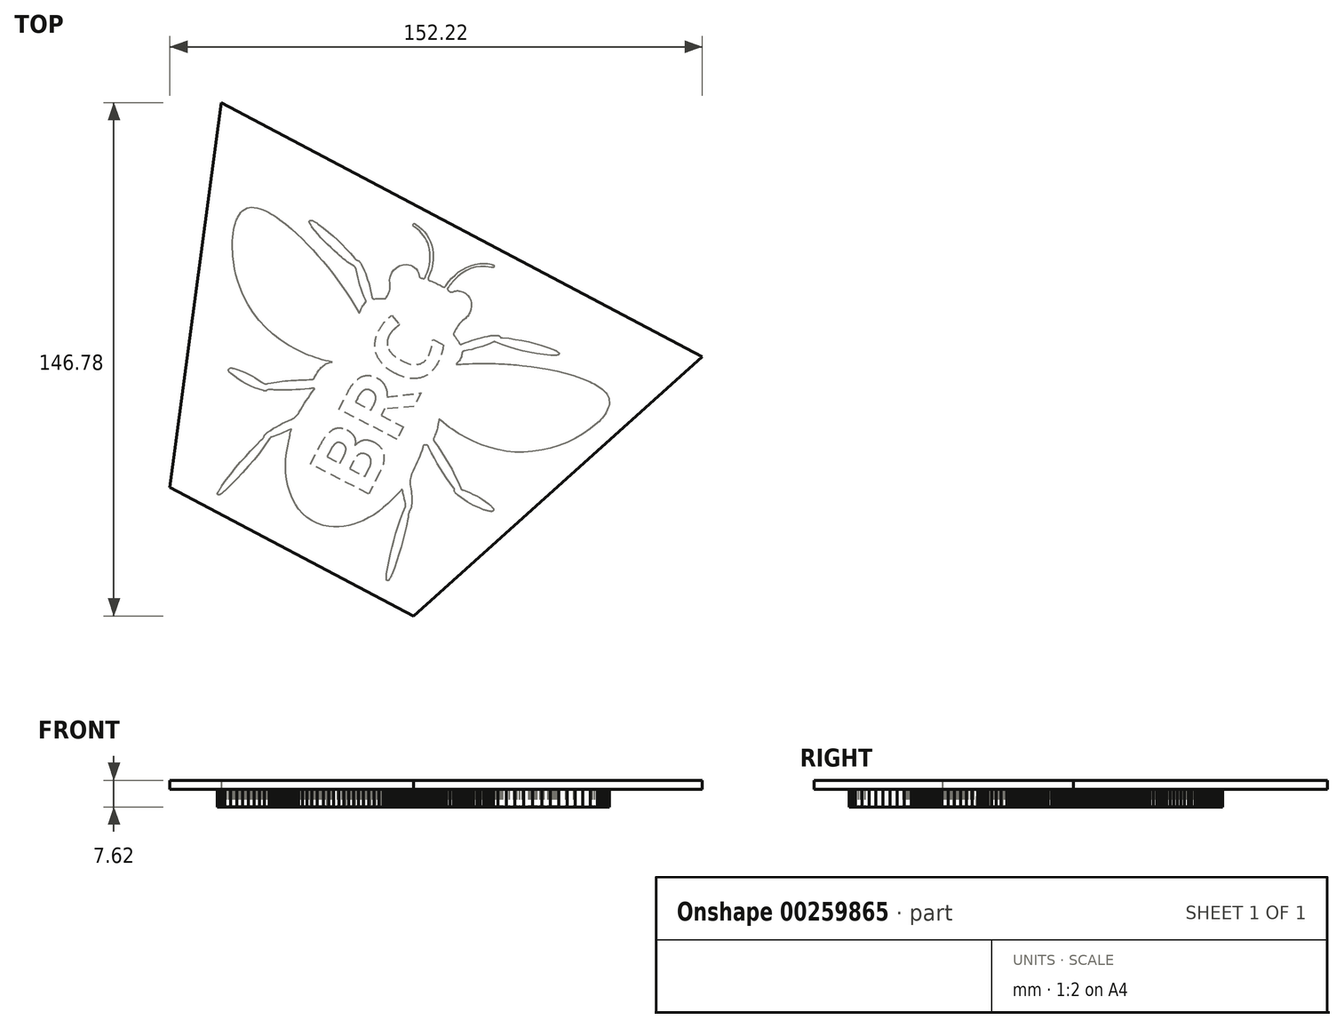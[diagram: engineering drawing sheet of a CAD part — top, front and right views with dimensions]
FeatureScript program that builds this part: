
annotation { "Feature Type Name" : "Feature", "Feature Type Description" : "" }
export const myFeature = defineFeature(function(context is Context, id is Id, definition is map)
    precondition{}
    {
        {
            var Q0;
            Q0=qCreatedBy(makeId("Top.planeOp"),FACE);
            var sketch = newSketch(context, id + "F0", { "sketchPlane" : qUnion([Q0])});
            skLineSegment(sketch, "E0", {"start": v(-34.93, -10.04) * mm, "end": v(-35.64, -10.36) * mm});
            skLineSegment(sketch, "E1", {"start": v(-35.64, -10.36) * mm, "end": v(-36.34, -10.67) * mm});
            skLineSegment(sketch, "E2", {"start": v(-36.34, -10.67) * mm, "end": v(-37.05, -10.97) * mm});
            skLineSegment(sketch, "E3", {"start": v(-37.05, -10.97) * mm, "end": v(-37.75, -11.26) * mm});
            skLineSegment(sketch, "E4", {"start": v(-37.75, -11.26) * mm, "end": v(-38.46, -11.54) * mm});
            skLineSegment(sketch, "E5", {"start": v(-38.46, -11.54) * mm, "end": v(-39.17, -11.8) * mm});
            skLineSegment(sketch, "E6", {"start": v(-39.17, -11.8) * mm, "end": v(-39.88, -12.06) * mm});
            skLineSegment(sketch, "E7", {"start": v(-39.88, -12.06) * mm, "end": v(-40.6, -12.29) * mm});
            skLineSegment(sketch, "E8", {"start": v(-40.6, -12.29) * mm, "end": v(-40.7, -12.33) * mm});
            skLineSegment(sketch, "E9", {"start": v(-40.7, -12.33) * mm, "end": v(-40.8, -12.39) * mm});
            skLineSegment(sketch, "E10", {"start": v(-40.8, -12.39) * mm, "end": v(-40.88, -12.45) * mm});
            skLineSegment(sketch, "E11", {"start": v(-40.88, -12.45) * mm, "end": v(-40.95, -12.53) * mm});
            skLineSegment(sketch, "E12", {"start": v(-40.95, -12.53) * mm, "end": v(-41.02, -12.6) * mm});
            skLineSegment(sketch, "E13", {"start": v(-41.02, -12.6) * mm, "end": v(-41.07, -12.7) * mm});
            skLineSegment(sketch, "E14", {"start": v(-41.07, -12.7) * mm, "end": v(-41.13, -12.78) * mm});
            skLineSegment(sketch, "E15", {"start": v(-41.13, -12.78) * mm, "end": v(-41.2, -12.87) * mm});
            skLineSegment(sketch, "E16", {"start": v(-41.2, -12.87) * mm, "end": v(-42.6, -14.89) * mm});
            skLineSegment(sketch, "E17", {"start": v(-42.6, -14.89) * mm, "end": v(-44.07, -16.86) * mm});
            skLineSegment(sketch, "E18", {"start": v(-44.07, -16.86) * mm, "end": v(-45.6, -18.78) * mm});
            skLineSegment(sketch, "E19", {"start": v(-45.6, -18.78) * mm, "end": v(-47.18, -20.65) * mm});
            skLineSegment(sketch, "E20", {"start": v(-47.18, -20.65) * mm, "end": v(-48.81, -22.48) * mm});
            skLineSegment(sketch, "E21", {"start": v(-48.81, -22.48) * mm, "end": v(-50.5, -24.26) * mm});
            skLineSegment(sketch, "E22", {"start": v(-50.5, -24.26) * mm, "end": v(-52.21, -26.02) * mm});
            skLineSegment(sketch, "E23", {"start": v(-52.21, -26.02) * mm, "end": v(-53.98, -27.73) * mm});
            skLineSegment(sketch, "E24", {"start": v(-53.98, -27.73) * mm, "end": v(-54.12, -27.86) * mm});
            skLineSegment(sketch, "E25", {"start": v(-54.12, -27.86) * mm, "end": v(-54.26, -27.99) * mm});
            skLineSegment(sketch, "E26", {"start": v(-54.26, -27.99) * mm, "end": v(-54.41, -28.1) * mm});
            skLineSegment(sketch, "E27", {"start": v(-54.41, -28.1) * mm, "end": v(-54.56, -28.22) * mm});
            skLineSegment(sketch, "E28", {"start": v(-54.56, -28.22) * mm, "end": v(-54.72, -28.34) * mm});
            skLineSegment(sketch, "E29", {"start": v(-54.72, -28.34) * mm, "end": v(-54.87, -28.45) * mm});
            skLineSegment(sketch, "E30", {"start": v(-54.87, -28.45) * mm, "end": v(-55.03, -28.56) * mm});
            skLineSegment(sketch, "E31", {"start": v(-55.03, -28.56) * mm, "end": v(-55.19, -28.67) * mm});
            skLineSegment(sketch, "E32", {"start": v(-55.19, -28.67) * mm, "end": v(-55.26, -28.73) * mm});
            skLineSegment(sketch, "E33", {"start": v(-55.26, -28.73) * mm, "end": v(-55.35, -28.79) * mm});
            skLineSegment(sketch, "E34", {"start": v(-55.35, -28.79) * mm, "end": v(-55.43, -28.84) * mm});
            skLineSegment(sketch, "E35", {"start": v(-55.43, -28.84) * mm, "end": v(-55.52, -28.87) * mm});
            skLineSegment(sketch, "E36", {"start": v(-55.52, -28.87) * mm, "end": v(-55.61, -28.9) * mm});
            skLineSegment(sketch, "E37", {"start": v(-55.61, -28.9) * mm, "end": v(-55.7, -28.9) * mm});
            skLineSegment(sketch, "E38", {"start": v(-55.7, -28.9) * mm, "end": v(-55.8, -28.87) * mm});
            skLineSegment(sketch, "E39", {"start": v(-55.8, -28.87) * mm, "end": v(-55.88, -28.81) * mm});
            skLineSegment(sketch, "E40", {"start": v(-55.88, -28.81) * mm, "end": v(-55.97, -28.72) * mm});
            skLineSegment(sketch, "E41", {"start": v(-55.97, -28.72) * mm, "end": v(-56.01, -28.63) * mm});
            skLineSegment(sketch, "E42", {"start": v(-56.01, -28.63) * mm, "end": v(-56.03, -28.53) * mm});
            skLineSegment(sketch, "E43", {"start": v(-56.03, -28.53) * mm, "end": v(-56.02, -28.43) * mm});
            skLineSegment(sketch, "E44", {"start": v(-56.02, -28.43) * mm, "end": v(-56, -28.33) * mm});
            skLineSegment(sketch, "E45", {"start": v(-56, -28.33) * mm, "end": v(-55.95, -28.23) * mm});
            skLineSegment(sketch, "E46", {"start": v(-55.95, -28.23) * mm, "end": v(-55.9, -28.14) * mm});
            skLineSegment(sketch, "E47", {"start": v(-55.9, -28.14) * mm, "end": v(-55.85, -28.05) * mm});
            skLineSegment(sketch, "E48", {"start": v(-55.85, -28.05) * mm, "end": v(-55.73, -27.83) * mm});
            skLineSegment(sketch, "E49", {"start": v(-55.73, -27.83) * mm, "end": v(-55.6, -27.61) * mm});
            skLineSegment(sketch, "E50", {"start": v(-55.6, -27.61) * mm, "end": v(-55.48, -27.4) * mm});
            skLineSegment(sketch, "E51", {"start": v(-55.48, -27.4) * mm, "end": v(-55.36, -27.18) * mm});
            skLineSegment(sketch, "E52", {"start": v(-55.36, -27.18) * mm, "end": v(-55.23, -26.96) * mm});
            skLineSegment(sketch, "E53", {"start": v(-55.23, -26.96) * mm, "end": v(-55.1, -26.75) * mm});
            skLineSegment(sketch, "E54", {"start": v(-55.1, -26.75) * mm, "end": v(-54.96, -26.54) * mm});
            skLineSegment(sketch, "E55", {"start": v(-54.96, -26.54) * mm, "end": v(-54.82, -26.34) * mm});
            skLineSegment(sketch, "E56", {"start": v(-54.82, -26.34) * mm, "end": v(-53.53, -24.58) * mm});
            skLineSegment(sketch, "E57", {"start": v(-53.53, -24.58) * mm, "end": v(-52.2, -22.85) * mm});
            skLineSegment(sketch, "E58", {"start": v(-52.2, -22.85) * mm, "end": v(-50.84, -21.15) * mm});
            skLineSegment(sketch, "E59", {"start": v(-50.84, -21.15) * mm, "end": v(-49.44, -19.5) * mm});
            skLineSegment(sketch, "E60", {"start": v(-49.44, -19.5) * mm, "end": v(-48, -17.86) * mm});
            skLineSegment(sketch, "E61", {"start": v(-48, -17.86) * mm, "end": v(-46.52, -16.26) * mm});
            skLineSegment(sketch, "E62", {"start": v(-46.52, -16.26) * mm, "end": v(-45.01, -14.7) * mm});
            skLineSegment(sketch, "E63", {"start": v(-45.01, -14.7) * mm, "end": v(-43.47, -13.15) * mm});
            skLineSegment(sketch, "E64", {"start": v(-43.47, -13.15) * mm, "end": v(-43.34, -13.03) * mm});
            skLineSegment(sketch, "E65", {"start": v(-43.34, -13.03) * mm, "end": v(-43.21, -12.9) * mm});
            skLineSegment(sketch, "E66", {"start": v(-43.21, -12.9) * mm, "end": v(-43.1, -12.78) * mm});
            skLineSegment(sketch, "E67", {"start": v(-43.1, -12.78) * mm, "end": v(-42.98, -12.65) * mm});
            skLineSegment(sketch, "E68", {"start": v(-42.98, -12.65) * mm, "end": v(-42.87, -12.5) * mm});
            skLineSegment(sketch, "E69", {"start": v(-42.87, -12.5) * mm, "end": v(-42.78, -12.36) * mm});
            skLineSegment(sketch, "E70", {"start": v(-42.78, -12.36) * mm, "end": v(-42.7, -12.19) * mm});
            skLineSegment(sketch, "E71", {"start": v(-42.7, -12.19) * mm, "end": v(-42.65, -12) * mm});
            skLineSegment(sketch, "E72", {"start": v(-42.65, -12) * mm, "end": v(-42.6, -11.83) * mm});
            skLineSegment(sketch, "E73", {"start": v(-42.6, -11.83) * mm, "end": v(-42.5, -11.67) * mm});
            skLineSegment(sketch, "E74", {"start": v(-42.5, -11.67) * mm, "end": v(-42.4, -11.53) * mm});
            skLineSegment(sketch, "E75", {"start": v(-42.4, -11.53) * mm, "end": v(-42.27, -11.4) * mm});
            skLineSegment(sketch, "E76", {"start": v(-42.27, -11.4) * mm, "end": v(-42.12, -11.28) * mm});
            skLineSegment(sketch, "E77", {"start": v(-42.12, -11.28) * mm, "end": v(-41.97, -11.17) * mm});
            skLineSegment(sketch, "E78", {"start": v(-41.97, -11.17) * mm, "end": v(-41.82, -11.06) * mm});
            skLineSegment(sketch, "E79", {"start": v(-41.82, -11.06) * mm, "end": v(-41.67, -10.95) * mm});
            skLineSegment(sketch, "E80", {"start": v(-41.67, -10.95) * mm, "end": v(-40.87, -10.38) * mm});
            skLineSegment(sketch, "E81", {"start": v(-40.87, -10.38) * mm, "end": v(-40.05, -9.85) * mm});
            skLineSegment(sketch, "E82", {"start": v(-40.05, -9.85) * mm, "end": v(-39.2, -9.35) * mm});
            skLineSegment(sketch, "E83", {"start": v(-39.2, -9.35) * mm, "end": v(-38.35, -8.88) * mm});
            skLineSegment(sketch, "E84", {"start": v(-38.35, -8.88) * mm, "end": v(-37.48, -8.43) * mm});
            skLineSegment(sketch, "E85", {"start": v(-37.48, -8.43) * mm, "end": v(-36.6, -8) * mm});
            skLineSegment(sketch, "E86", {"start": v(-36.6, -8) * mm, "end": v(-35.71, -7.6) * mm});
            skLineSegment(sketch, "E87", {"start": v(-35.71, -7.6) * mm, "end": v(-34.81, -7.22) * mm});
            skLineSegment(sketch, "E88", {"start": v(-34.81, -7.22) * mm, "end": v(-34.46, -7.05) * mm});
            skLineSegment(sketch, "E89", {"start": v(-34.46, -7.05) * mm, "end": v(-34.13, -6.85) * mm});
            skLineSegment(sketch, "E90", {"start": v(-34.13, -6.85) * mm, "end": v(-33.83, -6.63) * mm});
            skLineSegment(sketch, "E91", {"start": v(-33.83, -6.63) * mm, "end": v(-33.55, -6.39) * mm});
            skLineSegment(sketch, "E92", {"start": v(-33.55, -6.39) * mm, "end": v(-33.3, -6.12) * mm});
            skLineSegment(sketch, "E93", {"start": v(-33.3, -6.12) * mm, "end": v(-33.06, -5.85) * mm});
            skLineSegment(sketch, "E94", {"start": v(-33.06, -5.85) * mm, "end": v(-32.85, -5.56) * mm});
            skLineSegment(sketch, "E95", {"start": v(-32.85, -5.56) * mm, "end": v(-32.66, -5.26) * mm});
            skLineSegment(sketch, "E96", {"start": v(-32.66, -5.26) * mm, "end": v(-32.16, -4.42) * mm});
            skLineSegment(sketch, "E97", {"start": v(-32.16, -4.42) * mm, "end": v(-31.66, -3.58) * mm});
            skLineSegment(sketch, "E98", {"start": v(-31.66, -3.58) * mm, "end": v(-31.15, -2.74) * mm});
            skLineSegment(sketch, "E99", {"start": v(-31.15, -2.74) * mm, "end": v(-30.63, -1.91) * mm});
            skLineSegment(sketch, "E100", {"start": v(-30.63, -1.91) * mm, "end": v(-30.1, -1.1) * mm});
            skLineSegment(sketch, "E101", {"start": v(-30.1, -1.1) * mm, "end": v(-29.54, -0.3) * mm});
            skLineSegment(sketch, "E102", {"start": v(-29.54, -0.3) * mm, "end": v(-28.96, 0.5) * mm});
            skLineSegment(sketch, "E103", {"start": v(-28.96, 0.5) * mm, "end": v(-28.36, 1.27) * mm});
            skLineSegment(sketch, "E104", {"start": v(-28.36, 1.27) * mm, "end": v(-28.34, 1.3) * mm});
            skLineSegment(sketch, "E105", {"start": v(-28.34, 1.3) * mm, "end": v(-28.32, 1.33) * mm});
            skLineSegment(sketch, "E106", {"start": v(-28.32, 1.33) * mm, "end": v(-28.3, 1.36) * mm});
            skLineSegment(sketch, "E107", {"start": v(-28.3, 1.36) * mm, "end": v(-28.29, 1.4) * mm});
            skLineSegment(sketch, "E108", {"start": v(-28.29, 1.4) * mm, "end": v(-28.27, 1.44) * mm});
            skLineSegment(sketch, "E109", {"start": v(-28.27, 1.44) * mm, "end": v(-28.26, 1.47) * mm});
            skLineSegment(sketch, "E110", {"start": v(-28.26, 1.47) * mm, "end": v(-28.24, 1.51) * mm});
            skLineSegment(sketch, "E111", {"start": v(-28.24, 1.51) * mm, "end": v(-28.22, 1.56) * mm});
            skLineSegment(sketch, "E112", {"start": v(-28.22, 1.56) * mm, "end": v(-28.43, 1.62) * mm});
            skLineSegment(sketch, "E113", {"start": v(-28.43, 1.62) * mm, "end": v(-28.63, 1.64) * mm});
            skLineSegment(sketch, "E114", {"start": v(-28.63, 1.64) * mm, "end": v(-28.82, 1.64) * mm});
            skLineSegment(sketch, "E115", {"start": v(-28.82, 1.64) * mm, "end": v(-29.01, 1.62) * mm});
            skLineSegment(sketch, "E116", {"start": v(-29.01, 1.62) * mm, "end": v(-29.2, 1.6) * mm});
            skLineSegment(sketch, "E117", {"start": v(-29.2, 1.6) * mm, "end": v(-29.39, 1.56) * mm});
            skLineSegment(sketch, "E118", {"start": v(-29.39, 1.56) * mm, "end": v(-29.57, 1.52) * mm});
            skLineSegment(sketch, "E119", {"start": v(-29.57, 1.52) * mm, "end": v(-29.76, 1.5) * mm});
            skLineSegment(sketch, "E120", {"start": v(-29.76, 1.5) * mm, "end": v(-31.02, 1.39) * mm});
            skLineSegment(sketch, "E121", {"start": v(-31.02, 1.39) * mm, "end": v(-32.28, 1.3) * mm});
            skLineSegment(sketch, "E122", {"start": v(-32.28, 1.3) * mm, "end": v(-33.54, 1.24) * mm});
            skLineSegment(sketch, "E123", {"start": v(-33.54, 1.24) * mm, "end": v(-34.8, 1.2) * mm});
            skLineSegment(sketch, "E124", {"start": v(-34.8, 1.2) * mm, "end": v(-36.07, 1.17) * mm});
            skLineSegment(sketch, "E125", {"start": v(-36.07, 1.17) * mm, "end": v(-37.34, 1.16) * mm});
            skLineSegment(sketch, "E126", {"start": v(-37.34, 1.16) * mm, "end": v(-38.6, 1.17) * mm});
            skLineSegment(sketch, "E127", {"start": v(-38.6, 1.17) * mm, "end": v(-39.87, 1.18) * mm});
            skLineSegment(sketch, "E128", {"start": v(-39.87, 1.18) * mm, "end": v(-40.15, 1.2) * mm});
            skLineSegment(sketch, "E129", {"start": v(-40.15, 1.2) * mm, "end": v(-40.43, 1.22) * mm});
            skLineSegment(sketch, "E130", {"start": v(-40.43, 1.22) * mm, "end": v(-40.7, 1.25) * mm});
            skLineSegment(sketch, "E131", {"start": v(-40.7, 1.25) * mm, "end": v(-40.98, 1.27) * mm});
            skLineSegment(sketch, "E132", {"start": v(-40.98, 1.27) * mm, "end": v(-41.26, 1.26) * mm});
            skLineSegment(sketch, "E133", {"start": v(-41.26, 1.26) * mm, "end": v(-41.53, 1.2) * mm});
            skLineSegment(sketch, "E134", {"start": v(-41.53, 1.2) * mm, "end": v(-41.8, 1.1) * mm});
            skLineSegment(sketch, "E135", {"start": v(-41.8, 1.1) * mm, "end": v(-42.07, 0.93) * mm});
            skLineSegment(sketch, "E136", {"start": v(-42.07, 0.93) * mm, "end": v(-42.13, 0.9) * mm});
            skLineSegment(sketch, "E137", {"start": v(-42.13, 0.9) * mm, "end": v(-42.21, 0.87) * mm});
            skLineSegment(sketch, "E138", {"start": v(-42.21, 0.87) * mm, "end": v(-42.3, 0.86) * mm});
            skLineSegment(sketch, "E139", {"start": v(-42.3, 0.86) * mm, "end": v(-42.4, 0.87) * mm});
            skLineSegment(sketch, "E140", {"start": v(-42.4, 0.87) * mm, "end": v(-42.51, 0.88) * mm});
            skLineSegment(sketch, "E141", {"start": v(-42.51, 0.88) * mm, "end": v(-42.62, 0.9) * mm});
            skLineSegment(sketch, "E142", {"start": v(-42.62, 0.9) * mm, "end": v(-42.72, 0.92) * mm});
            skLineSegment(sketch, "E143", {"start": v(-42.72, 0.92) * mm, "end": v(-42.81, 0.94) * mm});
            skLineSegment(sketch, "E144", {"start": v(-42.81, 0.94) * mm, "end": v(-44.1, 1.32) * mm});
            skLineSegment(sketch, "E145", {"start": v(-44.1, 1.32) * mm, "end": v(-45.36, 1.77) * mm});
            skLineSegment(sketch, "E146", {"start": v(-45.36, 1.77) * mm, "end": v(-46.59, 2.28) * mm});
            skLineSegment(sketch, "E147", {"start": v(-46.59, 2.28) * mm, "end": v(-47.77, 2.86) * mm});
            skLineSegment(sketch, "E148", {"start": v(-47.77, 2.86) * mm, "end": v(-48.92, 3.51) * mm});
            skLineSegment(sketch, "E149", {"start": v(-48.92, 3.51) * mm, "end": v(-50.04, 4.23) * mm});
            skLineSegment(sketch, "E150", {"start": v(-50.04, 4.23) * mm, "end": v(-51.12, 5.01) * mm});
            skLineSegment(sketch, "E151", {"start": v(-51.12, 5.01) * mm, "end": v(-52.16, 5.87) * mm});
            skLineSegment(sketch, "E152", {"start": v(-52.16, 5.87) * mm, "end": v(-52.3, 5.99) * mm});
            skLineSegment(sketch, "E153", {"start": v(-52.3, 5.99) * mm, "end": v(-52.46, 6.12) * mm});
            skLineSegment(sketch, "E154", {"start": v(-52.46, 6.12) * mm, "end": v(-52.6, 6.26) * mm});
            skLineSegment(sketch, "E155", {"start": v(-52.6, 6.26) * mm, "end": v(-52.72, 6.4) * mm});
            skLineSegment(sketch, "E156", {"start": v(-52.72, 6.4) * mm, "end": v(-52.82, 6.57) * mm});
            skLineSegment(sketch, "E157", {"start": v(-52.82, 6.57) * mm, "end": v(-52.86, 6.74) * mm});
            skLineSegment(sketch, "E158", {"start": v(-52.86, 6.74) * mm, "end": v(-52.85, 6.93) * mm});
            skLineSegment(sketch, "E159", {"start": v(-52.85, 6.93) * mm, "end": v(-52.77, 7.13) * mm});
            skLineSegment(sketch, "E160", {"start": v(-52.77, 7.13) * mm, "end": v(-52.64, 7.3) * mm});
            skLineSegment(sketch, "E161", {"start": v(-52.64, 7.3) * mm, "end": v(-52.49, 7.4) * mm});
            skLineSegment(sketch, "E162", {"start": v(-52.49, 7.4) * mm, "end": v(-52.32, 7.45) * mm});
            skLineSegment(sketch, "E163", {"start": v(-52.32, 7.45) * mm, "end": v(-52.13, 7.46) * mm});
            skLineSegment(sketch, "E164", {"start": v(-52.13, 7.46) * mm, "end": v(-51.94, 7.44) * mm});
            skLineSegment(sketch, "E165", {"start": v(-51.94, 7.44) * mm, "end": v(-51.74, 7.4) * mm});
            skLineSegment(sketch, "E166", {"start": v(-51.74, 7.4) * mm, "end": v(-51.55, 7.35) * mm});
            skLineSegment(sketch, "E167", {"start": v(-51.55, 7.35) * mm, "end": v(-51.36, 7.3) * mm});
            skLineSegment(sketch, "E168", {"start": v(-51.36, 7.3) * mm, "end": v(-50.29, 7) * mm});
            skLineSegment(sketch, "E169", {"start": v(-50.29, 7) * mm, "end": v(-49.24, 6.62) * mm});
            skLineSegment(sketch, "E170", {"start": v(-49.24, 6.62) * mm, "end": v(-48.21, 6.2) * mm});
            skLineSegment(sketch, "E171", {"start": v(-48.21, 6.2) * mm, "end": v(-47.21, 5.72) * mm});
            skLineSegment(sketch, "E172", {"start": v(-47.21, 5.72) * mm, "end": v(-46.24, 5.2) * mm});
            skLineSegment(sketch, "E173", {"start": v(-46.24, 5.2) * mm, "end": v(-45.28, 4.64) * mm});
            skLineSegment(sketch, "E174", {"start": v(-45.28, 4.64) * mm, "end": v(-44.35, 4.03) * mm});
            skLineSegment(sketch, "E175", {"start": v(-44.35, 4.03) * mm, "end": v(-43.44, 3.38) * mm});
            skLineSegment(sketch, "E176", {"start": v(-43.44, 3.38) * mm, "end": v(-43.2, 3.23) * mm});
            skLineSegment(sketch, "E177", {"start": v(-43.2, 3.23) * mm, "end": v(-42.99, 3.1) * mm});
            skLineSegment(sketch, "E178", {"start": v(-42.99, 3.1) * mm, "end": v(-42.77, 3.02) * mm});
            skLineSegment(sketch, "E179", {"start": v(-42.77, 3.02) * mm, "end": v(-42.54, 2.95) * mm});
            skLineSegment(sketch, "E180", {"start": v(-42.54, 2.95) * mm, "end": v(-42.31, 2.92) * mm});
            skLineSegment(sketch, "E181", {"start": v(-42.31, 2.92) * mm, "end": v(-42.07, 2.92) * mm});
            skLineSegment(sketch, "E182", {"start": v(-42.07, 2.92) * mm, "end": v(-41.82, 2.94) * mm});
            skLineSegment(sketch, "E183", {"start": v(-41.82, 2.94) * mm, "end": v(-41.55, 3) * mm});
            skLineSegment(sketch, "E184", {"start": v(-41.55, 3) * mm, "end": v(-40.75, 3.19) * mm});
            skLineSegment(sketch, "E185", {"start": v(-40.75, 3.19) * mm, "end": v(-39.94, 3.34) * mm});
            skLineSegment(sketch, "E186", {"start": v(-39.94, 3.34) * mm, "end": v(-39.13, 3.48) * mm});
            skLineSegment(sketch, "E187", {"start": v(-39.13, 3.48) * mm, "end": v(-38.31, 3.6) * mm});
            skLineSegment(sketch, "E188", {"start": v(-38.31, 3.6) * mm, "end": v(-37.5, 3.69) * mm});
            skLineSegment(sketch, "E189", {"start": v(-37.5, 3.69) * mm, "end": v(-36.68, 3.77) * mm});
            skLineSegment(sketch, "E190", {"start": v(-36.68, 3.77) * mm, "end": v(-35.85, 3.83) * mm});
            skLineSegment(sketch, "E191", {"start": v(-35.85, 3.83) * mm, "end": v(-35.03, 3.88) * mm});
            skLineSegment(sketch, "E192", {"start": v(-35.03, 3.88) * mm, "end": v(-34.28, 3.92) * mm});
            skLineSegment(sketch, "E193", {"start": v(-34.28, 3.92) * mm, "end": v(-33.54, 3.96) * mm});
            skLineSegment(sketch, "E194", {"start": v(-33.54, 3.96) * mm, "end": v(-32.8, 4) * mm});
            skLineSegment(sketch, "E195", {"start": v(-32.8, 4) * mm, "end": v(-32.05, 4.03) * mm});
            skLineSegment(sketch, "E196", {"start": v(-32.05, 4.03) * mm, "end": v(-31.3, 4.06) * mm});
            skLineSegment(sketch, "E197", {"start": v(-31.3, 4.06) * mm, "end": v(-30.55, 4.1) * mm});
            skLineSegment(sketch, "E198", {"start": v(-30.55, 4.1) * mm, "end": v(-29.8, 4.12) * mm});
            skLineSegment(sketch, "E199", {"start": v(-29.8, 4.12) * mm, "end": v(-29.06, 4.15) * mm});
            skLineSegment(sketch, "E200", {"start": v(-29.06, 4.15) * mm, "end": v(-28.9, 4.17) * mm});
            skLineSegment(sketch, "E201", {"start": v(-28.9, 4.17) * mm, "end": v(-28.75, 4.2) * mm});
            skLineSegment(sketch, "E202", {"start": v(-28.75, 4.2) * mm, "end": v(-28.63, 4.26) * mm});
            skLineSegment(sketch, "E203", {"start": v(-28.63, 4.26) * mm, "end": v(-28.52, 4.34) * mm});
            skLineSegment(sketch, "E204", {"start": v(-28.52, 4.34) * mm, "end": v(-28.43, 4.43) * mm});
            skLineSegment(sketch, "E205", {"start": v(-28.43, 4.43) * mm, "end": v(-28.35, 4.54) * mm});
            skLineSegment(sketch, "E206", {"start": v(-28.35, 4.54) * mm, "end": v(-28.27, 4.65) * mm});
            skLineSegment(sketch, "E207", {"start": v(-28.27, 4.65) * mm, "end": v(-28.2, 4.79) * mm});
            skLineSegment(sketch, "E208", {"start": v(-28.2, 4.79) * mm, "end": v(-27.99, 5.22) * mm});
            skLineSegment(sketch, "E209", {"start": v(-27.99, 5.22) * mm, "end": v(-27.76, 5.64) * mm});
            skLineSegment(sketch, "E210", {"start": v(-27.76, 5.64) * mm, "end": v(-27.51, 6.05) * mm});
            skLineSegment(sketch, "E211", {"start": v(-27.51, 6.05) * mm, "end": v(-27.26, 6.45) * mm});
            skLineSegment(sketch, "E212", {"start": v(-27.26, 6.45) * mm, "end": v(-26.98, 6.84) * mm});
            skLineSegment(sketch, "E213", {"start": v(-26.98, 6.84) * mm, "end": v(-26.68, 7.22) * mm});
            skLineSegment(sketch, "E214", {"start": v(-26.68, 7.22) * mm, "end": v(-26.36, 7.58) * mm});
            skLineSegment(sketch, "E215", {"start": v(-26.36, 7.58) * mm, "end": v(-26.02, 7.92) * mm});
            skLineSegment(sketch, "E216", {"start": v(-26.02, 7.92) * mm, "end": v(-25.72, 8.18) * mm});
            skLineSegment(sketch, "E217", {"start": v(-25.72, 8.18) * mm, "end": v(-25.4, 8.42) * mm});
            skLineSegment(sketch, "E218", {"start": v(-25.4, 8.42) * mm, "end": v(-25.07, 8.62) * mm});
            skLineSegment(sketch, "E219", {"start": v(-25.07, 8.62) * mm, "end": v(-24.73, 8.8) * mm});
            skLineSegment(sketch, "E220", {"start": v(-24.73, 8.8) * mm, "end": v(-24.37, 8.94) * mm});
            skLineSegment(sketch, "E221", {"start": v(-24.37, 8.94) * mm, "end": v(-24, 9.04) * mm});
            skLineSegment(sketch, "E222", {"start": v(-24, 9.04) * mm, "end": v(-23.6, 9.1) * mm});
            skLineSegment(sketch, "E223", {"start": v(-23.6, 9.1) * mm, "end": v(-23.18, 9.12) * mm});
            skLineSegment(sketch, "E224", {"start": v(-23.18, 9.12) * mm, "end": v(-24.16, 9.33) * mm});
            skLineSegment(sketch, "E225", {"start": v(-24.16, 9.33) * mm, "end": v(-25.14, 9.56) * mm});
            skLineSegment(sketch, "E226", {"start": v(-25.14, 9.56) * mm, "end": v(-26.1, 9.81) * mm});
            skLineSegment(sketch, "E227", {"start": v(-26.1, 9.81) * mm, "end": v(-27.06, 10.1) * mm});
            skLineSegment(sketch, "E228", {"start": v(-27.06, 10.1) * mm, "end": v(-28, 10.4) * mm});
            skLineSegment(sketch, "E229", {"start": v(-28, 10.4) * mm, "end": v(-28.95, 10.73) * mm});
            skLineSegment(sketch, "E230", {"start": v(-28.95, 10.73) * mm, "end": v(-29.88, 11.08) * mm});
            skLineSegment(sketch, "E231", {"start": v(-29.88, 11.08) * mm, "end": v(-30.8, 11.47) * mm});
            skLineSegment(sketch, "E232", {"start": v(-30.8, 11.47) * mm, "end": v(-33.36, 12.67) * mm});
            skLineSegment(sketch, "E233", {"start": v(-33.36, 12.67) * mm, "end": v(-35.8, 14.02) * mm});
            skLineSegment(sketch, "E234", {"start": v(-35.8, 14.02) * mm, "end": v(-38.1, 15.52) * mm});
            skLineSegment(sketch, "E235", {"start": v(-38.1, 15.52) * mm, "end": v(-40.26, 17.19) * mm});
            skLineSegment(sketch, "E236", {"start": v(-40.26, 17.19) * mm, "end": v(-42.27, 19.02) * mm});
            skLineSegment(sketch, "E237", {"start": v(-42.27, 19.02) * mm, "end": v(-44.13, 21.04) * mm});
            skLineSegment(sketch, "E238", {"start": v(-44.13, 21.04) * mm, "end": v(-45.83, 23.24) * mm});
            skLineSegment(sketch, "E239", {"start": v(-45.83, 23.24) * mm, "end": v(-47.35, 25.64) * mm});
            skLineSegment(sketch, "E240", {"start": v(-47.35, 25.64) * mm, "end": v(-48.22, 27.27) * mm});
            skLineSegment(sketch, "E241", {"start": v(-48.22, 27.27) * mm, "end": v(-48.99, 28.92) * mm});
            skLineSegment(sketch, "E242", {"start": v(-48.99, 28.92) * mm, "end": v(-49.65, 30.6) * mm});
            skLineSegment(sketch, "E243", {"start": v(-49.65, 30.6) * mm, "end": v(-50.22, 32.33) * mm});
            skLineSegment(sketch, "E244", {"start": v(-50.22, 32.33) * mm, "end": v(-50.69, 34.08) * mm});
            skLineSegment(sketch, "E245", {"start": v(-50.69, 34.08) * mm, "end": v(-51.07, 35.85) * mm});
            skLineSegment(sketch, "E246", {"start": v(-51.07, 35.85) * mm, "end": v(-51.37, 37.65) * mm});
            skLineSegment(sketch, "E247", {"start": v(-51.37, 37.65) * mm, "end": v(-51.58, 39.48) * mm});
            skLineSegment(sketch, "E248", {"start": v(-51.58, 39.48) * mm, "end": v(-51.67, 40.56) * mm});
            skLineSegment(sketch, "E249", {"start": v(-51.67, 40.56) * mm, "end": v(-51.73, 41.65) * mm});
            skLineSegment(sketch, "E250", {"start": v(-51.73, 41.65) * mm, "end": v(-51.74, 42.73) * mm});
            skLineSegment(sketch, "E251", {"start": v(-51.74, 42.73) * mm, "end": v(-51.72, 43.8) * mm});
            skLineSegment(sketch, "E252", {"start": v(-51.72, 43.8) * mm, "end": v(-51.65, 44.88) * mm});
            skLineSegment(sketch, "E253", {"start": v(-51.65, 44.88) * mm, "end": v(-51.53, 45.96) * mm});
            skLineSegment(sketch, "E254", {"start": v(-51.53, 45.96) * mm, "end": v(-51.35, 47.03) * mm});
            skLineSegment(sketch, "E255", {"start": v(-51.35, 47.03) * mm, "end": v(-51.12, 48.1) * mm});
            skLineSegment(sketch, "E256", {"start": v(-51.12, 48.1) * mm, "end": v(-51, 48.51) * mm});
            skLineSegment(sketch, "E257", {"start": v(-51, 48.51) * mm, "end": v(-50.89, 48.92) * mm});
            skLineSegment(sketch, "E258", {"start": v(-50.89, 48.92) * mm, "end": v(-50.75, 49.33) * mm});
            skLineSegment(sketch, "E259", {"start": v(-50.75, 49.33) * mm, "end": v(-50.6, 49.73) * mm});
            skLineSegment(sketch, "E260", {"start": v(-50.6, 49.73) * mm, "end": v(-50.43, 50.13) * mm});
            skLineSegment(sketch, "E261", {"start": v(-50.43, 50.13) * mm, "end": v(-50.24, 50.51) * mm});
            skLineSegment(sketch, "E262", {"start": v(-50.24, 50.51) * mm, "end": v(-50.03, 50.9) * mm});
            skLineSegment(sketch, "E263", {"start": v(-50.03, 50.9) * mm, "end": v(-49.8, 51.26) * mm});
            skLineSegment(sketch, "E264", {"start": v(-49.8, 51.26) * mm, "end": v(-49.3, 51.9) * mm});
            skLineSegment(sketch, "E265", {"start": v(-49.3, 51.9) * mm, "end": v(-48.79, 52.43) * mm});
            skLineSegment(sketch, "E266", {"start": v(-48.79, 52.43) * mm, "end": v(-48.23, 52.84) * mm});
            skLineSegment(sketch, "E267", {"start": v(-48.23, 52.84) * mm, "end": v(-47.62, 53.14) * mm});
            skLineSegment(sketch, "E268", {"start": v(-47.62, 53.14) * mm, "end": v(-46.97, 53.33) * mm});
            skLineSegment(sketch, "E269", {"start": v(-46.97, 53.33) * mm, "end": v(-46.27, 53.4) * mm});
            skLineSegment(sketch, "E270", {"start": v(-46.27, 53.4) * mm, "end": v(-45.5, 53.36) * mm});
            skLineSegment(sketch, "E271", {"start": v(-45.5, 53.36) * mm, "end": v(-44.68, 53.22) * mm});
            skLineSegment(sketch, "E272", {"start": v(-44.68, 53.22) * mm, "end": v(-43.8, 52.98) * mm});
            skLineSegment(sketch, "E273", {"start": v(-43.8, 52.98) * mm, "end": v(-42.95, 52.67) * mm});
            skLineSegment(sketch, "E274", {"start": v(-42.95, 52.67) * mm, "end": v(-42.12, 52.32) * mm});
            skLineSegment(sketch, "E275", {"start": v(-42.12, 52.32) * mm, "end": v(-41.32, 51.91) * mm});
            skLineSegment(sketch, "E276", {"start": v(-41.32, 51.91) * mm, "end": v(-40.54, 51.47) * mm});
            skLineSegment(sketch, "E277", {"start": v(-40.54, 51.47) * mm, "end": v(-39.78, 51) * mm});
            skLineSegment(sketch, "E278", {"start": v(-39.78, 51) * mm, "end": v(-39.03, 50.49) * mm});
            skLineSegment(sketch, "E279", {"start": v(-39.03, 50.49) * mm, "end": v(-38.3, 49.96) * mm});
            skLineSegment(sketch, "E280", {"start": v(-38.3, 49.96) * mm, "end": v(-36.57, 48.64) * mm});
            skLineSegment(sketch, "E281", {"start": v(-36.57, 48.64) * mm, "end": v(-34.9, 47.27) * mm});
            skLineSegment(sketch, "E282", {"start": v(-34.9, 47.27) * mm, "end": v(-33.3, 45.83) * mm});
            skLineSegment(sketch, "E283", {"start": v(-33.3, 45.83) * mm, "end": v(-31.74, 44.34) * mm});
            skLineSegment(sketch, "E284", {"start": v(-31.74, 44.34) * mm, "end": v(-30.23, 42.8) * mm});
            skLineSegment(sketch, "E285", {"start": v(-30.23, 42.8) * mm, "end": v(-28.76, 41.23) * mm});
            skLineSegment(sketch, "E286", {"start": v(-28.76, 41.23) * mm, "end": v(-27.32, 39.62) * mm});
            skLineSegment(sketch, "E287", {"start": v(-27.32, 39.62) * mm, "end": v(-25.91, 37.98) * mm});
            skLineSegment(sketch, "E288", {"start": v(-25.91, 37.98) * mm, "end": v(-24.5, 36.27) * mm});
            skLineSegment(sketch, "E289", {"start": v(-24.5, 36.27) * mm, "end": v(-23.12, 34.53) * mm});
            skLineSegment(sketch, "E290", {"start": v(-23.12, 34.53) * mm, "end": v(-21.78, 32.77) * mm});
            skLineSegment(sketch, "E291", {"start": v(-21.78, 32.77) * mm, "end": v(-20.48, 30.98) * mm});
            skLineSegment(sketch, "E292", {"start": v(-20.48, 30.98) * mm, "end": v(-19.22, 29.15) * mm});
            skLineSegment(sketch, "E293", {"start": v(-19.22, 29.15) * mm, "end": v(-18.02, 27.3) * mm});
            skLineSegment(sketch, "E294", {"start": v(-18.02, 27.3) * mm, "end": v(-16.85, 25.41) * mm});
            skLineSegment(sketch, "E295", {"start": v(-16.85, 25.41) * mm, "end": v(-15.74, 23.49) * mm});
            skLineSegment(sketch, "E296", {"start": v(-15.74, 23.49) * mm, "end": v(-15.72, 23.45) * mm});
            skLineSegment(sketch, "E297", {"start": v(-15.72, 23.45) * mm, "end": v(-15.7, 23.4) * mm});
            skLineSegment(sketch, "E298", {"start": v(-15.7, 23.4) * mm, "end": v(-15.67, 23.36) * mm});
            skLineSegment(sketch, "E299", {"start": v(-15.67, 23.36) * mm, "end": v(-15.64, 23.33) * mm});
            skLineSegment(sketch, "E300", {"start": v(-15.64, 23.33) * mm, "end": v(-15.6, 23.3) * mm});
            skLineSegment(sketch, "E301", {"start": v(-15.6, 23.3) * mm, "end": v(-15.54, 23.26) * mm});
            skLineSegment(sketch, "E302", {"start": v(-15.54, 23.26) * mm, "end": v(-15.48, 23.24) * mm});
            skLineSegment(sketch, "E303", {"start": v(-15.48, 23.24) * mm, "end": v(-15.4, 23.22) * mm});
            skLineSegment(sketch, "E304", {"start": v(-15.4, 23.22) * mm, "end": v(-15.23, 23.62) * mm});
            skLineSegment(sketch, "E305", {"start": v(-15.23, 23.62) * mm, "end": v(-15.06, 24.03) * mm});
            skLineSegment(sketch, "E306", {"start": v(-15.06, 24.03) * mm, "end": v(-14.87, 24.43) * mm});
            skLineSegment(sketch, "E307", {"start": v(-14.87, 24.43) * mm, "end": v(-14.67, 24.83) * mm});
            skLineSegment(sketch, "E308", {"start": v(-14.67, 24.83) * mm, "end": v(-14.45, 25.2) * mm});
            skLineSegment(sketch, "E309", {"start": v(-14.45, 25.2) * mm, "end": v(-14.2, 25.58) * mm});
            skLineSegment(sketch, "E310", {"start": v(-14.2, 25.58) * mm, "end": v(-13.93, 25.93) * mm});
            skLineSegment(sketch, "E311", {"start": v(-13.93, 25.93) * mm, "end": v(-13.61, 26.26) * mm});
            skLineSegment(sketch, "E312", {"start": v(-13.61, 26.26) * mm, "end": v(-13.55, 26.34) * mm});
            skLineSegment(sketch, "E313", {"start": v(-13.55, 26.34) * mm, "end": v(-13.52, 26.41) * mm});
            skLineSegment(sketch, "E314", {"start": v(-13.52, 26.41) * mm, "end": v(-13.51, 26.5) * mm});
            skLineSegment(sketch, "E315", {"start": v(-13.51, 26.5) * mm, "end": v(-13.53, 26.58) * mm});
            skLineSegment(sketch, "E316", {"start": v(-13.53, 26.58) * mm, "end": v(-13.55, 26.66) * mm});
            skLineSegment(sketch, "E317", {"start": v(-13.55, 26.66) * mm, "end": v(-13.59, 26.74) * mm});
            skLineSegment(sketch, "E318", {"start": v(-13.59, 26.74) * mm, "end": v(-13.63, 26.82) * mm});
            skLineSegment(sketch, "E319", {"start": v(-13.63, 26.82) * mm, "end": v(-13.67, 26.9) * mm});
            skLineSegment(sketch, "E320", {"start": v(-13.67, 26.9) * mm, "end": v(-14.12, 27.94) * mm});
            skLineSegment(sketch, "E321", {"start": v(-14.12, 27.94) * mm, "end": v(-14.54, 29) * mm});
            skLineSegment(sketch, "E322", {"start": v(-14.54, 29) * mm, "end": v(-14.92, 30.05) * mm});
            skLineSegment(sketch, "E323", {"start": v(-14.92, 30.05) * mm, "end": v(-15.27, 31.12) * mm});
            skLineSegment(sketch, "E324", {"start": v(-15.27, 31.12) * mm, "end": v(-15.59, 32.2) * mm});
            skLineSegment(sketch, "E325", {"start": v(-15.59, 32.2) * mm, "end": v(-15.87, 33.3) * mm});
            skLineSegment(sketch, "E326", {"start": v(-15.87, 33.3) * mm, "end": v(-16.1, 34.4) * mm});
            skLineSegment(sketch, "E327", {"start": v(-16.1, 34.4) * mm, "end": v(-16.3, 35.53) * mm});
            skLineSegment(sketch, "E328", {"start": v(-16.3, 35.53) * mm, "end": v(-16.34, 35.7) * mm});
            skLineSegment(sketch, "E329", {"start": v(-16.34, 35.7) * mm, "end": v(-16.4, 35.84) * mm});
            skLineSegment(sketch, "E330", {"start": v(-16.4, 35.84) * mm, "end": v(-16.46, 35.98) * mm});
            skLineSegment(sketch, "E331", {"start": v(-16.46, 35.98) * mm, "end": v(-16.53, 36.1) * mm});
            skLineSegment(sketch, "E332", {"start": v(-16.53, 36.1) * mm, "end": v(-16.63, 36.22) * mm});
            skLineSegment(sketch, "E333", {"start": v(-16.63, 36.22) * mm, "end": v(-16.74, 36.33) * mm});
            skLineSegment(sketch, "E334", {"start": v(-16.74, 36.33) * mm, "end": v(-16.87, 36.43) * mm});
            skLineSegment(sketch, "E335", {"start": v(-16.87, 36.43) * mm, "end": v(-17.02, 36.53) * mm});
            skLineSegment(sketch, "E336", {"start": v(-17.02, 36.53) * mm, "end": v(-17.64, 36.91) * mm});
            skLineSegment(sketch, "E337", {"start": v(-17.64, 36.91) * mm, "end": v(-18.25, 37.32) * mm});
            skLineSegment(sketch, "E338", {"start": v(-18.25, 37.32) * mm, "end": v(-18.84, 37.74) * mm});
            skLineSegment(sketch, "E339", {"start": v(-18.84, 37.74) * mm, "end": v(-19.42, 38.19) * mm});
            skLineSegment(sketch, "E340", {"start": v(-19.42, 38.19) * mm, "end": v(-19.98, 38.64) * mm});
            skLineSegment(sketch, "E341", {"start": v(-19.98, 38.64) * mm, "end": v(-20.54, 39.11) * mm});
            skLineSegment(sketch, "E342", {"start": v(-20.54, 39.11) * mm, "end": v(-21.1, 39.6) * mm});
            skLineSegment(sketch, "E343", {"start": v(-21.1, 39.6) * mm, "end": v(-21.64, 40.07) * mm});
            skLineSegment(sketch, "E344", {"start": v(-21.64, 40.07) * mm, "end": v(-22.63, 40.97) * mm});
            skLineSegment(sketch, "E345", {"start": v(-22.63, 40.97) * mm, "end": v(-23.61, 41.87) * mm});
            skLineSegment(sketch, "E346", {"start": v(-23.61, 41.87) * mm, "end": v(-24.58, 42.8) * mm});
            skLineSegment(sketch, "E347", {"start": v(-24.58, 42.8) * mm, "end": v(-25.52, 43.74) * mm});
            skLineSegment(sketch, "E348", {"start": v(-25.52, 43.74) * mm, "end": v(-26.43, 44.7) * mm});
            skLineSegment(sketch, "E349", {"start": v(-26.43, 44.7) * mm, "end": v(-27.32, 45.7) * mm});
            skLineSegment(sketch, "E350", {"start": v(-27.32, 45.7) * mm, "end": v(-28.17, 46.72) * mm});
            skLineSegment(sketch, "E351", {"start": v(-28.17, 46.72) * mm, "end": v(-28.99, 47.78) * mm});
            skLineSegment(sketch, "E352", {"start": v(-28.99, 47.78) * mm, "end": v(-29.08, 47.91) * mm});
            skLineSegment(sketch, "E353", {"start": v(-29.08, 47.91) * mm, "end": v(-29.17, 48.05) * mm});
            skLineSegment(sketch, "E354", {"start": v(-29.17, 48.05) * mm, "end": v(-29.25, 48.19) * mm});
            skLineSegment(sketch, "E355", {"start": v(-29.25, 48.19) * mm, "end": v(-29.34, 48.33) * mm});
            skLineSegment(sketch, "E356", {"start": v(-29.34, 48.33) * mm, "end": v(-29.42, 48.47) * mm});
            skLineSegment(sketch, "E357", {"start": v(-29.42, 48.47) * mm, "end": v(-29.5, 48.61) * mm});
            skLineSegment(sketch, "E358", {"start": v(-29.5, 48.61) * mm, "end": v(-29.57, 48.76) * mm});
            skLineSegment(sketch, "E359", {"start": v(-29.57, 48.76) * mm, "end": v(-29.65, 48.9) * mm});
            skLineSegment(sketch, "E360", {"start": v(-29.65, 48.9) * mm, "end": v(-29.7, 48.98) * mm});
            skLineSegment(sketch, "E361", {"start": v(-29.7, 48.98) * mm, "end": v(-29.72, 49.06) * mm});
            skLineSegment(sketch, "E362", {"start": v(-29.72, 49.06) * mm, "end": v(-29.75, 49.14) * mm});
            skLineSegment(sketch, "E363", {"start": v(-29.75, 49.14) * mm, "end": v(-29.77, 49.23) * mm});
            skLineSegment(sketch, "E364", {"start": v(-29.77, 49.23) * mm, "end": v(-29.77, 49.31) * mm});
            skLineSegment(sketch, "E365", {"start": v(-29.77, 49.31) * mm, "end": v(-29.75, 49.4) * mm});
            skLineSegment(sketch, "E366", {"start": v(-29.75, 49.4) * mm, "end": v(-29.72, 49.47) * mm});
            skLineSegment(sketch, "E367", {"start": v(-29.72, 49.47) * mm, "end": v(-29.67, 49.55) * mm});
            skLineSegment(sketch, "E368", {"start": v(-29.67, 49.55) * mm, "end": v(-29.6, 49.63) * mm});
            skLineSegment(sketch, "E369", {"start": v(-29.6, 49.63) * mm, "end": v(-29.5, 49.67) * mm});
            skLineSegment(sketch, "E370", {"start": v(-29.5, 49.67) * mm, "end": v(-29.42, 49.7) * mm});
            skLineSegment(sketch, "E371", {"start": v(-29.42, 49.7) * mm, "end": v(-29.33, 49.7) * mm});
            skLineSegment(sketch, "E372", {"start": v(-29.33, 49.7) * mm, "end": v(-29.23, 49.7) * mm});
            skLineSegment(sketch, "E373", {"start": v(-29.23, 49.7) * mm, "end": v(-29.14, 49.67) * mm});
            skLineSegment(sketch, "E374", {"start": v(-29.14, 49.67) * mm, "end": v(-29.05, 49.64) * mm});
            skLineSegment(sketch, "E375", {"start": v(-29.05, 49.64) * mm, "end": v(-28.96, 49.6) * mm});
            skLineSegment(sketch, "E376", {"start": v(-28.96, 49.6) * mm, "end": v(-28.7, 49.5) * mm});
            skLineSegment(sketch, "E377", {"start": v(-28.7, 49.5) * mm, "end": v(-28.46, 49.39) * mm});
            skLineSegment(sketch, "E378", {"start": v(-28.46, 49.39) * mm, "end": v(-28.23, 49.26) * mm});
            skLineSegment(sketch, "E379", {"start": v(-28.23, 49.26) * mm, "end": v(-28, 49.13) * mm});
            skLineSegment(sketch, "E380", {"start": v(-28, 49.13) * mm, "end": v(-27.77, 48.99) * mm});
            skLineSegment(sketch, "E381", {"start": v(-27.77, 48.99) * mm, "end": v(-27.54, 48.84) * mm});
            skLineSegment(sketch, "E382", {"start": v(-27.54, 48.84) * mm, "end": v(-27.32, 48.69) * mm});
            skLineSegment(sketch, "E383", {"start": v(-27.32, 48.69) * mm, "end": v(-27.1, 48.53) * mm});
            skLineSegment(sketch, "E384", {"start": v(-27.1, 48.53) * mm, "end": v(-25.7, 47.46) * mm});
            skLineSegment(sketch, "E385", {"start": v(-25.7, 47.46) * mm, "end": v(-24.32, 46.35) * mm});
            skLineSegment(sketch, "E386", {"start": v(-24.32, 46.35) * mm, "end": v(-22.99, 45.2) * mm});
            skLineSegment(sketch, "E387", {"start": v(-22.99, 45.2) * mm, "end": v(-21.7, 44) * mm});
            skLineSegment(sketch, "E388", {"start": v(-21.7, 44) * mm, "end": v(-20.43, 42.77) * mm});
            skLineSegment(sketch, "E389", {"start": v(-20.43, 42.77) * mm, "end": v(-19.2, 41.5) * mm});
            skLineSegment(sketch, "E390", {"start": v(-19.2, 41.5) * mm, "end": v(-18.01, 40.2) * mm});
            skLineSegment(sketch, "E391", {"start": v(-18.01, 40.2) * mm, "end": v(-16.85, 38.87) * mm});
            skLineSegment(sketch, "E392", {"start": v(-16.85, 38.87) * mm, "end": v(-16.76, 38.75) * mm});
            skLineSegment(sketch, "E393", {"start": v(-16.76, 38.75) * mm, "end": v(-16.66, 38.65) * mm});
            skLineSegment(sketch, "E394", {"start": v(-16.66, 38.65) * mm, "end": v(-16.57, 38.54) * mm});
            skLineSegment(sketch, "E395", {"start": v(-16.57, 38.54) * mm, "end": v(-16.47, 38.45) * mm});
            skLineSegment(sketch, "E396", {"start": v(-16.47, 38.45) * mm, "end": v(-16.36, 38.36) * mm});
            skLineSegment(sketch, "E397", {"start": v(-16.36, 38.36) * mm, "end": v(-16.23, 38.3) * mm});
            skLineSegment(sketch, "E398", {"start": v(-16.23, 38.3) * mm, "end": v(-16.08, 38.24) * mm});
            skLineSegment(sketch, "E399", {"start": v(-16.08, 38.24) * mm, "end": v(-15.91, 38.2) * mm});
            skLineSegment(sketch, "E400", {"start": v(-15.91, 38.2) * mm, "end": v(-15.72, 38.14) * mm});
            skLineSegment(sketch, "E401", {"start": v(-15.72, 38.14) * mm, "end": v(-15.55, 38.04) * mm});
            skLineSegment(sketch, "E402", {"start": v(-15.55, 38.04) * mm, "end": v(-15.4, 37.91) * mm});
            skLineSegment(sketch, "E403", {"start": v(-15.4, 37.91) * mm, "end": v(-15.28, 37.76) * mm});
            skLineSegment(sketch, "E404", {"start": v(-15.28, 37.76) * mm, "end": v(-15.17, 37.58) * mm});
            skLineSegment(sketch, "E405", {"start": v(-15.17, 37.58) * mm, "end": v(-15.07, 37.4) * mm});
            skLineSegment(sketch, "E406", {"start": v(-15.07, 37.4) * mm, "end": v(-14.97, 37.21) * mm});
            skLineSegment(sketch, "E407", {"start": v(-14.97, 37.21) * mm, "end": v(-14.88, 37.03) * mm});
            skLineSegment(sketch, "E408", {"start": v(-14.88, 37.03) * mm, "end": v(-14.46, 36.2) * mm});
            skLineSegment(sketch, "E409", {"start": v(-14.46, 36.2) * mm, "end": v(-14.08, 35.35) * mm});
            skLineSegment(sketch, "E410", {"start": v(-14.08, 35.35) * mm, "end": v(-13.72, 34.5) * mm});
            skLineSegment(sketch, "E411", {"start": v(-13.72, 34.5) * mm, "end": v(-13.4, 33.62) * mm});
            skLineSegment(sketch, "E412", {"start": v(-13.4, 33.62) * mm, "end": v(-13.1, 32.74) * mm});
            skLineSegment(sketch, "E413", {"start": v(-13.1, 32.74) * mm, "end": v(-12.83, 31.85) * mm});
            skLineSegment(sketch, "E414", {"start": v(-12.83, 31.85) * mm, "end": v(-12.58, 30.96) * mm});
            skLineSegment(sketch, "E415", {"start": v(-12.58, 30.96) * mm, "end": v(-12.34, 30.06) * mm});
            skLineSegment(sketch, "E416", {"start": v(-12.34, 30.06) * mm, "end": v(-12.27, 29.78) * mm});
            skLineSegment(sketch, "E417", {"start": v(-12.27, 29.78) * mm, "end": v(-12.2, 29.5) * mm});
            skLineSegment(sketch, "E418", {"start": v(-12.2, 29.5) * mm, "end": v(-12.15, 29.22) * mm});
            skLineSegment(sketch, "E419", {"start": v(-12.15, 29.22) * mm, "end": v(-12.09, 28.94) * mm});
            skLineSegment(sketch, "E420", {"start": v(-12.09, 28.94) * mm, "end": v(-12.03, 28.65) * mm});
            skLineSegment(sketch, "E421", {"start": v(-12.03, 28.65) * mm, "end": v(-11.98, 28.37) * mm});
            skLineSegment(sketch, "E422", {"start": v(-11.98, 28.37) * mm, "end": v(-11.93, 28.09) * mm});
            skLineSegment(sketch, "E423", {"start": v(-11.93, 28.09) * mm, "end": v(-11.88, 27.8) * mm});
            skLineSegment(sketch, "E424", {"start": v(-11.88, 27.8) * mm, "end": v(-11.84, 27.64) * mm});
            skLineSegment(sketch, "E425", {"start": v(-11.84, 27.64) * mm, "end": v(-11.79, 27.5) * mm});
            skLineSegment(sketch, "E426", {"start": v(-11.79, 27.5) * mm, "end": v(-11.72, 27.38) * mm});
            skLineSegment(sketch, "E427", {"start": v(-11.72, 27.38) * mm, "end": v(-11.63, 27.3) * mm});
            skLineSegment(sketch, "E428", {"start": v(-11.63, 27.3) * mm, "end": v(-11.52, 27.24) * mm});
            skLineSegment(sketch, "E429", {"start": v(-11.52, 27.24) * mm, "end": v(-11.4, 27.2) * mm});
            skLineSegment(sketch, "E430", {"start": v(-11.4, 27.2) * mm, "end": v(-11.25, 27.2) * mm});
            skLineSegment(sketch, "E431", {"start": v(-11.25, 27.2) * mm, "end": v(-11.09, 27.22) * mm});
            skLineSegment(sketch, "E432", {"start": v(-11.09, 27.22) * mm, "end": v(-10.76, 27.27) * mm});
            skLineSegment(sketch, "E433", {"start": v(-10.76, 27.27) * mm, "end": v(-10.42, 27.3) * mm});
            skLineSegment(sketch, "E434", {"start": v(-10.42, 27.3) * mm, "end": v(-10.09, 27.33) * mm});
            skLineSegment(sketch, "E435", {"start": v(-10.09, 27.33) * mm, "end": v(-9.75, 27.34) * mm});
            skLineSegment(sketch, "E436", {"start": v(-9.75, 27.34) * mm, "end": v(-9.42, 27.34) * mm});
            skLineSegment(sketch, "E437", {"start": v(-9.42, 27.34) * mm, "end": v(-9.08, 27.33) * mm});
            skLineSegment(sketch, "E438", {"start": v(-9.08, 27.33) * mm, "end": v(-8.75, 27.3) * mm});
            skLineSegment(sketch, "E439", {"start": v(-8.75, 27.3) * mm, "end": v(-8.41, 27.28) * mm});
            skLineSegment(sketch, "E440", {"start": v(-8.41, 27.28) * mm, "end": v(-8.3, 27.27) * mm});
            skLineSegment(sketch, "E441", {"start": v(-8.3, 27.27) * mm, "end": v(-8.19, 27.28) * mm});
            skLineSegment(sketch, "E442", {"start": v(-8.19, 27.28) * mm, "end": v(-8.09, 27.3) * mm});
            skLineSegment(sketch, "E443", {"start": v(-8.09, 27.3) * mm, "end": v(-8, 27.33) * mm});
            skLineSegment(sketch, "E444", {"start": v(-8, 27.33) * mm, "end": v(-7.92, 27.38) * mm});
            skLineSegment(sketch, "E445", {"start": v(-7.92, 27.38) * mm, "end": v(-7.84, 27.44) * mm});
            skLineSegment(sketch, "E446", {"start": v(-7.84, 27.44) * mm, "end": v(-7.77, 27.52) * mm});
            skLineSegment(sketch, "E447", {"start": v(-7.77, 27.52) * mm, "end": v(-7.71, 27.62) * mm});
            skLineSegment(sketch, "E448", {"start": v(-7.71, 27.62) * mm, "end": v(-7.45, 28.07) * mm});
            skLineSegment(sketch, "E449", {"start": v(-7.45, 28.07) * mm, "end": v(-7.2, 28.53) * mm});
            skLineSegment(sketch, "E450", {"start": v(-7.2, 28.53) * mm, "end": v(-7, 29) * mm});
            skLineSegment(sketch, "E451", {"start": v(-7, 29) * mm, "end": v(-6.82, 29.47) * mm});
            skLineSegment(sketch, "E452", {"start": v(-6.82, 29.47) * mm, "end": v(-6.7, 29.96) * mm});
            skLineSegment(sketch, "E453", {"start": v(-6.7, 29.96) * mm, "end": v(-6.62, 30.48) * mm});
            skLineSegment(sketch, "E454", {"start": v(-6.62, 30.48) * mm, "end": v(-6.62, 31.01) * mm});
            skLineSegment(sketch, "E455", {"start": v(-6.62, 31.01) * mm, "end": v(-6.69, 31.58) * mm});
            skLineSegment(sketch, "E456", {"start": v(-6.69, 31.58) * mm, "end": v(-6.76, 32.65) * mm});
            skLineSegment(sketch, "E457", {"start": v(-6.76, 32.65) * mm, "end": v(-6.59, 33.67) * mm});
            skLineSegment(sketch, "E458", {"start": v(-6.59, 33.67) * mm, "end": v(-6.2, 34.6) * mm});
            skLineSegment(sketch, "E459", {"start": v(-6.2, 34.6) * mm, "end": v(-5.63, 35.43) * mm});
            skLineSegment(sketch, "E460", {"start": v(-5.63, 35.43) * mm, "end": v(-4.89, 36.11) * mm});
            skLineSegment(sketch, "E461", {"start": v(-4.89, 36.11) * mm, "end": v(-4, 36.63) * mm});
            skLineSegment(sketch, "E462", {"start": v(-4, 36.63) * mm, "end": v(-3.02, 36.95) * mm});
            skLineSegment(sketch, "E463", {"start": v(-3.02, 36.95) * mm, "end": v(-1.95, 37.05) * mm});
            skLineSegment(sketch, "E464", {"start": v(-1.95, 37.05) * mm, "end": v(-1.32, 36.99) * mm});
            skLineSegment(sketch, "E465", {"start": v(-1.32, 36.99) * mm, "end": v(-0.72, 36.81) * mm});
            skLineSegment(sketch, "E466", {"start": v(-0.72, 36.81) * mm, "end": v(-0.16, 36.54) * mm});
            skLineSegment(sketch, "E467", {"start": v(-0.16, 36.54) * mm, "end": v(0.34, 36.18) * mm});
            skLineSegment(sketch, "E468", {"start": v(0.34, 36.18) * mm, "end": v(0.79, 35.74) * mm});
            skLineSegment(sketch, "E469", {"start": v(0.79, 35.74) * mm, "end": v(1.15, 35.23) * mm});
            skLineSegment(sketch, "E470", {"start": v(1.15, 35.23) * mm, "end": v(1.43, 34.65) * mm});
            skLineSegment(sketch, "E471", {"start": v(1.43, 34.65) * mm, "end": v(1.6, 34.01) * mm});
            skLineSegment(sketch, "E472", {"start": v(1.6, 34.01) * mm, "end": v(1.67, 33.76) * mm});
            skLineSegment(sketch, "E473", {"start": v(1.67, 33.76) * mm, "end": v(1.76, 33.56) * mm});
            skLineSegment(sketch, "E474", {"start": v(1.76, 33.56) * mm, "end": v(1.88, 33.4) * mm});
            skLineSegment(sketch, "E475", {"start": v(1.88, 33.4) * mm, "end": v(2.02, 33.29) * mm});
            skLineSegment(sketch, "E476", {"start": v(2.02, 33.29) * mm, "end": v(2.17, 33.2) * mm});
            skLineSegment(sketch, "E477", {"start": v(2.17, 33.2) * mm, "end": v(2.35, 33.13) * mm});
            skLineSegment(sketch, "E478", {"start": v(2.35, 33.13) * mm, "end": v(2.55, 33.08) * mm});
            skLineSegment(sketch, "E479", {"start": v(2.55, 33.08) * mm, "end": v(2.76, 33.04) * mm});
            skLineSegment(sketch, "E480", {"start": v(2.76, 33.04) * mm, "end": v(2.96, 33.02) * mm});
            skLineSegment(sketch, "E481", {"start": v(2.96, 33.02) * mm, "end": v(3.12, 33.06) * mm});
            skLineSegment(sketch, "E482", {"start": v(3.12, 33.06) * mm, "end": v(3.24, 33.14) * mm});
            skLineSegment(sketch, "E483", {"start": v(3.24, 33.14) * mm, "end": v(3.33, 33.24) * mm});
            skLineSegment(sketch, "E484", {"start": v(3.33, 33.24) * mm, "end": v(3.4, 33.37) * mm});
            skLineSegment(sketch, "E485", {"start": v(3.4, 33.37) * mm, "end": v(3.45, 33.51) * mm});
            skLineSegment(sketch, "E486", {"start": v(3.45, 33.51) * mm, "end": v(3.5, 33.65) * mm});
            skLineSegment(sketch, "E487", {"start": v(3.5, 33.65) * mm, "end": v(3.54, 33.78) * mm});
            skLineSegment(sketch, "E488", {"start": v(3.54, 33.78) * mm, "end": v(3.97, 34.84) * mm});
            skLineSegment(sketch, "E489", {"start": v(3.97, 34.84) * mm, "end": v(4.32, 35.9) * mm});
            skLineSegment(sketch, "E490", {"start": v(4.32, 35.9) * mm, "end": v(4.58, 36.96) * mm});
            skLineSegment(sketch, "E491", {"start": v(4.58, 36.96) * mm, "end": v(4.75, 38.04) * mm});
            skLineSegment(sketch, "E492", {"start": v(4.75, 38.04) * mm, "end": v(4.82, 39.13) * mm});
            skLineSegment(sketch, "E493", {"start": v(4.82, 39.13) * mm, "end": v(4.78, 40.23) * mm});
            skLineSegment(sketch, "E494", {"start": v(4.78, 40.23) * mm, "end": v(4.62, 41.33) * mm});
            skLineSegment(sketch, "E495", {"start": v(4.62, 41.33) * mm, "end": v(4.35, 42.45) * mm});
            skLineSegment(sketch, "E496", {"start": v(4.35, 42.45) * mm, "end": v(4.08, 43.24) * mm});
            skLineSegment(sketch, "E497", {"start": v(4.08, 43.24) * mm, "end": v(3.74, 43.98) * mm});
            skLineSegment(sketch, "E498", {"start": v(3.74, 43.98) * mm, "end": v(3.34, 44.68) * mm});
            skLineSegment(sketch, "E499", {"start": v(3.34, 44.68) * mm, "end": v(2.89, 45.34) * mm});
            skLineSegment(sketch, "E500", {"start": v(2.89, 45.34) * mm, "end": v(2.38, 45.96) * mm});
            skLineSegment(sketch, "E501", {"start": v(2.38, 45.96) * mm, "end": v(1.81, 46.54) * mm});
            skLineSegment(sketch, "E502", {"start": v(1.81, 46.54) * mm, "end": v(1.2, 47.09) * mm});
            skLineSegment(sketch, "E503", {"start": v(1.2, 47.09) * mm, "end": v(0.54, 47.6) * mm});
            skLineSegment(sketch, "E504", {"start": v(0.54, 47.6) * mm, "end": v(0.5, 47.62) * mm});
            skLineSegment(sketch, "E505", {"start": v(0.5, 47.62) * mm, "end": v(0.47, 47.65) * mm});
            skLineSegment(sketch, "E506", {"start": v(0.47, 47.65) * mm, "end": v(0.43, 47.68) * mm});
            skLineSegment(sketch, "E507", {"start": v(0.43, 47.68) * mm, "end": v(0.39, 47.7) * mm});
            skLineSegment(sketch, "E508", {"start": v(0.39, 47.7) * mm, "end": v(0.35, 47.73) * mm});
            skLineSegment(sketch, "E509", {"start": v(0.35, 47.73) * mm, "end": v(0.3, 47.76) * mm});
            skLineSegment(sketch, "E510", {"start": v(0.3, 47.76) * mm, "end": v(0.27, 47.78) * mm});
            skLineSegment(sketch, "E511", {"start": v(0.27, 47.78) * mm, "end": v(0.23, 47.8) * mm});
            skLineSegment(sketch, "E512", {"start": v(0.23, 47.8) * mm, "end": v(0.12, 47.88) * mm});
            skLineSegment(sketch, "E513", {"start": v(0.12, 47.88) * mm, "end": v(0.03, 47.95) * mm});
            skLineSegment(sketch, "E514", {"start": v(0.03, 47.95) * mm, "end": v(-0.05, 48.02) * mm});
            skLineSegment(sketch, "E515", {"start": v(-0.05, 48.02) * mm, "end": v(-0.11, 48.1) * mm});
            skLineSegment(sketch, "E516", {"start": v(-0.11, 48.1) * mm, "end": v(-0.14, 48.2) * mm});
            skLineSegment(sketch, "E517", {"start": v(-0.14, 48.2) * mm, "end": v(-0.15, 48.3) * mm});
            skLineSegment(sketch, "E518", {"start": v(-0.15, 48.3) * mm, "end": v(-0.12, 48.41) * mm});
            skLineSegment(sketch, "E519", {"start": v(-0.12, 48.41) * mm, "end": v(-0.04, 48.54) * mm});
            skLineSegment(sketch, "E520", {"start": v(-0.04, 48.54) * mm, "end": v(0.05, 48.65) * mm});
            skLineSegment(sketch, "E521", {"start": v(0.05, 48.65) * mm, "end": v(0.14, 48.7) * mm});
            skLineSegment(sketch, "E522", {"start": v(0.14, 48.7) * mm, "end": v(0.24, 48.73) * mm});
            skLineSegment(sketch, "E523", {"start": v(0.24, 48.73) * mm, "end": v(0.33, 48.72) * mm});
            skLineSegment(sketch, "E524", {"start": v(0.33, 48.72) * mm, "end": v(0.42, 48.68) * mm});
            skLineSegment(sketch, "E525", {"start": v(0.42, 48.68) * mm, "end": v(0.51, 48.63) * mm});
            skLineSegment(sketch, "E526", {"start": v(0.51, 48.63) * mm, "end": v(0.6, 48.58) * mm});
            skLineSegment(sketch, "E527", {"start": v(0.6, 48.58) * mm, "end": v(0.68, 48.52) * mm});
            skLineSegment(sketch, "E528", {"start": v(0.68, 48.52) * mm, "end": v(1.6, 47.85) * mm});
            skLineSegment(sketch, "E529", {"start": v(1.6, 47.85) * mm, "end": v(2.44, 47.12) * mm});
            skLineSegment(sketch, "E530", {"start": v(2.44, 47.12) * mm, "end": v(3.19, 46.33) * mm});
            skLineSegment(sketch, "E531", {"start": v(3.19, 46.33) * mm, "end": v(3.84, 45.47) * mm});
            skLineSegment(sketch, "E532", {"start": v(3.84, 45.47) * mm, "end": v(4.4, 44.55) * mm});
            skLineSegment(sketch, "E533", {"start": v(4.4, 44.55) * mm, "end": v(4.85, 43.57) * mm});
            skLineSegment(sketch, "E534", {"start": v(4.85, 43.57) * mm, "end": v(5.2, 42.52) * mm});
            skLineSegment(sketch, "E535", {"start": v(5.2, 42.52) * mm, "end": v(5.47, 41.4) * mm});
            skLineSegment(sketch, "E536", {"start": v(5.47, 41.4) * mm, "end": v(5.6, 40.39) * mm});
            skLineSegment(sketch, "E537", {"start": v(5.6, 40.39) * mm, "end": v(5.66, 39.38) * mm});
            skLineSegment(sketch, "E538", {"start": v(5.66, 39.38) * mm, "end": v(5.63, 38.38) * mm});
            skLineSegment(sketch, "E539", {"start": v(5.63, 38.38) * mm, "end": v(5.52, 37.4) * mm});
            skLineSegment(sketch, "E540", {"start": v(5.52, 37.4) * mm, "end": v(5.34, 36.42) * mm});
            skLineSegment(sketch, "E541", {"start": v(5.34, 36.42) * mm, "end": v(5.08, 35.45) * mm});
            skLineSegment(sketch, "E542", {"start": v(5.08, 35.45) * mm, "end": v(4.75, 34.5) * mm});
            skLineSegment(sketch, "E543", {"start": v(4.75, 34.5) * mm, "end": v(4.35, 33.56) * mm});
            skLineSegment(sketch, "E544", {"start": v(4.35, 33.56) * mm, "end": v(4.26, 33.31) * mm});
            skLineSegment(sketch, "E545", {"start": v(4.26, 33.31) * mm, "end": v(4.2, 33.1) * mm});
            skLineSegment(sketch, "E546", {"start": v(4.2, 33.1) * mm, "end": v(4.19, 32.93) * mm});
            skLineSegment(sketch, "E547", {"start": v(4.19, 32.93) * mm, "end": v(4.22, 32.77) * mm});
            skLineSegment(sketch, "E548", {"start": v(4.22, 32.77) * mm, "end": v(4.3, 32.64) * mm});
            skLineSegment(sketch, "E549", {"start": v(4.3, 32.64) * mm, "end": v(4.44, 32.53) * mm});
            skLineSegment(sketch, "E550", {"start": v(4.44, 32.53) * mm, "end": v(4.62, 32.43) * mm});
            skLineSegment(sketch, "E551", {"start": v(4.62, 32.43) * mm, "end": v(4.86, 32.34) * mm});
            skLineSegment(sketch, "E552", {"start": v(4.86, 32.34) * mm, "end": v(5.32, 32.2) * mm});
            skLineSegment(sketch, "E553", {"start": v(5.32, 32.2) * mm, "end": v(5.77, 32.02) * mm});
            skLineSegment(sketch, "E554", {"start": v(5.77, 32.02) * mm, "end": v(6.2, 31.83) * mm});
            skLineSegment(sketch, "E555", {"start": v(6.2, 31.83) * mm, "end": v(6.64, 31.63) * mm});
            skLineSegment(sketch, "E556", {"start": v(6.64, 31.63) * mm, "end": v(7.07, 31.42) * mm});
            skLineSegment(sketch, "E557", {"start": v(7.07, 31.42) * mm, "end": v(7.5, 31.2) * mm});
            skLineSegment(sketch, "E558", {"start": v(7.5, 31.2) * mm, "end": v(7.91, 30.96) * mm});
            skLineSegment(sketch, "E559", {"start": v(7.91, 30.96) * mm, "end": v(8.33, 30.72) * mm});
            skLineSegment(sketch, "E560", {"start": v(8.33, 30.72) * mm, "end": v(8.5, 30.62) * mm});
            skLineSegment(sketch, "E561", {"start": v(8.5, 30.62) * mm, "end": v(8.66, 30.57) * mm});
            skLineSegment(sketch, "E562", {"start": v(8.66, 30.57) * mm, "end": v(8.8, 30.55) * mm});
            skLineSegment(sketch, "E563", {"start": v(8.8, 30.55) * mm, "end": v(8.92, 30.57) * mm});
            skLineSegment(sketch, "E564", {"start": v(8.92, 30.57) * mm, "end": v(9.03, 30.62) * mm});
            skLineSegment(sketch, "E565", {"start": v(9.03, 30.62) * mm, "end": v(9.13, 30.71) * mm});
            skLineSegment(sketch, "E566", {"start": v(9.13, 30.71) * mm, "end": v(9.24, 30.83) * mm});
            skLineSegment(sketch, "E567", {"start": v(9.24, 30.83) * mm, "end": v(9.35, 30.99) * mm});
            skLineSegment(sketch, "E568", {"start": v(9.35, 30.99) * mm, "end": v(10.14, 32.1) * mm});
            skLineSegment(sketch, "E569", {"start": v(10.14, 32.1) * mm, "end": v(11, 33.12) * mm});
            skLineSegment(sketch, "E570", {"start": v(11, 33.12) * mm, "end": v(11.93, 34.05) * mm});
            skLineSegment(sketch, "E571", {"start": v(11.93, 34.05) * mm, "end": v(12.94, 34.88) * mm});
            skLineSegment(sketch, "E572", {"start": v(12.94, 34.88) * mm, "end": v(14.02, 35.61) * mm});
            skLineSegment(sketch, "E573", {"start": v(14.02, 35.61) * mm, "end": v(15.17, 36.23) * mm});
            skLineSegment(sketch, "E574", {"start": v(15.17, 36.23) * mm, "end": v(16.42, 36.73) * mm});
            skLineSegment(sketch, "E575", {"start": v(16.42, 36.73) * mm, "end": v(17.75, 37.1) * mm});
            skLineSegment(sketch, "E576", {"start": v(17.75, 37.1) * mm, "end": v(18.34, 37.23) * mm});
            skLineSegment(sketch, "E577", {"start": v(18.34, 37.23) * mm, "end": v(18.93, 37.3) * mm});
            skLineSegment(sketch, "E578", {"start": v(18.93, 37.3) * mm, "end": v(19.52, 37.35) * mm});
            skLineSegment(sketch, "E579", {"start": v(19.52, 37.35) * mm, "end": v(20.1, 37.36) * mm});
            skLineSegment(sketch, "E580", {"start": v(20.1, 37.36) * mm, "end": v(20.7, 37.33) * mm});
            skLineSegment(sketch, "E581", {"start": v(20.7, 37.33) * mm, "end": v(21.28, 37.26) * mm});
            skLineSegment(sketch, "E582", {"start": v(21.28, 37.26) * mm, "end": v(21.87, 37.16) * mm});
            skLineSegment(sketch, "E583", {"start": v(21.87, 37.16) * mm, "end": v(22.46, 37.03) * mm});
            skLineSegment(sketch, "E584", {"start": v(22.46, 37.03) * mm, "end": v(22.56, 37) * mm});
            skLineSegment(sketch, "E585", {"start": v(22.56, 37) * mm, "end": v(22.67, 36.98) * mm});
            skLineSegment(sketch, "E586", {"start": v(22.67, 36.98) * mm, "end": v(22.79, 36.95) * mm});
            skLineSegment(sketch, "E587", {"start": v(22.79, 36.95) * mm, "end": v(22.89, 36.9) * mm});
            skLineSegment(sketch, "E588", {"start": v(22.89, 36.9) * mm, "end": v(22.97, 36.84) * mm});
            skLineSegment(sketch, "E589", {"start": v(22.97, 36.84) * mm, "end": v(23.03, 36.76) * mm});
            skLineSegment(sketch, "E590", {"start": v(23.03, 36.76) * mm, "end": v(23.06, 36.64) * mm});
            skLineSegment(sketch, "E591", {"start": v(23.06, 36.64) * mm, "end": v(23.05, 36.5) * mm});
            skLineSegment(sketch, "E592", {"start": v(23.05, 36.5) * mm, "end": v(23, 36.34) * mm});
            skLineSegment(sketch, "E593", {"start": v(23, 36.34) * mm, "end": v(22.93, 36.23) * mm});
            skLineSegment(sketch, "E594", {"start": v(22.93, 36.23) * mm, "end": v(22.84, 36.17) * mm});
            skLineSegment(sketch, "E595", {"start": v(22.84, 36.17) * mm, "end": v(22.74, 36.14) * mm});
            skLineSegment(sketch, "E596", {"start": v(22.74, 36.14) * mm, "end": v(22.63, 36.14) * mm});
            skLineSegment(sketch, "E597", {"start": v(22.63, 36.14) * mm, "end": v(22.5, 36.15) * mm});
            skLineSegment(sketch, "E598", {"start": v(22.5, 36.15) * mm, "end": v(22.38, 36.18) * mm});
            skLineSegment(sketch, "E599", {"start": v(22.38, 36.18) * mm, "end": v(22.26, 36.21) * mm});
            skLineSegment(sketch, "E600", {"start": v(22.26, 36.21) * mm, "end": v(20.7, 36.46) * mm});
            skLineSegment(sketch, "E601", {"start": v(20.7, 36.46) * mm, "end": v(19.2, 36.47) * mm});
            skLineSegment(sketch, "E602", {"start": v(19.2, 36.47) * mm, "end": v(17.78, 36.27) * mm});
            skLineSegment(sketch, "E603", {"start": v(17.78, 36.27) * mm, "end": v(16.43, 35.87) * mm});
            skLineSegment(sketch, "E604", {"start": v(16.43, 35.87) * mm, "end": v(15.15, 35.28) * mm});
            skLineSegment(sketch, "E605", {"start": v(15.15, 35.28) * mm, "end": v(13.92, 34.53) * mm});
            skLineSegment(sketch, "E606", {"start": v(13.92, 34.53) * mm, "end": v(12.75, 33.61) * mm});
            skLineSegment(sketch, "E607", {"start": v(12.75, 33.61) * mm, "end": v(11.63, 32.55) * mm});
            skLineSegment(sketch, "E608", {"start": v(11.63, 32.55) * mm, "end": v(11.43, 32.34) * mm});
            skLineSegment(sketch, "E609", {"start": v(11.43, 32.34) * mm, "end": v(11.23, 32.11) * mm});
            skLineSegment(sketch, "E610", {"start": v(11.23, 32.11) * mm, "end": v(11.05, 31.88) * mm});
            skLineSegment(sketch, "E611", {"start": v(11.05, 31.88) * mm, "end": v(10.86, 31.65) * mm});
            skLineSegment(sketch, "E612", {"start": v(10.86, 31.65) * mm, "end": v(10.68, 31.41) * mm});
            skLineSegment(sketch, "E613", {"start": v(10.68, 31.41) * mm, "end": v(10.5, 31.17) * mm});
            skLineSegment(sketch, "E614", {"start": v(10.5, 31.17) * mm, "end": v(10.34, 30.93) * mm});
            skLineSegment(sketch, "E615", {"start": v(10.34, 30.93) * mm, "end": v(10.17, 30.68) * mm});
            skLineSegment(sketch, "E616", {"start": v(10.17, 30.68) * mm, "end": v(10.09, 30.58) * mm});
            skLineSegment(sketch, "E617", {"start": v(10.09, 30.58) * mm, "end": v(10, 30.48) * mm});
            skLineSegment(sketch, "E618", {"start": v(10, 30.48) * mm, "end": v(9.9, 30.38) * mm});
            skLineSegment(sketch, "E619", {"start": v(9.9, 30.38) * mm, "end": v(9.82, 30.27) * mm});
            skLineSegment(sketch, "E620", {"start": v(9.82, 30.27) * mm, "end": v(9.76, 30.15) * mm});
            skLineSegment(sketch, "E621", {"start": v(9.76, 30.15) * mm, "end": v(9.74, 30.03) * mm});
            skLineSegment(sketch, "E622", {"start": v(9.74, 30.03) * mm, "end": v(9.77, 29.9) * mm});
            skLineSegment(sketch, "E623", {"start": v(9.77, 29.9) * mm, "end": v(9.87, 29.77) * mm});
            skLineSegment(sketch, "E624", {"start": v(9.87, 29.77) * mm, "end": v(10, 29.63) * mm});
            skLineSegment(sketch, "E625", {"start": v(10, 29.63) * mm, "end": v(10.15, 29.49) * mm});
            skLineSegment(sketch, "E626", {"start": v(10.15, 29.49) * mm, "end": v(10.3, 29.36) * mm});
            skLineSegment(sketch, "E627", {"start": v(10.3, 29.36) * mm, "end": v(10.48, 29.25) * mm});
            skLineSegment(sketch, "E628", {"start": v(10.48, 29.25) * mm, "end": v(10.66, 29.18) * mm});
            skLineSegment(sketch, "E629", {"start": v(10.66, 29.18) * mm, "end": v(10.86, 29.14) * mm});
            skLineSegment(sketch, "E630", {"start": v(10.86, 29.14) * mm, "end": v(11.08, 29.16) * mm});
            skLineSegment(sketch, "E631", {"start": v(11.08, 29.16) * mm, "end": v(11.33, 29.24) * mm});
            skLineSegment(sketch, "E632", {"start": v(11.33, 29.24) * mm, "end": v(11.56, 29.33) * mm});
            skLineSegment(sketch, "E633", {"start": v(11.56, 29.33) * mm, "end": v(11.8, 29.4) * mm});
            skLineSegment(sketch, "E634", {"start": v(11.8, 29.4) * mm, "end": v(12.04, 29.46) * mm});
            skLineSegment(sketch, "E635", {"start": v(12.04, 29.46) * mm, "end": v(12.28, 29.5) * mm});
            skLineSegment(sketch, "E636", {"start": v(12.28, 29.5) * mm, "end": v(12.53, 29.52) * mm});
            skLineSegment(sketch, "E637", {"start": v(12.53, 29.52) * mm, "end": v(12.78, 29.52) * mm});
            skLineSegment(sketch, "E638", {"start": v(12.78, 29.52) * mm, "end": v(13.03, 29.5) * mm});
            skLineSegment(sketch, "E639", {"start": v(13.03, 29.5) * mm, "end": v(13.28, 29.46) * mm});
            skLineSegment(sketch, "E640", {"start": v(13.28, 29.46) * mm, "end": v(14.15, 29.2) * mm});
            skLineSegment(sketch, "E641", {"start": v(14.15, 29.2) * mm, "end": v(14.9, 28.78) * mm});
            skLineSegment(sketch, "E642", {"start": v(14.9, 28.78) * mm, "end": v(15.53, 28.24) * mm});
            skLineSegment(sketch, "E643", {"start": v(15.53, 28.24) * mm, "end": v(16.03, 27.57) * mm});
            skLineSegment(sketch, "E644", {"start": v(16.03, 27.57) * mm, "end": v(16.38, 26.82) * mm});
            skLineSegment(sketch, "E645", {"start": v(16.38, 26.82) * mm, "end": v(16.58, 25.98) * mm});
            skLineSegment(sketch, "E646", {"start": v(16.58, 25.98) * mm, "end": v(16.6, 25.1) * mm});
            skLineSegment(sketch, "E647", {"start": v(16.6, 25.1) * mm, "end": v(16.46, 24.16) * mm});
            skLineSegment(sketch, "E648", {"start": v(16.46, 24.16) * mm, "end": v(16.33, 23.73) * mm});
            skLineSegment(sketch, "E649", {"start": v(16.33, 23.73) * mm, "end": v(16.17, 23.33) * mm});
            skLineSegment(sketch, "E650", {"start": v(16.17, 23.33) * mm, "end": v(15.99, 22.94) * mm});
            skLineSegment(sketch, "E651", {"start": v(15.99, 22.94) * mm, "end": v(15.77, 22.58) * mm});
            skLineSegment(sketch, "E652", {"start": v(15.77, 22.58) * mm, "end": v(15.52, 22.23) * mm});
            skLineSegment(sketch, "E653", {"start": v(15.52, 22.23) * mm, "end": v(15.23, 21.92) * mm});
            skLineSegment(sketch, "E654", {"start": v(15.23, 21.92) * mm, "end": v(14.91, 21.63) * mm});
            skLineSegment(sketch, "E655", {"start": v(14.91, 21.63) * mm, "end": v(14.56, 21.36) * mm});
            skLineSegment(sketch, "E656", {"start": v(14.56, 21.36) * mm, "end": v(14.04, 20.98) * mm});
            skLineSegment(sketch, "E657", {"start": v(14.04, 20.98) * mm, "end": v(13.58, 20.55) * mm});
            skLineSegment(sketch, "E658", {"start": v(13.58, 20.55) * mm, "end": v(13.18, 20.1) * mm});
            skLineSegment(sketch, "E659", {"start": v(13.18, 20.1) * mm, "end": v(12.8, 19.6) * mm});
            skLineSegment(sketch, "E660", {"start": v(12.8, 19.6) * mm, "end": v(12.47, 19.08) * mm});
            skLineSegment(sketch, "E661", {"start": v(12.47, 19.08) * mm, "end": v(12.16, 18.55) * mm});
            skLineSegment(sketch, "E662", {"start": v(12.16, 18.55) * mm, "end": v(11.87, 18) * mm});
            skLineSegment(sketch, "E663", {"start": v(11.87, 18) * mm, "end": v(11.59, 17.45) * mm});
            skLineSegment(sketch, "E664", {"start": v(11.59, 17.45) * mm, "end": v(11.54, 17.32) * mm});
            skLineSegment(sketch, "E665", {"start": v(11.54, 17.32) * mm, "end": v(11.5, 17.2) * mm});
            skLineSegment(sketch, "E666", {"start": v(11.5, 17.2) * mm, "end": v(11.5, 17.1) * mm});
            skLineSegment(sketch, "E667", {"start": v(11.5, 17.1) * mm, "end": v(11.52, 17) * mm});
            skLineSegment(sketch, "E668", {"start": v(11.52, 17) * mm, "end": v(11.55, 16.9) * mm});
            skLineSegment(sketch, "E669", {"start": v(11.55, 16.9) * mm, "end": v(11.6, 16.8) * mm});
            skLineSegment(sketch, "E670", {"start": v(11.6, 16.8) * mm, "end": v(11.66, 16.7) * mm});
            skLineSegment(sketch, "E671", {"start": v(11.66, 16.7) * mm, "end": v(11.73, 16.6) * mm});
            skLineSegment(sketch, "E672", {"start": v(11.73, 16.6) * mm, "end": v(11.93, 16.36) * mm});
            skLineSegment(sketch, "E673", {"start": v(11.93, 16.36) * mm, "end": v(12.12, 16.1) * mm});
            skLineSegment(sketch, "E674", {"start": v(12.12, 16.1) * mm, "end": v(12.31, 15.85) * mm});
            skLineSegment(sketch, "E675", {"start": v(12.31, 15.85) * mm, "end": v(12.5, 15.6) * mm});
            skLineSegment(sketch, "E676", {"start": v(12.5, 15.6) * mm, "end": v(12.67, 15.33) * mm});
            skLineSegment(sketch, "E677", {"start": v(12.67, 15.33) * mm, "end": v(12.84, 15.07) * mm});
            skLineSegment(sketch, "E678", {"start": v(12.84, 15.07) * mm, "end": v(13, 14.8) * mm});
            skLineSegment(sketch, "E679", {"start": v(13, 14.8) * mm, "end": v(13.15, 14.51) * mm});
            skLineSegment(sketch, "E680", {"start": v(13.15, 14.51) * mm, "end": v(13.24, 14.37) * mm});
            skLineSegment(sketch, "E681", {"start": v(13.24, 14.37) * mm, "end": v(13.34, 14.27) * mm});
            skLineSegment(sketch, "E682", {"start": v(13.34, 14.27) * mm, "end": v(13.45, 14.21) * mm});
            skLineSegment(sketch, "E683", {"start": v(13.45, 14.21) * mm, "end": v(13.56, 14.2) * mm});
            skLineSegment(sketch, "E684", {"start": v(13.56, 14.2) * mm, "end": v(13.68, 14.2) * mm});
            skLineSegment(sketch, "E685", {"start": v(13.68, 14.2) * mm, "end": v(13.8, 14.23) * mm});
            skLineSegment(sketch, "E686", {"start": v(13.8, 14.23) * mm, "end": v(13.93, 14.28) * mm});
            skLineSegment(sketch, "E687", {"start": v(13.93, 14.28) * mm, "end": v(14.06, 14.33) * mm});
            skLineSegment(sketch, "E688", {"start": v(14.06, 14.33) * mm, "end": v(14.94, 14.7) * mm});
            skLineSegment(sketch, "E689", {"start": v(14.94, 14.7) * mm, "end": v(15.82, 15.03) * mm});
            skLineSegment(sketch, "E690", {"start": v(15.82, 15.03) * mm, "end": v(16.72, 15.34) * mm});
            skLineSegment(sketch, "E691", {"start": v(16.72, 15.34) * mm, "end": v(17.62, 15.63) * mm});
            skLineSegment(sketch, "E692", {"start": v(17.62, 15.63) * mm, "end": v(18.53, 15.89) * mm});
            skLineSegment(sketch, "E693", {"start": v(18.53, 15.89) * mm, "end": v(19.45, 16.13) * mm});
            skLineSegment(sketch, "E694", {"start": v(19.45, 16.13) * mm, "end": v(20.37, 16.35) * mm});
            skLineSegment(sketch, "E695", {"start": v(20.37, 16.35) * mm, "end": v(21.3, 16.54) * mm});
            skLineSegment(sketch, "E696", {"start": v(21.3, 16.54) * mm, "end": v(21.59, 16.6) * mm});
            skLineSegment(sketch, "E697", {"start": v(21.59, 16.6) * mm, "end": v(21.87, 16.65) * mm});
            skLineSegment(sketch, "E698", {"start": v(21.87, 16.65) * mm, "end": v(22.15, 16.7) * mm});
            skLineSegment(sketch, "E699", {"start": v(22.15, 16.7) * mm, "end": v(22.44, 16.73) * mm});
            skLineSegment(sketch, "E700", {"start": v(22.44, 16.73) * mm, "end": v(22.72, 16.76) * mm});
            skLineSegment(sketch, "E701", {"start": v(22.72, 16.76) * mm, "end": v(23, 16.78) * mm});
            skLineSegment(sketch, "E702", {"start": v(23, 16.78) * mm, "end": v(23.3, 16.8) * mm});
            skLineSegment(sketch, "E703", {"start": v(23.3, 16.8) * mm, "end": v(23.59, 16.79) * mm});
            skLineSegment(sketch, "E704", {"start": v(23.59, 16.79) * mm, "end": v(23.76, 16.78) * mm});
            skLineSegment(sketch, "E705", {"start": v(23.76, 16.78) * mm, "end": v(23.93, 16.78) * mm});
            skLineSegment(sketch, "E706", {"start": v(23.93, 16.78) * mm, "end": v(24.1, 16.77) * mm});
            skLineSegment(sketch, "E707", {"start": v(24.1, 16.77) * mm, "end": v(24.25, 16.74) * mm});
            skLineSegment(sketch, "E708", {"start": v(24.25, 16.74) * mm, "end": v(24.4, 16.69) * mm});
            skLineSegment(sketch, "E709", {"start": v(24.4, 16.69) * mm, "end": v(24.55, 16.6) * mm});
            skLineSegment(sketch, "E710", {"start": v(24.55, 16.6) * mm, "end": v(24.67, 16.48) * mm});
            skLineSegment(sketch, "E711", {"start": v(24.67, 16.48) * mm, "end": v(24.78, 16.3) * mm});
            skLineSegment(sketch, "E712", {"start": v(24.78, 16.3) * mm, "end": v(24.84, 16.23) * mm});
            skLineSegment(sketch, "E713", {"start": v(24.84, 16.23) * mm, "end": v(24.9, 16.19) * mm});
            skLineSegment(sketch, "E714", {"start": v(24.9, 16.19) * mm, "end": v(24.98, 16.17) * mm});
            skLineSegment(sketch, "E715", {"start": v(24.98, 16.17) * mm, "end": v(25.07, 16.16) * mm});
            skLineSegment(sketch, "E716", {"start": v(25.07, 16.16) * mm, "end": v(25.16, 16.16) * mm});
            skLineSegment(sketch, "E717", {"start": v(25.16, 16.16) * mm, "end": v(25.25, 16.17) * mm});
            skLineSegment(sketch, "E718", {"start": v(25.25, 16.17) * mm, "end": v(25.34, 16.17) * mm});
            skLineSegment(sketch, "E719", {"start": v(25.34, 16.17) * mm, "end": v(25.42, 16.17) * mm});
            skLineSegment(sketch, "E720", {"start": v(25.42, 16.17) * mm, "end": v(27.31, 15.94) * mm});
            skLineSegment(sketch, "E721", {"start": v(27.31, 15.94) * mm, "end": v(29.19, 15.66) * mm});
            skLineSegment(sketch, "E722", {"start": v(29.19, 15.66) * mm, "end": v(31.05, 15.33) * mm});
            skLineSegment(sketch, "E723", {"start": v(31.05, 15.33) * mm, "end": v(32.9, 14.93) * mm});
            skLineSegment(sketch, "E724", {"start": v(32.9, 14.93) * mm, "end": v(34.74, 14.47) * mm});
            skLineSegment(sketch, "E725", {"start": v(34.74, 14.47) * mm, "end": v(36.55, 13.95) * mm});
            skLineSegment(sketch, "E726", {"start": v(36.55, 13.95) * mm, "end": v(38.36, 13.35) * mm});
            skLineSegment(sketch, "E727", {"start": v(38.36, 13.35) * mm, "end": v(40.14, 12.69) * mm});
            skLineSegment(sketch, "E728", {"start": v(40.14, 12.69) * mm, "end": v(40.3, 12.62) * mm});
            skLineSegment(sketch, "E729", {"start": v(40.3, 12.62) * mm, "end": v(40.47, 12.54) * mm});
            skLineSegment(sketch, "E730", {"start": v(40.47, 12.54) * mm, "end": v(40.64, 12.46) * mm});
            skLineSegment(sketch, "E731", {"start": v(40.64, 12.46) * mm, "end": v(40.8, 12.37) * mm});
            skLineSegment(sketch, "E732", {"start": v(40.8, 12.37) * mm, "end": v(40.96, 12.28) * mm});
            skLineSegment(sketch, "E733", {"start": v(40.96, 12.28) * mm, "end": v(41.11, 12.18) * mm});
            skLineSegment(sketch, "E734", {"start": v(41.11, 12.18) * mm, "end": v(41.26, 12.08) * mm});
            skLineSegment(sketch, "E735", {"start": v(41.26, 12.08) * mm, "end": v(41.4, 11.98) * mm});
            skLineSegment(sketch, "E736", {"start": v(41.4, 11.98) * mm, "end": v(41.54, 11.86) * mm});
            skLineSegment(sketch, "E737", {"start": v(41.54, 11.86) * mm, "end": v(41.63, 11.74) * mm});
            skLineSegment(sketch, "E738", {"start": v(41.63, 11.74) * mm, "end": v(41.68, 11.62) * mm});
            skLineSegment(sketch, "E739", {"start": v(41.68, 11.62) * mm, "end": v(41.68, 11.5) * mm});
            skLineSegment(sketch, "E740", {"start": v(41.68, 11.5) * mm, "end": v(41.64, 11.4) * mm});
            skLineSegment(sketch, "E741", {"start": v(41.64, 11.4) * mm, "end": v(41.55, 11.3) * mm});
            skLineSegment(sketch, "E742", {"start": v(41.55, 11.3) * mm, "end": v(41.42, 11.21) * mm});
            skLineSegment(sketch, "E743", {"start": v(41.42, 11.21) * mm, "end": v(41.25, 11.14) * mm});
            skLineSegment(sketch, "E744", {"start": v(41.25, 11.14) * mm, "end": v(41, 11.07) * mm});
            skLineSegment(sketch, "E745", {"start": v(41, 11.07) * mm, "end": v(40.76, 11.02) * mm});
            skLineSegment(sketch, "E746", {"start": v(40.76, 11.02) * mm, "end": v(40.5, 10.99) * mm});
            skLineSegment(sketch, "E747", {"start": v(40.5, 10.99) * mm, "end": v(40.26, 10.98) * mm});
            skLineSegment(sketch, "E748", {"start": v(40.26, 10.98) * mm, "end": v(40, 10.98) * mm});
            skLineSegment(sketch, "E749", {"start": v(40, 10.98) * mm, "end": v(39.76, 10.99) * mm});
            skLineSegment(sketch, "E750", {"start": v(39.76, 10.99) * mm, "end": v(39.51, 11) * mm});
            skLineSegment(sketch, "E751", {"start": v(39.51, 11) * mm, "end": v(39.27, 11.03) * mm});
            skLineSegment(sketch, "E752", {"start": v(39.27, 11.03) * mm, "end": v(37.25, 11.27) * mm});
            skLineSegment(sketch, "E753", {"start": v(37.25, 11.27) * mm, "end": v(35.25, 11.56) * mm});
            skLineSegment(sketch, "E754", {"start": v(35.25, 11.56) * mm, "end": v(33.27, 11.91) * mm});
            skLineSegment(sketch, "E755", {"start": v(33.27, 11.91) * mm, "end": v(31.3, 12.33) * mm});
            skLineSegment(sketch, "E756", {"start": v(31.3, 12.33) * mm, "end": v(29.34, 12.82) * mm});
            skLineSegment(sketch, "E757", {"start": v(29.34, 12.82) * mm, "end": v(27.4, 13.4) * mm});
            skLineSegment(sketch, "E758", {"start": v(27.4, 13.4) * mm, "end": v(25.5, 14.06) * mm});
            skLineSegment(sketch, "E759", {"start": v(25.5, 14.06) * mm, "end": v(23.6, 14.81) * mm});
            skLineSegment(sketch, "E760", {"start": v(23.6, 14.81) * mm, "end": v(23.5, 14.86) * mm});
            skLineSegment(sketch, "E761", {"start": v(23.5, 14.86) * mm, "end": v(23.39, 14.9) * mm});
            skLineSegment(sketch, "E762", {"start": v(23.39, 14.9) * mm, "end": v(23.28, 14.91) * mm});
            skLineSegment(sketch, "E763", {"start": v(23.28, 14.91) * mm, "end": v(23.17, 14.93) * mm});
            skLineSegment(sketch, "E764", {"start": v(23.17, 14.93) * mm, "end": v(23.07, 14.92) * mm});
            skLineSegment(sketch, "E765", {"start": v(23.07, 14.92) * mm, "end": v(22.96, 14.9) * mm});
            skLineSegment(sketch, "E766", {"start": v(22.96, 14.9) * mm, "end": v(22.85, 14.88) * mm});
            skLineSegment(sketch, "E767", {"start": v(22.85, 14.88) * mm, "end": v(22.74, 14.83) * mm});
            skLineSegment(sketch, "E768", {"start": v(22.74, 14.83) * mm, "end": v(21.76, 14.4) * mm});
            skLineSegment(sketch, "E769", {"start": v(21.76, 14.4) * mm, "end": v(20.77, 14) * mm});
            skLineSegment(sketch, "E770", {"start": v(20.77, 14) * mm, "end": v(19.77, 13.63) * mm});
            skLineSegment(sketch, "E771", {"start": v(19.77, 13.63) * mm, "end": v(18.77, 13.3) * mm});
            skLineSegment(sketch, "E772", {"start": v(18.77, 13.3) * mm, "end": v(17.75, 13) * mm});
            skLineSegment(sketch, "E773", {"start": v(17.75, 13) * mm, "end": v(16.72, 12.74) * mm});
            skLineSegment(sketch, "E774", {"start": v(16.72, 12.74) * mm, "end": v(15.68, 12.5) * mm});
            skLineSegment(sketch, "E775", {"start": v(15.68, 12.5) * mm, "end": v(14.64, 12.29) * mm});
            skLineSegment(sketch, "E776", {"start": v(14.64, 12.29) * mm, "end": v(14.46, 12.25) * mm});
            skLineSegment(sketch, "E777", {"start": v(14.46, 12.25) * mm, "end": v(14.3, 12.2) * mm});
            skLineSegment(sketch, "E778", {"start": v(14.3, 12.2) * mm, "end": v(14.17, 12.14) * mm});
            skLineSegment(sketch, "E779", {"start": v(14.17, 12.14) * mm, "end": v(14.07, 12.06) * mm});
            skLineSegment(sketch, "E780", {"start": v(14.07, 12.06) * mm, "end": v(13.99, 11.96) * mm});
            skLineSegment(sketch, "E781", {"start": v(13.99, 11.96) * mm, "end": v(13.93, 11.83) * mm});
            skLineSegment(sketch, "E782", {"start": v(13.93, 11.83) * mm, "end": v(13.9, 11.67) * mm});
            skLineSegment(sketch, "E783", {"start": v(13.9, 11.67) * mm, "end": v(13.88, 11.48) * mm});
            skLineSegment(sketch, "E784", {"start": v(13.88, 11.48) * mm, "end": v(13.83, 11.06) * mm});
            skLineSegment(sketch, "E785", {"start": v(13.83, 11.06) * mm, "end": v(13.72, 10.66) * mm});
            skLineSegment(sketch, "E786", {"start": v(13.72, 10.66) * mm, "end": v(13.56, 10.28) * mm});
            skLineSegment(sketch, "E787", {"start": v(13.56, 10.28) * mm, "end": v(13.35, 9.91) * mm});
            skLineSegment(sketch, "E788", {"start": v(13.35, 9.91) * mm, "end": v(13.1, 9.56) * mm});
            skLineSegment(sketch, "E789", {"start": v(13.1, 9.56) * mm, "end": v(12.84, 9.2) * mm});
            skLineSegment(sketch, "E790", {"start": v(12.84, 9.2) * mm, "end": v(12.55, 8.84) * mm});
            skLineSegment(sketch, "E791", {"start": v(12.55, 8.84) * mm, "end": v(12.25, 8.46) * mm});
            skLineSegment(sketch, "E792", {"start": v(12.25, 8.46) * mm, "end": v(12.74, 8.5) * mm});
            skLineSegment(sketch, "E793", {"start": v(12.74, 8.5) * mm, "end": v(13.2, 8.52) * mm});
            skLineSegment(sketch, "E794", {"start": v(13.2, 8.52) * mm, "end": v(13.66, 8.55) * mm});
            skLineSegment(sketch, "E795", {"start": v(13.66, 8.55) * mm, "end": v(14.11, 8.58) * mm});
            skLineSegment(sketch, "E796", {"start": v(14.11, 8.58) * mm, "end": v(14.56, 8.6) * mm});
            skLineSegment(sketch, "E797", {"start": v(14.56, 8.6) * mm, "end": v(15, 8.63) * mm});
            skLineSegment(sketch, "E798", {"start": v(15, 8.63) * mm, "end": v(15.43, 8.66) * mm});
            skLineSegment(sketch, "E799", {"start": v(15.43, 8.66) * mm, "end": v(15.86, 8.68) * mm});
            skLineSegment(sketch, "E800", {"start": v(15.86, 8.68) * mm, "end": v(16.93, 8.73) * mm});
            skLineSegment(sketch, "E801", {"start": v(16.93, 8.73) * mm, "end": v(18, 8.77) * mm});
            skLineSegment(sketch, "E802", {"start": v(18, 8.77) * mm, "end": v(19.08, 8.79) * mm});
            skLineSegment(sketch, "E803", {"start": v(19.08, 8.79) * mm, "end": v(20.15, 8.8) * mm});
            skLineSegment(sketch, "E804", {"start": v(20.15, 8.8) * mm, "end": v(21.23, 8.79) * mm});
            skLineSegment(sketch, "E805", {"start": v(21.23, 8.79) * mm, "end": v(22.3, 8.77) * mm});
            skLineSegment(sketch, "E806", {"start": v(22.3, 8.77) * mm, "end": v(23.37, 8.73) * mm});
            skLineSegment(sketch, "E807", {"start": v(23.37, 8.73) * mm, "end": v(24.45, 8.69) * mm});
            skLineSegment(sketch, "E808", {"start": v(24.45, 8.69) * mm, "end": v(25.3, 8.64) * mm});
            skLineSegment(sketch, "E809", {"start": v(25.3, 8.64) * mm, "end": v(26.13, 8.6) * mm});
            skLineSegment(sketch, "E810", {"start": v(26.13, 8.6) * mm, "end": v(26.98, 8.54) * mm});
            skLineSegment(sketch, "E811", {"start": v(26.98, 8.54) * mm, "end": v(27.82, 8.48) * mm});
            skLineSegment(sketch, "E812", {"start": v(27.82, 8.48) * mm, "end": v(28.66, 8.42) * mm});
            skLineSegment(sketch, "E813", {"start": v(28.66, 8.42) * mm, "end": v(29.5, 8.34) * mm});
            skLineSegment(sketch, "E814", {"start": v(29.5, 8.34) * mm, "end": v(30.34, 8.26) * mm});
            skLineSegment(sketch, "E815", {"start": v(30.34, 8.26) * mm, "end": v(31.17, 8.16) * mm});
            skLineSegment(sketch, "E816", {"start": v(31.17, 8.16) * mm, "end": v(33.65, 7.85) * mm});
            skLineSegment(sketch, "E817", {"start": v(33.65, 7.85) * mm, "end": v(36.12, 7.5) * mm});
            skLineSegment(sketch, "E818", {"start": v(36.12, 7.5) * mm, "end": v(38.57, 7.08) * mm});
            skLineSegment(sketch, "E819", {"start": v(38.57, 7.08) * mm, "end": v(41, 6.58) * mm});
            skLineSegment(sketch, "E820", {"start": v(41, 6.58) * mm, "end": v(43.42, 6) * mm});
            skLineSegment(sketch, "E821", {"start": v(43.42, 6) * mm, "end": v(45.8, 5.3) * mm});
            skLineSegment(sketch, "E822", {"start": v(45.8, 5.3) * mm, "end": v(48.17, 4.48) * mm});
            skLineSegment(sketch, "E823", {"start": v(48.17, 4.48) * mm, "end": v(50.49, 3.52) * mm});
            skLineSegment(sketch, "E824", {"start": v(50.49, 3.52) * mm, "end": v(51.12, 3.22) * mm});
            skLineSegment(sketch, "E825", {"start": v(51.12, 3.22) * mm, "end": v(51.75, 2.9) * mm});
            skLineSegment(sketch, "E826", {"start": v(51.75, 2.9) * mm, "end": v(52.35, 2.56) * mm});
            skLineSegment(sketch, "E827", {"start": v(52.35, 2.56) * mm, "end": v(52.94, 2.2) * mm});
            skLineSegment(sketch, "E828", {"start": v(52.94, 2.2) * mm, "end": v(53.5, 1.79) * mm});
            skLineSegment(sketch, "E829", {"start": v(53.5, 1.79) * mm, "end": v(54.05, 1.35) * mm});
            skLineSegment(sketch, "E830", {"start": v(54.05, 1.35) * mm, "end": v(54.56, 0.86) * mm});
            skLineSegment(sketch, "E831", {"start": v(54.56, 0.86) * mm, "end": v(55.03, 0.33) * mm});
            skLineSegment(sketch, "E832", {"start": v(55.03, 0.33) * mm, "end": v(55.4, -0.17) * mm});
            skLineSegment(sketch, "E833", {"start": v(55.4, -0.17) * mm, "end": v(55.68, -0.68) * mm});
            skLineSegment(sketch, "E834", {"start": v(55.68, -0.68) * mm, "end": v(55.87, -1.2) * mm});
            skLineSegment(sketch, "E835", {"start": v(55.87, -1.2) * mm, "end": v(55.99, -1.75) * mm});
            skLineSegment(sketch, "E836", {"start": v(55.99, -1.75) * mm, "end": v(56.03, -2.3) * mm});
            skLineSegment(sketch, "E837", {"start": v(56.03, -2.3) * mm, "end": v(56, -2.85) * mm});
            skLineSegment(sketch, "E838", {"start": v(56, -2.85) * mm, "end": v(55.9, -3.42) * mm});
            skLineSegment(sketch, "E839", {"start": v(55.9, -3.42) * mm, "end": v(55.73, -4) * mm});
            skLineSegment(sketch, "E840", {"start": v(55.73, -4) * mm, "end": v(55.48, -4.64) * mm});
            skLineSegment(sketch, "E841", {"start": v(55.48, -4.64) * mm, "end": v(55.17, -5.24) * mm});
            skLineSegment(sketch, "E842", {"start": v(55.17, -5.24) * mm, "end": v(54.83, -5.81) * mm});
            skLineSegment(sketch, "E843", {"start": v(54.83, -5.81) * mm, "end": v(54.45, -6.36) * mm});
            skLineSegment(sketch, "E844", {"start": v(54.45, -6.36) * mm, "end": v(54.03, -6.88) * mm});
            skLineSegment(sketch, "E845", {"start": v(54.03, -6.88) * mm, "end": v(53.58, -7.38) * mm});
            skLineSegment(sketch, "E846", {"start": v(53.58, -7.38) * mm, "end": v(53.1, -7.85) * mm});
            skLineSegment(sketch, "E847", {"start": v(53.1, -7.85) * mm, "end": v(52.6, -8.3) * mm});
            skLineSegment(sketch, "E848", {"start": v(52.6, -8.3) * mm, "end": v(50.57, -9.96) * mm});
            skLineSegment(sketch, "E849", {"start": v(50.57, -9.96) * mm, "end": v(48.46, -11.42) * mm});
            skLineSegment(sketch, "E850", {"start": v(48.46, -11.42) * mm, "end": v(46.26, -12.7) * mm});
            skLineSegment(sketch, "E851", {"start": v(46.26, -12.7) * mm, "end": v(43.99, -13.8) * mm});
            skLineSegment(sketch, "E852", {"start": v(43.99, -13.8) * mm, "end": v(41.63, -14.71) * mm});
            skLineSegment(sketch, "E853", {"start": v(41.63, -14.71) * mm, "end": v(39.2, -15.46) * mm});
            skLineSegment(sketch, "E854", {"start": v(39.2, -15.46) * mm, "end": v(36.7, -16.02) * mm});
            skLineSegment(sketch, "E855", {"start": v(36.7, -16.02) * mm, "end": v(34.13, -16.42) * mm});
            skLineSegment(sketch, "E856", {"start": v(34.13, -16.42) * mm, "end": v(31.57, -16.61) * mm});
            skLineSegment(sketch, "E857", {"start": v(31.57, -16.61) * mm, "end": v(29.05, -16.59) * mm});
            skLineSegment(sketch, "E858", {"start": v(29.05, -16.59) * mm, "end": v(26.58, -16.34) * mm});
            skLineSegment(sketch, "E859", {"start": v(26.58, -16.34) * mm, "end": v(24.14, -15.9) * mm});
            skLineSegment(sketch, "E860", {"start": v(24.14, -15.9) * mm, "end": v(21.74, -15.27) * mm});
            skLineSegment(sketch, "E861", {"start": v(21.74, -15.27) * mm, "end": v(19.38, -14.46) * mm});
            skLineSegment(sketch, "E862", {"start": v(19.38, -14.46) * mm, "end": v(17.06, -13.47) * mm});
            skLineSegment(sketch, "E863", {"start": v(17.06, -13.47) * mm, "end": v(14.77, -12.33) * mm});
            skLineSegment(sketch, "E864", {"start": v(14.77, -12.33) * mm, "end": v(13.83, -11.82) * mm});
            skLineSegment(sketch, "E865", {"start": v(13.83, -11.82) * mm, "end": v(12.92, -11.27) * mm});
            skLineSegment(sketch, "E866", {"start": v(12.92, -11.27) * mm, "end": v(12.02, -10.7) * mm});
            skLineSegment(sketch, "E867", {"start": v(12.02, -10.7) * mm, "end": v(11.14, -10.1) * mm});
            skLineSegment(sketch, "E868", {"start": v(11.14, -10.1) * mm, "end": v(10.27, -9.49) * mm});
            skLineSegment(sketch, "E869", {"start": v(10.27, -9.49) * mm, "end": v(9.43, -8.85) * mm});
            skLineSegment(sketch, "E870", {"start": v(9.43, -8.85) * mm, "end": v(8.6, -8.18) * mm});
            skLineSegment(sketch, "E871", {"start": v(8.6, -8.18) * mm, "end": v(7.78, -7.5) * mm});
            skLineSegment(sketch, "E872", {"start": v(7.78, -7.5) * mm, "end": v(7.74, -7.45) * mm});
            skLineSegment(sketch, "E873", {"start": v(7.74, -7.45) * mm, "end": v(7.7, -7.41) * mm});
            skLineSegment(sketch, "E874", {"start": v(7.7, -7.41) * mm, "end": v(7.65, -7.38) * mm});
            skLineSegment(sketch, "E875", {"start": v(7.65, -7.38) * mm, "end": v(7.6, -7.34) * mm});
            skLineSegment(sketch, "E876", {"start": v(7.6, -7.34) * mm, "end": v(7.55, -7.31) * mm});
            skLineSegment(sketch, "E877", {"start": v(7.55, -7.31) * mm, "end": v(7.48, -7.3) * mm});
            skLineSegment(sketch, "E878", {"start": v(7.48, -7.3) * mm, "end": v(7.4, -7.29) * mm});
            skLineSegment(sketch, "E879", {"start": v(7.4, -7.29) * mm, "end": v(7.31, -7.3) * mm});
            skLineSegment(sketch, "E880", {"start": v(7.31, -7.3) * mm, "end": v(7.27, -7.54) * mm});
            skLineSegment(sketch, "E881", {"start": v(7.27, -7.54) * mm, "end": v(7.23, -7.78) * mm});
            skLineSegment(sketch, "E882", {"start": v(7.23, -7.78) * mm, "end": v(7.19, -8.03) * mm});
            skLineSegment(sketch, "E883", {"start": v(7.19, -8.03) * mm, "end": v(7.14, -8.28) * mm});
            skLineSegment(sketch, "E884", {"start": v(7.14, -8.28) * mm, "end": v(7.1, -8.53) * mm});
            skLineSegment(sketch, "E885", {"start": v(7.1, -8.53) * mm, "end": v(7.05, -8.78) * mm});
            skLineSegment(sketch, "E886", {"start": v(7.05, -8.78) * mm, "end": v(7, -9.03) * mm});
            skLineSegment(sketch, "E887", {"start": v(7, -9.03) * mm, "end": v(6.95, -9.28) * mm});
            skLineSegment(sketch, "E888", {"start": v(6.95, -9.28) * mm, "end": v(6.86, -9.7) * mm});
            skLineSegment(sketch, "E889", {"start": v(6.86, -9.7) * mm, "end": v(6.75, -10.12) * mm});
            skLineSegment(sketch, "E890", {"start": v(6.75, -10.12) * mm, "end": v(6.62, -10.53) * mm});
            skLineSegment(sketch, "E891", {"start": v(6.62, -10.53) * mm, "end": v(6.5, -10.94) * mm});
            skLineSegment(sketch, "E892", {"start": v(6.5, -10.94) * mm, "end": v(6.35, -11.35) * mm});
            skLineSegment(sketch, "E893", {"start": v(6.35, -11.35) * mm, "end": v(6.19, -11.75) * mm});
            skLineSegment(sketch, "E894", {"start": v(6.19, -11.75) * mm, "end": v(6.02, -12.15) * mm});
            skLineSegment(sketch, "E895", {"start": v(6.02, -12.15) * mm, "end": v(5.85, -12.54) * mm});
            skLineSegment(sketch, "E896", {"start": v(5.85, -12.54) * mm, "end": v(5.8, -12.67) * mm});
            skLineSegment(sketch, "E897", {"start": v(5.8, -12.67) * mm, "end": v(5.76, -12.78) * mm});
            skLineSegment(sketch, "E898", {"start": v(5.76, -12.78) * mm, "end": v(5.74, -12.9) * mm});
            skLineSegment(sketch, "E899", {"start": v(5.74, -12.9) * mm, "end": v(5.74, -13) * mm});
            skLineSegment(sketch, "E900", {"start": v(5.74, -13) * mm, "end": v(5.76, -13.12) * mm});
            skLineSegment(sketch, "E901", {"start": v(5.76, -13.12) * mm, "end": v(5.8, -13.23) * mm});
            skLineSegment(sketch, "E902", {"start": v(5.8, -13.23) * mm, "end": v(5.85, -13.34) * mm});
            skLineSegment(sketch, "E903", {"start": v(5.85, -13.34) * mm, "end": v(5.92, -13.46) * mm});
            skLineSegment(sketch, "E904", {"start": v(5.92, -13.46) * mm, "end": v(7.03, -15.04) * mm});
            skLineSegment(sketch, "E905", {"start": v(7.03, -15.04) * mm, "end": v(8.1, -16.64) * mm});
            skLineSegment(sketch, "E906", {"start": v(8.1, -16.64) * mm, "end": v(9.13, -18.27) * mm});
            skLineSegment(sketch, "E907", {"start": v(9.13, -18.27) * mm, "end": v(10.12, -19.92) * mm});
            skLineSegment(sketch, "E908", {"start": v(10.12, -19.92) * mm, "end": v(11.05, -21.6) * mm});
            skLineSegment(sketch, "E909", {"start": v(11.05, -21.6) * mm, "end": v(11.92, -23.32) * mm});
            skLineSegment(sketch, "E910", {"start": v(11.92, -23.32) * mm, "end": v(12.72, -25.07) * mm});
            skLineSegment(sketch, "E911", {"start": v(12.72, -25.07) * mm, "end": v(13.46, -26.87) * mm});
            skLineSegment(sketch, "E912", {"start": v(13.46, -26.87) * mm, "end": v(13.52, -27) * mm});
            skLineSegment(sketch, "E913", {"start": v(13.52, -27) * mm, "end": v(13.6, -27.11) * mm});
            skLineSegment(sketch, "E914", {"start": v(13.6, -27.11) * mm, "end": v(13.7, -27.2) * mm});
            skLineSegment(sketch, "E915", {"start": v(13.7, -27.2) * mm, "end": v(13.8, -27.27) * mm});
            skLineSegment(sketch, "E916", {"start": v(13.8, -27.27) * mm, "end": v(13.9, -27.33) * mm});
            skLineSegment(sketch, "E917", {"start": v(13.9, -27.33) * mm, "end": v(14.03, -27.38) * mm});
            skLineSegment(sketch, "E918", {"start": v(14.03, -27.38) * mm, "end": v(14.15, -27.43) * mm});
            skLineSegment(sketch, "E919", {"start": v(14.15, -27.43) * mm, "end": v(14.27, -27.47) * mm});
            skLineSegment(sketch, "E920", {"start": v(14.27, -27.47) * mm, "end": v(15.24, -27.84) * mm});
            skLineSegment(sketch, "E921", {"start": v(15.24, -27.84) * mm, "end": v(16.18, -28.24) * mm});
            skLineSegment(sketch, "E922", {"start": v(16.18, -28.24) * mm, "end": v(17.11, -28.67) * mm});
            skLineSegment(sketch, "E923", {"start": v(17.11, -28.67) * mm, "end": v(18.02, -29.14) * mm});
            skLineSegment(sketch, "E924", {"start": v(18.02, -29.14) * mm, "end": v(18.92, -29.64) * mm});
            skLineSegment(sketch, "E925", {"start": v(18.92, -29.64) * mm, "end": v(19.8, -30.17) * mm});
            skLineSegment(sketch, "E926", {"start": v(19.8, -30.17) * mm, "end": v(20.64, -30.74) * mm});
            skLineSegment(sketch, "E927", {"start": v(20.64, -30.74) * mm, "end": v(21.47, -31.35) * mm});
            skLineSegment(sketch, "E928", {"start": v(21.47, -31.35) * mm, "end": v(21.64, -31.48) * mm});
            skLineSegment(sketch, "E929", {"start": v(21.64, -31.48) * mm, "end": v(21.8, -31.62) * mm});
            skLineSegment(sketch, "E930", {"start": v(21.8, -31.62) * mm, "end": v(21.95, -31.76) * mm});
            skLineSegment(sketch, "E931", {"start": v(21.95, -31.76) * mm, "end": v(22.1, -31.9) * mm});
            skLineSegment(sketch, "E932", {"start": v(22.1, -31.9) * mm, "end": v(22.25, -32.06) * mm});
            skLineSegment(sketch, "E933", {"start": v(22.25, -32.06) * mm, "end": v(22.4, -32.2) * mm});
            skLineSegment(sketch, "E934", {"start": v(22.4, -32.2) * mm, "end": v(22.55, -32.36) * mm});
            skLineSegment(sketch, "E935", {"start": v(22.55, -32.36) * mm, "end": v(22.7, -32.51) * mm});
            skLineSegment(sketch, "E936", {"start": v(22.7, -32.51) * mm, "end": v(22.77, -32.6) * mm});
            skLineSegment(sketch, "E937", {"start": v(22.77, -32.6) * mm, "end": v(22.83, -32.68) * mm});
            skLineSegment(sketch, "E938", {"start": v(22.83, -32.68) * mm, "end": v(22.9, -32.77) * mm});
            skLineSegment(sketch, "E939", {"start": v(22.9, -32.77) * mm, "end": v(22.93, -32.86) * mm});
            skLineSegment(sketch, "E940", {"start": v(22.93, -32.86) * mm, "end": v(22.96, -32.96) * mm});
            skLineSegment(sketch, "E941", {"start": v(22.96, -32.96) * mm, "end": v(22.97, -33.06) * mm});
            skLineSegment(sketch, "E942", {"start": v(22.97, -33.06) * mm, "end": v(22.95, -33.17) * mm});
            skLineSegment(sketch, "E943", {"start": v(22.95, -33.17) * mm, "end": v(22.92, -33.28) * mm});
            skLineSegment(sketch, "E944", {"start": v(22.92, -33.28) * mm, "end": v(22.85, -33.39) * mm});
            skLineSegment(sketch, "E945", {"start": v(22.85, -33.39) * mm, "end": v(22.77, -33.47) * mm});
            skLineSegment(sketch, "E946", {"start": v(22.77, -33.47) * mm, "end": v(22.68, -33.53) * mm});
            skLineSegment(sketch, "E947", {"start": v(22.68, -33.53) * mm, "end": v(22.57, -33.57) * mm});
            skLineSegment(sketch, "E948", {"start": v(22.57, -33.57) * mm, "end": v(22.47, -33.6) * mm});
            skLineSegment(sketch, "E949", {"start": v(22.47, -33.6) * mm, "end": v(22.35, -33.6) * mm});
            skLineSegment(sketch, "E950", {"start": v(22.35, -33.6) * mm, "end": v(22.24, -33.6) * mm});
            skLineSegment(sketch, "E951", {"start": v(22.24, -33.6) * mm, "end": v(22.12, -33.6) * mm});
            skLineSegment(sketch, "E952", {"start": v(22.12, -33.6) * mm, "end": v(21.86, -33.56) * mm});
            skLineSegment(sketch, "E953", {"start": v(21.86, -33.56) * mm, "end": v(21.6, -33.52) * mm});
            skLineSegment(sketch, "E954", {"start": v(21.6, -33.52) * mm, "end": v(21.35, -33.47) * mm});
            skLineSegment(sketch, "E955", {"start": v(21.35, -33.47) * mm, "end": v(21.1, -33.41) * mm});
            skLineSegment(sketch, "E956", {"start": v(21.1, -33.41) * mm, "end": v(20.85, -33.35) * mm});
            skLineSegment(sketch, "E957", {"start": v(20.85, -33.35) * mm, "end": v(20.6, -33.27) * mm});
            skLineSegment(sketch, "E958", {"start": v(20.6, -33.27) * mm, "end": v(20.36, -33.19) * mm});
            skLineSegment(sketch, "E959", {"start": v(20.36, -33.19) * mm, "end": v(20.11, -33.1) * mm});
            skLineSegment(sketch, "E960", {"start": v(20.11, -33.1) * mm, "end": v(19.13, -32.71) * mm});
            skLineSegment(sketch, "E961", {"start": v(19.13, -32.71) * mm, "end": v(18.16, -32.3) * mm});
            skLineSegment(sketch, "E962", {"start": v(18.16, -32.3) * mm, "end": v(17.2, -31.84) * mm});
            skLineSegment(sketch, "E963", {"start": v(17.2, -31.84) * mm, "end": v(16.28, -31.35) * mm});
            skLineSegment(sketch, "E964", {"start": v(16.28, -31.35) * mm, "end": v(15.37, -30.82) * mm});
            skLineSegment(sketch, "E965", {"start": v(15.37, -30.82) * mm, "end": v(14.48, -30.25) * mm});
            skLineSegment(sketch, "E966", {"start": v(14.48, -30.25) * mm, "end": v(13.62, -29.64) * mm});
            skLineSegment(sketch, "E967", {"start": v(13.62, -29.64) * mm, "end": v(12.8, -28.98) * mm});
            skLineSegment(sketch, "E968", {"start": v(12.8, -28.98) * mm, "end": v(12.58, -28.81) * mm});
            skLineSegment(sketch, "E969", {"start": v(12.58, -28.81) * mm, "end": v(12.37, -28.64) * mm});
            skLineSegment(sketch, "E970", {"start": v(12.37, -28.64) * mm, "end": v(12.17, -28.46) * mm});
            skLineSegment(sketch, "E971", {"start": v(12.17, -28.46) * mm, "end": v(11.99, -28.26) * mm});
            skLineSegment(sketch, "E972", {"start": v(11.99, -28.26) * mm, "end": v(11.84, -28.03) * mm});
            skLineSegment(sketch, "E973", {"start": v(11.84, -28.03) * mm, "end": v(11.74, -27.78) * mm});
            skLineSegment(sketch, "E974", {"start": v(11.74, -27.78) * mm, "end": v(11.7, -27.5) * mm});
            skLineSegment(sketch, "E975", {"start": v(11.7, -27.5) * mm, "end": v(11.71, -27.18) * mm});
            skLineSegment(sketch, "E976", {"start": v(11.71, -27.18) * mm, "end": v(11.71, -27.13) * mm});
            skLineSegment(sketch, "E977", {"start": v(11.71, -27.13) * mm, "end": v(11.7, -27.08) * mm});
            skLineSegment(sketch, "E978", {"start": v(11.7, -27.08) * mm, "end": v(11.68, -27.04) * mm});
            skLineSegment(sketch, "E979", {"start": v(11.68, -27.04) * mm, "end": v(11.65, -26.98) * mm});
            skLineSegment(sketch, "E980", {"start": v(11.65, -26.98) * mm, "end": v(11.6, -26.93) * mm});
            skLineSegment(sketch, "E981", {"start": v(11.6, -26.93) * mm, "end": v(11.57, -26.88) * mm});
            skLineSegment(sketch, "E982", {"start": v(11.57, -26.88) * mm, "end": v(11.53, -26.83) * mm});
            skLineSegment(sketch, "E983", {"start": v(11.53, -26.83) * mm, "end": v(11.5, -26.79) * mm});
            skLineSegment(sketch, "E984", {"start": v(11.5, -26.79) * mm, "end": v(10.47, -25.44) * mm});
            skLineSegment(sketch, "E985", {"start": v(10.47, -25.44) * mm, "end": v(9.5, -24.06) * mm});
            skLineSegment(sketch, "E986", {"start": v(9.5, -24.06) * mm, "end": v(8.56, -22.66) * mm});
            skLineSegment(sketch, "E987", {"start": v(8.56, -22.66) * mm, "end": v(7.67, -21.23) * mm});
            skLineSegment(sketch, "E988", {"start": v(7.67, -21.23) * mm, "end": v(6.81, -19.78) * mm});
            skLineSegment(sketch, "E989", {"start": v(6.81, -19.78) * mm, "end": v(5.99, -18.3) * mm});
            skLineSegment(sketch, "E990", {"start": v(5.99, -18.3) * mm, "end": v(5.2, -16.81) * mm});
            skLineSegment(sketch, "E991", {"start": v(5.2, -16.81) * mm, "end": v(4.43, -15.3) * mm});
            skLineSegment(sketch, "E992", {"start": v(4.43, -15.3) * mm, "end": v(4.38, -15.2) * mm});
            skLineSegment(sketch, "E993", {"start": v(4.38, -15.2) * mm, "end": v(4.34, -15.1) * mm});
            skLineSegment(sketch, "E994", {"start": v(4.34, -15.1) * mm, "end": v(4.29, -15) * mm});
            skLineSegment(sketch, "E995", {"start": v(4.29, -15) * mm, "end": v(4.23, -14.9) * mm});
            skLineSegment(sketch, "E996", {"start": v(4.23, -14.9) * mm, "end": v(4.17, -14.8) * mm});
            skLineSegment(sketch, "E997", {"start": v(4.17, -14.8) * mm, "end": v(4.09, -14.73) * mm});
            skLineSegment(sketch, "E998", {"start": v(4.09, -14.73) * mm, "end": v(3.99, -14.67) * mm});
            skLineSegment(sketch, "E999", {"start": v(3.99, -14.67) * mm, "end": v(3.86, -14.63) * mm});
            skLineSegment(sketch, "E1000", {"start": v(3.86, -14.63) * mm, "end": v(3.66, -14.6) * mm});
            skLineSegment(sketch, "E1001", {"start": v(3.66, -14.6) * mm, "end": v(3.48, -14.57) * mm});
            skLineSegment(sketch, "E1002", {"start": v(3.48, -14.57) * mm, "end": v(3.3, -14.57) * mm});
            skLineSegment(sketch, "E1003", {"start": v(3.3, -14.57) * mm, "end": v(3.15, -14.6) * mm});
            skLineSegment(sketch, "E1004", {"start": v(3.15, -14.6) * mm, "end": v(3, -14.68) * mm});
            skLineSegment(sketch, "E1005", {"start": v(3, -14.68) * mm, "end": v(2.88, -14.8) * mm});
            skLineSegment(sketch, "E1006", {"start": v(2.88, -14.8) * mm, "end": v(2.78, -14.99) * mm});
            skLineSegment(sketch, "E1007", {"start": v(2.78, -14.99) * mm, "end": v(2.69, -15.24) * mm});
            skLineSegment(sketch, "E1008", {"start": v(2.69, -15.24) * mm, "end": v(2.42, -16.11) * mm});
            skLineSegment(sketch, "E1009", {"start": v(2.42, -16.11) * mm, "end": v(2.13, -16.97) * mm});
            skLineSegment(sketch, "E1010", {"start": v(2.13, -16.97) * mm, "end": v(1.8, -17.82) * mm});
            skLineSegment(sketch, "E1011", {"start": v(1.8, -17.82) * mm, "end": v(1.45, -18.66) * mm});
            skLineSegment(sketch, "E1012", {"start": v(1.45, -18.66) * mm, "end": v(1.09, -19.5) * mm});
            skLineSegment(sketch, "E1013", {"start": v(1.09, -19.5) * mm, "end": v(0.7, -20.32) * mm});
            skLineSegment(sketch, "E1014", {"start": v(0.7, -20.32) * mm, "end": v(0.32, -21.15) * mm});
            skLineSegment(sketch, "E1015", {"start": v(0.32, -21.15) * mm, "end": v(-0.07, -21.97) * mm});
            skLineSegment(sketch, "E1016", {"start": v(-0.07, -21.97) * mm, "end": v(-0.3, -22.5) * mm});
            skLineSegment(sketch, "E1017", {"start": v(-0.3, -22.5) * mm, "end": v(-0.52, -23.03) * mm});
            skLineSegment(sketch, "E1018", {"start": v(-0.52, -23.03) * mm, "end": v(-0.7, -23.57) * mm});
            skLineSegment(sketch, "E1019", {"start": v(-0.7, -23.57) * mm, "end": v(-0.83, -24.13) * mm});
            skLineSegment(sketch, "E1020", {"start": v(-0.83, -24.13) * mm, "end": v(-0.92, -24.7) * mm});
            skLineSegment(sketch, "E1021", {"start": v(-0.92, -24.7) * mm, "end": v(-0.95, -25.27) * mm});
            skLineSegment(sketch, "E1022", {"start": v(-0.95, -25.27) * mm, "end": v(-0.92, -25.86) * mm});
            skLineSegment(sketch, "E1023", {"start": v(-0.92, -25.86) * mm, "end": v(-0.81, -26.47) * mm});
            skLineSegment(sketch, "E1024", {"start": v(-0.81, -26.47) * mm, "end": v(-0.68, -27.14) * mm});
            skLineSegment(sketch, "E1025", {"start": v(-0.68, -27.14) * mm, "end": v(-0.59, -27.8) * mm});
            skLineSegment(sketch, "E1026", {"start": v(-0.59, -27.8) * mm, "end": v(-0.53, -28.48) * mm});
            skLineSegment(sketch, "E1027", {"start": v(-0.53, -28.48) * mm, "end": v(-0.5, -29.16) * mm});
            skLineSegment(sketch, "E1028", {"start": v(-0.5, -29.16) * mm, "end": v(-0.48, -29.84) * mm});
            skLineSegment(sketch, "E1029", {"start": v(-0.48, -29.84) * mm, "end": v(-0.49, -30.53) * mm});
            skLineSegment(sketch, "E1030", {"start": v(-0.49, -30.53) * mm, "end": v(-0.5, -31.2) * mm});
            skLineSegment(sketch, "E1031", {"start": v(-0.5, -31.2) * mm, "end": v(-0.52, -31.9) * mm});
            skLineSegment(sketch, "E1032", {"start": v(-0.52, -31.9) * mm, "end": v(-0.53, -32.08) * mm});
            skLineSegment(sketch, "E1033", {"start": v(-0.53, -32.08) * mm, "end": v(-0.56, -32.26) * mm});
            skLineSegment(sketch, "E1034", {"start": v(-0.56, -32.26) * mm, "end": v(-0.6, -32.44) * mm});
            skLineSegment(sketch, "E1035", {"start": v(-0.6, -32.44) * mm, "end": v(-0.66, -32.62) * mm});
            skLineSegment(sketch, "E1036", {"start": v(-0.66, -32.62) * mm, "end": v(-0.73, -32.79) * mm});
            skLineSegment(sketch, "E1037", {"start": v(-0.73, -32.79) * mm, "end": v(-0.8, -32.96) * mm});
            skLineSegment(sketch, "E1038", {"start": v(-0.8, -32.96) * mm, "end": v(-0.9, -33.13) * mm});
            skLineSegment(sketch, "E1039", {"start": v(-0.9, -33.13) * mm, "end": v(-1.02, -33.3) * mm});
            skLineSegment(sketch, "E1040", {"start": v(-1.02, -33.3) * mm, "end": v(-1.17, -33.56) * mm});
            skLineSegment(sketch, "E1041", {"start": v(-1.17, -33.56) * mm, "end": v(-1.28, -33.84) * mm});
            skLineSegment(sketch, "E1042", {"start": v(-1.28, -33.84) * mm, "end": v(-1.36, -34.13) * mm});
            skLineSegment(sketch, "E1043", {"start": v(-1.36, -34.13) * mm, "end": v(-1.4, -34.43) * mm});
            skLineSegment(sketch, "E1044", {"start": v(-1.4, -34.43) * mm, "end": v(-1.45, -34.74) * mm});
            skLineSegment(sketch, "E1045", {"start": v(-1.45, -34.74) * mm, "end": v(-1.48, -35.05) * mm});
            skLineSegment(sketch, "E1046", {"start": v(-1.48, -35.05) * mm, "end": v(-1.52, -35.35) * mm});
            skLineSegment(sketch, "E1047", {"start": v(-1.52, -35.35) * mm, "end": v(-1.57, -35.65) * mm});
            skLineSegment(sketch, "E1048", {"start": v(-1.57, -35.65) * mm, "end": v(-2.01, -37.7) * mm});
            skLineSegment(sketch, "E1049", {"start": v(-2.01, -37.7) * mm, "end": v(-2.49, -39.73) * mm});
            skLineSegment(sketch, "E1050", {"start": v(-2.49, -39.73) * mm, "end": v(-3, -41.76) * mm});
            skLineSegment(sketch, "E1051", {"start": v(-3, -41.76) * mm, "end": v(-3.55, -43.77) * mm});
            skLineSegment(sketch, "E1052", {"start": v(-3.55, -43.77) * mm, "end": v(-4.14, -45.77) * mm});
            skLineSegment(sketch, "E1053", {"start": v(-4.14, -45.77) * mm, "end": v(-4.78, -47.76) * mm});
            skLineSegment(sketch, "E1054", {"start": v(-4.78, -47.76) * mm, "end": v(-5.47, -49.73) * mm});
            skLineSegment(sketch, "E1055", {"start": v(-5.47, -49.73) * mm, "end": v(-6.22, -51.69) * mm});
            skLineSegment(sketch, "E1056", {"start": v(-6.22, -51.69) * mm, "end": v(-6.29, -51.86) * mm});
            skLineSegment(sketch, "E1057", {"start": v(-6.29, -51.86) * mm, "end": v(-6.36, -52.02) * mm});
            skLineSegment(sketch, "E1058", {"start": v(-6.36, -52.02) * mm, "end": v(-6.44, -52.19) * mm});
            skLineSegment(sketch, "E1059", {"start": v(-6.44, -52.19) * mm, "end": v(-6.52, -52.35) * mm});
            skLineSegment(sketch, "E1060", {"start": v(-6.52, -52.35) * mm, "end": v(-6.6, -52.51) * mm});
            skLineSegment(sketch, "E1061", {"start": v(-6.6, -52.51) * mm, "end": v(-6.7, -52.67) * mm});
            skLineSegment(sketch, "E1062", {"start": v(-6.7, -52.67) * mm, "end": v(-6.79, -52.83) * mm});
            skLineSegment(sketch, "E1063", {"start": v(-6.79, -52.83) * mm, "end": v(-6.88, -52.99) * mm});
            skLineSegment(sketch, "E1064", {"start": v(-6.88, -52.99) * mm, "end": v(-6.92, -53.07) * mm});
            skLineSegment(sketch, "E1065", {"start": v(-6.92, -53.07) * mm, "end": v(-6.97, -53.15) * mm});
            skLineSegment(sketch, "E1066", {"start": v(-6.97, -53.15) * mm, "end": v(-7.03, -53.23) * mm});
            skLineSegment(sketch, "E1067", {"start": v(-7.03, -53.23) * mm, "end": v(-7.1, -53.3) * mm});
            skLineSegment(sketch, "E1068", {"start": v(-7.1, -53.3) * mm, "end": v(-7.16, -53.36) * mm});
            skLineSegment(sketch, "E1069", {"start": v(-7.16, -53.36) * mm, "end": v(-7.25, -53.4) * mm});
            skLineSegment(sketch, "E1070", {"start": v(-7.25, -53.4) * mm, "end": v(-7.34, -53.4) * mm});
            skLineSegment(sketch, "E1071", {"start": v(-7.34, -53.4) * mm, "end": v(-7.45, -53.38) * mm});
            skLineSegment(sketch, "E1072", {"start": v(-7.45, -53.38) * mm, "end": v(-7.54, -53.33) * mm});
            skLineSegment(sketch, "E1073", {"start": v(-7.54, -53.33) * mm, "end": v(-7.6, -53.27) * mm});
            skLineSegment(sketch, "E1074", {"start": v(-7.6, -53.27) * mm, "end": v(-7.64, -53.2) * mm});
            skLineSegment(sketch, "E1075", {"start": v(-7.64, -53.2) * mm, "end": v(-7.66, -53.12) * mm});
            skLineSegment(sketch, "E1076", {"start": v(-7.66, -53.12) * mm, "end": v(-7.67, -53.04) * mm});
            skLineSegment(sketch, "E1077", {"start": v(-7.67, -53.04) * mm, "end": v(-7.67, -52.95) * mm});
            skLineSegment(sketch, "E1078", {"start": v(-7.67, -52.95) * mm, "end": v(-7.67, -52.86) * mm});
            skLineSegment(sketch, "E1079", {"start": v(-7.67, -52.86) * mm, "end": v(-7.67, -52.77) * mm});
            skLineSegment(sketch, "E1080", {"start": v(-7.67, -52.77) * mm, "end": v(-7.67, -52.13) * mm});
            skLineSegment(sketch, "E1081", {"start": v(-7.67, -52.13) * mm, "end": v(-7.64, -51.48) * mm});
            skLineSegment(sketch, "E1082", {"start": v(-7.64, -51.48) * mm, "end": v(-7.58, -50.84) * mm});
            skLineSegment(sketch, "E1083", {"start": v(-7.58, -50.84) * mm, "end": v(-7.49, -50.21) * mm});
            skLineSegment(sketch, "E1084", {"start": v(-7.49, -50.21) * mm, "end": v(-7.37, -49.58) * mm});
            skLineSegment(sketch, "E1085", {"start": v(-7.37, -49.58) * mm, "end": v(-7.25, -48.95) * mm});
            skLineSegment(sketch, "E1086", {"start": v(-7.25, -48.95) * mm, "end": v(-7.11, -48.32) * mm});
            skLineSegment(sketch, "E1087", {"start": v(-7.11, -48.32) * mm, "end": v(-6.97, -47.7) * mm});
            skLineSegment(sketch, "E1088", {"start": v(-6.97, -47.7) * mm, "end": v(-6.52, -45.7) * mm});
            skLineSegment(sketch, "E1089", {"start": v(-6.52, -45.7) * mm, "end": v(-6.04, -43.72) * mm});
            skLineSegment(sketch, "E1090", {"start": v(-6.04, -43.72) * mm, "end": v(-5.53, -41.75) * mm});
            skLineSegment(sketch, "E1091", {"start": v(-5.53, -41.75) * mm, "end": v(-4.98, -39.78) * mm});
            skLineSegment(sketch, "E1092", {"start": v(-4.98, -39.78) * mm, "end": v(-4.39, -37.83) * mm});
            skLineSegment(sketch, "E1093", {"start": v(-4.39, -37.83) * mm, "end": v(-3.74, -35.9) * mm});
            skLineSegment(sketch, "E1094", {"start": v(-3.74, -35.9) * mm, "end": v(-3.04, -33.98) * mm});
            skLineSegment(sketch, "E1095", {"start": v(-3.04, -33.98) * mm, "end": v(-2.27, -32.08) * mm});
            skLineSegment(sketch, "E1096", {"start": v(-2.27, -32.08) * mm, "end": v(-2.23, -31.96) * mm});
            skLineSegment(sketch, "E1097", {"start": v(-2.23, -31.96) * mm, "end": v(-2.2, -31.85) * mm});
            skLineSegment(sketch, "E1098", {"start": v(-2.2, -31.85) * mm, "end": v(-2.2, -31.74) * mm});
            skLineSegment(sketch, "E1099", {"start": v(-2.2, -31.74) * mm, "end": v(-2.2, -31.63) * mm});
            skLineSegment(sketch, "E1100", {"start": v(-2.2, -31.63) * mm, "end": v(-2.2, -31.52) * mm});
            skLineSegment(sketch, "E1101", {"start": v(-2.2, -31.52) * mm, "end": v(-2.23, -31.41) * mm});
            skLineSegment(sketch, "E1102", {"start": v(-2.23, -31.41) * mm, "end": v(-2.25, -31.3) * mm});
            skLineSegment(sketch, "E1103", {"start": v(-2.25, -31.3) * mm, "end": v(-2.28, -31.2) * mm});
            skLineSegment(sketch, "E1104", {"start": v(-2.28, -31.2) * mm, "end": v(-2.38, -30.78) * mm});
            skLineSegment(sketch, "E1105", {"start": v(-2.38, -30.78) * mm, "end": v(-2.47, -30.37) * mm});
            skLineSegment(sketch, "E1106", {"start": v(-2.47, -30.37) * mm, "end": v(-2.57, -29.96) * mm});
            skLineSegment(sketch, "E1107", {"start": v(-2.57, -29.96) * mm, "end": v(-2.66, -29.55) * mm});
            skLineSegment(sketch, "E1108", {"start": v(-2.66, -29.55) * mm, "end": v(-2.76, -29.14) * mm});
            skLineSegment(sketch, "E1109", {"start": v(-2.76, -29.14) * mm, "end": v(-2.85, -28.73) * mm});
            skLineSegment(sketch, "E1110", {"start": v(-2.85, -28.73) * mm, "end": v(-2.95, -28.32) * mm});
            skLineSegment(sketch, "E1111", {"start": v(-2.95, -28.32) * mm, "end": v(-3.04, -27.9) * mm});
            skLineSegment(sketch, "E1112", {"start": v(-3.04, -27.9) * mm, "end": v(-3.06, -27.83) * mm});
            skLineSegment(sketch, "E1113", {"start": v(-3.06, -27.83) * mm, "end": v(-3.06, -27.75) * mm});
            skLineSegment(sketch, "E1114", {"start": v(-3.06, -27.75) * mm, "end": v(-3.06, -27.67) * mm});
            skLineSegment(sketch, "E1115", {"start": v(-3.06, -27.67) * mm, "end": v(-3.06, -27.6) * mm});
            skLineSegment(sketch, "E1116", {"start": v(-3.06, -27.6) * mm, "end": v(-3.08, -27.52) * mm});
            skLineSegment(sketch, "E1117", {"start": v(-3.08, -27.52) * mm, "end": v(-3.1, -27.46) * mm});
            skLineSegment(sketch, "E1118", {"start": v(-3.1, -27.46) * mm, "end": v(-3.16, -27.4) * mm});
            skLineSegment(sketch, "E1119", {"start": v(-3.16, -27.4) * mm, "end": v(-3.23, -27.37) * mm});
            skLineSegment(sketch, "E1120", {"start": v(-3.23, -27.37) * mm, "end": v(-3.32, -27.36) * mm});
            skLineSegment(sketch, "E1121", {"start": v(-3.32, -27.36) * mm, "end": v(-3.38, -27.38) * mm});
            skLineSegment(sketch, "E1122", {"start": v(-3.38, -27.38) * mm, "end": v(-3.44, -27.42) * mm});
            skLineSegment(sketch, "E1123", {"start": v(-3.44, -27.42) * mm, "end": v(-3.5, -27.47) * mm});
            skLineSegment(sketch, "E1124", {"start": v(-3.5, -27.47) * mm, "end": v(-3.54, -27.54) * mm});
            skLineSegment(sketch, "E1125", {"start": v(-3.54, -27.54) * mm, "end": v(-3.58, -27.6) * mm});
            skLineSegment(sketch, "E1126", {"start": v(-3.58, -27.6) * mm, "end": v(-3.63, -27.67) * mm});
            skLineSegment(sketch, "E1127", {"start": v(-3.63, -27.67) * mm, "end": v(-3.67, -27.73) * mm});
            skLineSegment(sketch, "E1128", {"start": v(-3.67, -27.73) * mm, "end": v(-4.86, -28.96) * mm});
            skLineSegment(sketch, "E1129", {"start": v(-4.86, -28.96) * mm, "end": v(-6.07, -30.16) * mm});
            skLineSegment(sketch, "E1130", {"start": v(-6.07, -30.16) * mm, "end": v(-7.3, -31.34) * mm});
            skLineSegment(sketch, "E1131", {"start": v(-7.3, -31.34) * mm, "end": v(-8.58, -32.46) * mm});
            skLineSegment(sketch, "E1132", {"start": v(-8.58, -32.46) * mm, "end": v(-9.9, -33.51) * mm});
            skLineSegment(sketch, "E1133", {"start": v(-9.9, -33.51) * mm, "end": v(-11.3, -34.5) * mm});
            skLineSegment(sketch, "E1134", {"start": v(-11.3, -34.5) * mm, "end": v(-12.75, -35.38) * mm});
            skLineSegment(sketch, "E1135", {"start": v(-12.75, -35.38) * mm, "end": v(-14.3, -36.16) * mm});
            skLineSegment(sketch, "E1136", {"start": v(-14.3, -36.16) * mm, "end": v(-15.68, -36.74) * mm});
            skLineSegment(sketch, "E1137", {"start": v(-15.68, -36.74) * mm, "end": v(-17.07, -37.23) * mm});
            skLineSegment(sketch, "E1138", {"start": v(-17.07, -37.23) * mm, "end": v(-18.47, -37.61) * mm});
            skLineSegment(sketch, "E1139", {"start": v(-18.47, -37.61) * mm, "end": v(-19.9, -37.88) * mm});
            skLineSegment(sketch, "E1140", {"start": v(-19.9, -37.88) * mm, "end": v(-21.32, -38.02) * mm});
            skLineSegment(sketch, "E1141", {"start": v(-21.32, -38.02) * mm, "end": v(-22.77, -38.02) * mm});
            skLineSegment(sketch, "E1142", {"start": v(-22.77, -38.02) * mm, "end": v(-24.23, -37.88) * mm});
            skLineSegment(sketch, "E1143", {"start": v(-24.23, -37.88) * mm, "end": v(-25.71, -37.57) * mm});
            skLineSegment(sketch, "E1144", {"start": v(-25.71, -37.57) * mm, "end": v(-27.47, -37) * mm});
            skLineSegment(sketch, "E1145", {"start": v(-27.47, -37) * mm, "end": v(-29.05, -36.23) * mm});
            skLineSegment(sketch, "E1146", {"start": v(-29.05, -36.23) * mm, "end": v(-30.47, -35.28) * mm});
            skLineSegment(sketch, "E1147", {"start": v(-30.47, -35.28) * mm, "end": v(-31.73, -34.17) * mm});
            skLineSegment(sketch, "E1148", {"start": v(-31.73, -34.17) * mm, "end": v(-32.83, -32.9) * mm});
            skLineSegment(sketch, "E1149", {"start": v(-32.83, -32.9) * mm, "end": v(-33.79, -31.48) * mm});
            skLineSegment(sketch, "E1150", {"start": v(-33.79, -31.48) * mm, "end": v(-34.6, -29.92) * mm});
            skLineSegment(sketch, "E1151", {"start": v(-34.6, -29.92) * mm, "end": v(-35.28, -28.23) * mm});
            skLineSegment(sketch, "E1152", {"start": v(-35.28, -28.23) * mm, "end": v(-35.86, -26.32) * mm});
            skLineSegment(sketch, "E1153", {"start": v(-35.86, -26.32) * mm, "end": v(-36.25, -24.41) * mm});
            skLineSegment(sketch, "E1154", {"start": v(-36.25, -24.41) * mm, "end": v(-36.48, -22.5) * mm});
            skLineSegment(sketch, "E1155", {"start": v(-36.48, -22.5) * mm, "end": v(-36.54, -20.58) * mm});
            skLineSegment(sketch, "E1156", {"start": v(-36.54, -20.58) * mm, "end": v(-36.47, -18.66) * mm});
            skLineSegment(sketch, "E1157", {"start": v(-36.47, -18.66) * mm, "end": v(-36.26, -16.74) * mm});
            skLineSegment(sketch, "E1158", {"start": v(-36.26, -16.74) * mm, "end": v(-35.94, -14.82) * mm});
            skLineSegment(sketch, "E1159", {"start": v(-35.94, -14.82) * mm, "end": v(-35.5, -12.9) * mm});
            skLineSegment(sketch, "E1160", {"start": v(-35.5, -12.9) * mm, "end": v(-35.43, -12.54) * mm});
            skLineSegment(sketch, "E1161", {"start": v(-35.43, -12.54) * mm, "end": v(-35.36, -12.19) * mm});
            skLineSegment(sketch, "E1162", {"start": v(-35.36, -12.19) * mm, "end": v(-35.31, -11.83) * mm});
            skLineSegment(sketch, "E1163", {"start": v(-35.31, -11.83) * mm, "end": v(-35.26, -11.47) * mm});
            skLineSegment(sketch, "E1164", {"start": v(-35.26, -11.47) * mm, "end": v(-35.2, -11.11) * mm});
            skLineSegment(sketch, "E1165", {"start": v(-35.2, -11.11) * mm, "end": v(-35.13, -10.75) * mm});
            skLineSegment(sketch, "E1166", {"start": v(-35.13, -10.75) * mm, "end": v(-35.04, -10.4) * mm});
            skLineSegment(sketch, "E1167", {"start": v(-35.04, -10.4) * mm, "end": v(-34.93, -10.04) * mm});
            skSolve(sketch);
        }
        {
            var Q0;
            Q0 = qSketchRegion(id + "F0", true);
            extrude(context, id + "F1", {"entities" : qUnion([Q0]), "depth" : 5.08 * mm});
        }
        {
            var Q0;
            Q0=makeQuery(id+"F1.opExtrude","CAP_FACE",FACE,{"disambiguationData":[OSD([sQuery(id+"F0.wireOp",EDGE,"E0"),sQuery(id+"F0.wireOp",EDGE,"E1"),sQuery(id+"F0.wireOp",EDGE,"E2"),sQuery(id+"F0.wireOp",EDGE,"E3"),sQuery(id+"F0.wireOp",EDGE,"E4"),sQuery(id+"F0.wireOp",EDGE,"E5"),sQuery(id+"F0.wireOp",EDGE,"E6"),sQuery(id+"F0.wireOp",EDGE,"E7"),sQuery(id+"F0.wireOp",EDGE,"E8"),sQuery(id+"F0.wireOp",EDGE,"E9"),sQuery(id+"F0.wireOp",EDGE,"E10"),sQuery(id+"F0.wireOp",EDGE,"E11"),sQuery(id+"F0.wireOp",EDGE,"E12"),sQuery(id+"F0.wireOp",EDGE,"E13"),sQuery(id+"F0.wireOp",EDGE,"E14"),sQuery(id+"F0.wireOp",EDGE,"E15"),sQuery(id+"F0.wireOp",EDGE,"E16"),sQuery(id+"F0.wireOp",EDGE,"E17"),sQuery(id+"F0.wireOp",EDGE,"E18"),sQuery(id+"F0.wireOp",EDGE,"E19"),sQuery(id+"F0.wireOp",EDGE,"E20"),sQuery(id+"F0.wireOp",EDGE,"E21"),sQuery(id+"F0.wireOp",EDGE,"E22"),sQuery(id+"F0.wireOp",EDGE,"E23"),sQuery(id+"F0.wireOp",EDGE,"E24"),sQuery(id+"F0.wireOp",EDGE,"E25"),sQuery(id+"F0.wireOp",EDGE,"E26"),sQuery(id+"F0.wireOp",EDGE,"E27"),sQuery(id+"F0.wireOp",EDGE,"E28"),sQuery(id+"F0.wireOp",EDGE,"E29"),sQuery(id+"F0.wireOp",EDGE,"E30"),sQuery(id+"F0.wireOp",EDGE,"E31"),sQuery(id+"F0.wireOp",EDGE,"E32"),sQuery(id+"F0.wireOp",EDGE,"E33"),sQuery(id+"F0.wireOp",EDGE,"E34"),sQuery(id+"F0.wireOp",EDGE,"E35"),sQuery(id+"F0.wireOp",EDGE,"E36"),sQuery(id+"F0.wireOp",EDGE,"E37"),sQuery(id+"F0.wireOp",EDGE,"E38"),sQuery(id+"F0.wireOp",EDGE,"E39"),sQuery(id+"F0.wireOp",EDGE,"E40"),sQuery(id+"F0.wireOp",EDGE,"E41"),sQuery(id+"F0.wireOp",EDGE,"E42"),sQuery(id+"F0.wireOp",EDGE,"E43"),sQuery(id+"F0.wireOp",EDGE,"E44"),sQuery(id+"F0.wireOp",EDGE,"E45"),sQuery(id+"F0.wireOp",EDGE,"E46"),sQuery(id+"F0.wireOp",EDGE,"E47"),sQuery(id+"F0.wireOp",EDGE,"E48"),sQuery(id+"F0.wireOp",EDGE,"E49"),sQuery(id+"F0.wireOp",EDGE,"E50"),sQuery(id+"F0.wireOp",EDGE,"E51"),sQuery(id+"F0.wireOp",EDGE,"E52"),sQuery(id+"F0.wireOp",EDGE,"E53"),sQuery(id+"F0.wireOp",EDGE,"E54"),sQuery(id+"F0.wireOp",EDGE,"E55"),sQuery(id+"F0.wireOp",EDGE,"E56"),sQuery(id+"F0.wireOp",EDGE,"E57"),sQuery(id+"F0.wireOp",EDGE,"E58"),sQuery(id+"F0.wireOp",EDGE,"E59"),sQuery(id+"F0.wireOp",EDGE,"E60"),sQuery(id+"F0.wireOp",EDGE,"E61"),sQuery(id+"F0.wireOp",EDGE,"E62"),sQuery(id+"F0.wireOp",EDGE,"E63"),sQuery(id+"F0.wireOp",EDGE,"E64"),sQuery(id+"F0.wireOp",EDGE,"E65"),sQuery(id+"F0.wireOp",EDGE,"E66"),sQuery(id+"F0.wireOp",EDGE,"E67"),sQuery(id+"F0.wireOp",EDGE,"E68"),sQuery(id+"F0.wireOp",EDGE,"E69"),sQuery(id+"F0.wireOp",EDGE,"E70"),sQuery(id+"F0.wireOp",EDGE,"E71"),sQuery(id+"F0.wireOp",EDGE,"E72"),sQuery(id+"F0.wireOp",EDGE,"E73"),sQuery(id+"F0.wireOp",EDGE,"E74"),sQuery(id+"F0.wireOp",EDGE,"E75"),sQuery(id+"F0.wireOp",EDGE,"E76"),sQuery(id+"F0.wireOp",EDGE,"E77"),sQuery(id+"F0.wireOp",EDGE,"E78"),sQuery(id+"F0.wireOp",EDGE,"E79"),sQuery(id+"F0.wireOp",EDGE,"E80"),sQuery(id+"F0.wireOp",EDGE,"E81"),sQuery(id+"F0.wireOp",EDGE,"E82"),sQuery(id+"F0.wireOp",EDGE,"E83"),sQuery(id+"F0.wireOp",EDGE,"E84"),sQuery(id+"F0.wireOp",EDGE,"E85"),sQuery(id+"F0.wireOp",EDGE,"E86"),sQuery(id+"F0.wireOp",EDGE,"E87"),sQuery(id+"F0.wireOp",EDGE,"E88"),sQuery(id+"F0.wireOp",EDGE,"E89"),sQuery(id+"F0.wireOp",EDGE,"E90"),sQuery(id+"F0.wireOp",EDGE,"E91"),sQuery(id+"F0.wireOp",EDGE,"E92"),sQuery(id+"F0.wireOp",EDGE,"E93"),sQuery(id+"F0.wireOp",EDGE,"E94"),sQuery(id+"F0.wireOp",EDGE,"E95"),sQuery(id+"F0.wireOp",EDGE,"E96"),sQuery(id+"F0.wireOp",EDGE,"E97"),sQuery(id+"F0.wireOp",EDGE,"E98"),sQuery(id+"F0.wireOp",EDGE,"E99"),sQuery(id+"F0.wireOp",EDGE,"E100"),sQuery(id+"F0.wireOp",EDGE,"E101"),sQuery(id+"F0.wireOp",EDGE,"E102"),sQuery(id+"F0.wireOp",EDGE,"E103"),sQuery(id+"F0.wireOp",EDGE,"E104"),sQuery(id+"F0.wireOp",EDGE,"E105"),sQuery(id+"F0.wireOp",EDGE,"E106"),sQuery(id+"F0.wireOp",EDGE,"E107"),sQuery(id+"F0.wireOp",EDGE,"E108"),sQuery(id+"F0.wireOp",EDGE,"E109"),sQuery(id+"F0.wireOp",EDGE,"E110"),sQuery(id+"F0.wireOp",EDGE,"E111"),sQuery(id+"F0.wireOp",EDGE,"E112"),sQuery(id+"F0.wireOp",EDGE,"E113"),sQuery(id+"F0.wireOp",EDGE,"E114"),sQuery(id+"F0.wireOp",EDGE,"E115"),sQuery(id+"F0.wireOp",EDGE,"E116"),sQuery(id+"F0.wireOp",EDGE,"E117"),sQuery(id+"F0.wireOp",EDGE,"E118"),sQuery(id+"F0.wireOp",EDGE,"E119"),sQuery(id+"F0.wireOp",EDGE,"E120"),sQuery(id+"F0.wireOp",EDGE,"E121"),sQuery(id+"F0.wireOp",EDGE,"E122"),sQuery(id+"F0.wireOp",EDGE,"E123"),sQuery(id+"F0.wireOp",EDGE,"E124"),sQuery(id+"F0.wireOp",EDGE,"E125"),sQuery(id+"F0.wireOp",EDGE,"E126"),sQuery(id+"F0.wireOp",EDGE,"E127"),sQuery(id+"F0.wireOp",EDGE,"E128"),sQuery(id+"F0.wireOp",EDGE,"E129"),sQuery(id+"F0.wireOp",EDGE,"E130"),sQuery(id+"F0.wireOp",EDGE,"E131"),sQuery(id+"F0.wireOp",EDGE,"E132"),sQuery(id+"F0.wireOp",EDGE,"E133"),sQuery(id+"F0.wireOp",EDGE,"E134"),sQuery(id+"F0.wireOp",EDGE,"E135"),sQuery(id+"F0.wireOp",EDGE,"E136"),sQuery(id+"F0.wireOp",EDGE,"E137"),sQuery(id+"F0.wireOp",EDGE,"E138"),sQuery(id+"F0.wireOp",EDGE,"E139"),sQuery(id+"F0.wireOp",EDGE,"E140"),sQuery(id+"F0.wireOp",EDGE,"E141"),sQuery(id+"F0.wireOp",EDGE,"E142"),sQuery(id+"F0.wireOp",EDGE,"E143"),sQuery(id+"F0.wireOp",EDGE,"E144"),sQuery(id+"F0.wireOp",EDGE,"E145"),sQuery(id+"F0.wireOp",EDGE,"E146"),sQuery(id+"F0.wireOp",EDGE,"E147"),sQuery(id+"F0.wireOp",EDGE,"E148"),sQuery(id+"F0.wireOp",EDGE,"E149"),sQuery(id+"F0.wireOp",EDGE,"E150"),sQuery(id+"F0.wireOp",EDGE,"E151"),sQuery(id+"F0.wireOp",EDGE,"E152"),sQuery(id+"F0.wireOp",EDGE,"E153"),sQuery(id+"F0.wireOp",EDGE,"E154"),sQuery(id+"F0.wireOp",EDGE,"E155"),sQuery(id+"F0.wireOp",EDGE,"E156"),sQuery(id+"F0.wireOp",EDGE,"E157"),sQuery(id+"F0.wireOp",EDGE,"E158"),sQuery(id+"F0.wireOp",EDGE,"E159"),sQuery(id+"F0.wireOp",EDGE,"E160"),sQuery(id+"F0.wireOp",EDGE,"E161"),sQuery(id+"F0.wireOp",EDGE,"E162"),sQuery(id+"F0.wireOp",EDGE,"E163"),sQuery(id+"F0.wireOp",EDGE,"E164"),sQuery(id+"F0.wireOp",EDGE,"E165"),sQuery(id+"F0.wireOp",EDGE,"E166"),sQuery(id+"F0.wireOp",EDGE,"E167"),sQuery(id+"F0.wireOp",EDGE,"E168"),sQuery(id+"F0.wireOp",EDGE,"E169"),sQuery(id+"F0.wireOp",EDGE,"E170"),sQuery(id+"F0.wireOp",EDGE,"E171"),sQuery(id+"F0.wireOp",EDGE,"E172"),sQuery(id+"F0.wireOp",EDGE,"E173"),sQuery(id+"F0.wireOp",EDGE,"E174"),sQuery(id+"F0.wireOp",EDGE,"E175"),sQuery(id+"F0.wireOp",EDGE,"E176"),sQuery(id+"F0.wireOp",EDGE,"E177"),sQuery(id+"F0.wireOp",EDGE,"E178"),sQuery(id+"F0.wireOp",EDGE,"E179"),sQuery(id+"F0.wireOp",EDGE,"E180"),sQuery(id+"F0.wireOp",EDGE,"E181"),sQuery(id+"F0.wireOp",EDGE,"E182"),sQuery(id+"F0.wireOp",EDGE,"E183"),sQuery(id+"F0.wireOp",EDGE,"E184"),sQuery(id+"F0.wireOp",EDGE,"E185"),sQuery(id+"F0.wireOp",EDGE,"E186"),sQuery(id+"F0.wireOp",EDGE,"E187"),sQuery(id+"F0.wireOp",EDGE,"E188"),sQuery(id+"F0.wireOp",EDGE,"E189"),sQuery(id+"F0.wireOp",EDGE,"E190"),sQuery(id+"F0.wireOp",EDGE,"E191"),sQuery(id+"F0.wireOp",EDGE,"E192"),sQuery(id+"F0.wireOp",EDGE,"E193"),sQuery(id+"F0.wireOp",EDGE,"E194"),sQuery(id+"F0.wireOp",EDGE,"E195"),sQuery(id+"F0.wireOp",EDGE,"E196"),sQuery(id+"F0.wireOp",EDGE,"E197"),sQuery(id+"F0.wireOp",EDGE,"E198"),sQuery(id+"F0.wireOp",EDGE,"E199"),sQuery(id+"F0.wireOp",EDGE,"E200"),sQuery(id+"F0.wireOp",EDGE,"E201"),sQuery(id+"F0.wireOp",EDGE,"E202"),sQuery(id+"F0.wireOp",EDGE,"E203"),sQuery(id+"F0.wireOp",EDGE,"E204"),sQuery(id+"F0.wireOp",EDGE,"E205"),sQuery(id+"F0.wireOp",EDGE,"E206"),sQuery(id+"F0.wireOp",EDGE,"E207"),sQuery(id+"F0.wireOp",EDGE,"E208"),sQuery(id+"F0.wireOp",EDGE,"E209"),sQuery(id+"F0.wireOp",EDGE,"E210"),sQuery(id+"F0.wireOp",EDGE,"E211"),sQuery(id+"F0.wireOp",EDGE,"E212"),sQuery(id+"F0.wireOp",EDGE,"E213"),sQuery(id+"F0.wireOp",EDGE,"E214"),sQuery(id+"F0.wireOp",EDGE,"E215"),sQuery(id+"F0.wireOp",EDGE,"E216"),sQuery(id+"F0.wireOp",EDGE,"E217"),sQuery(id+"F0.wireOp",EDGE,"E218"),sQuery(id+"F0.wireOp",EDGE,"E219"),sQuery(id+"F0.wireOp",EDGE,"E220"),sQuery(id+"F0.wireOp",EDGE,"E221"),sQuery(id+"F0.wireOp",EDGE,"E222"),sQuery(id+"F0.wireOp",EDGE,"E223"),sQuery(id+"F0.wireOp",EDGE,"E224"),sQuery(id+"F0.wireOp",EDGE,"E225"),sQuery(id+"F0.wireOp",EDGE,"E226"),sQuery(id+"F0.wireOp",EDGE,"E227"),sQuery(id+"F0.wireOp",EDGE,"E228"),sQuery(id+"F0.wireOp",EDGE,"E229"),sQuery(id+"F0.wireOp",EDGE,"E230"),sQuery(id+"F0.wireOp",EDGE,"E231"),sQuery(id+"F0.wireOp",EDGE,"E232"),sQuery(id+"F0.wireOp",EDGE,"E233"),sQuery(id+"F0.wireOp",EDGE,"E234"),sQuery(id+"F0.wireOp",EDGE,"E235"),sQuery(id+"F0.wireOp",EDGE,"E236"),sQuery(id+"F0.wireOp",EDGE,"E237"),sQuery(id+"F0.wireOp",EDGE,"E238"),sQuery(id+"F0.wireOp",EDGE,"E239"),sQuery(id+"F0.wireOp",EDGE,"E240"),sQuery(id+"F0.wireOp",EDGE,"E241"),sQuery(id+"F0.wireOp",EDGE,"E242"),sQuery(id+"F0.wireOp",EDGE,"E243"),sQuery(id+"F0.wireOp",EDGE,"E244"),sQuery(id+"F0.wireOp",EDGE,"E245"),sQuery(id+"F0.wireOp",EDGE,"E246"),sQuery(id+"F0.wireOp",EDGE,"E247"),sQuery(id+"F0.wireOp",EDGE,"E248"),sQuery(id+"F0.wireOp",EDGE,"E249"),sQuery(id+"F0.wireOp",EDGE,"E250"),sQuery(id+"F0.wireOp",EDGE,"E251"),sQuery(id+"F0.wireOp",EDGE,"E252"),sQuery(id+"F0.wireOp",EDGE,"E253"),sQuery(id+"F0.wireOp",EDGE,"E254"),sQuery(id+"F0.wireOp",EDGE,"E255"),sQuery(id+"F0.wireOp",EDGE,"E256"),sQuery(id+"F0.wireOp",EDGE,"E257"),sQuery(id+"F0.wireOp",EDGE,"E258"),sQuery(id+"F0.wireOp",EDGE,"E259"),sQuery(id+"F0.wireOp",EDGE,"E260"),sQuery(id+"F0.wireOp",EDGE,"E261"),sQuery(id+"F0.wireOp",EDGE,"E262"),sQuery(id+"F0.wireOp",EDGE,"E263"),sQuery(id+"F0.wireOp",EDGE,"E264"),sQuery(id+"F0.wireOp",EDGE,"E265"),sQuery(id+"F0.wireOp",EDGE,"E266"),sQuery(id+"F0.wireOp",EDGE,"E267"),sQuery(id+"F0.wireOp",EDGE,"E268"),sQuery(id+"F0.wireOp",EDGE,"E269"),sQuery(id+"F0.wireOp",EDGE,"E270"),sQuery(id+"F0.wireOp",EDGE,"E271"),sQuery(id+"F0.wireOp",EDGE,"E272"),sQuery(id+"F0.wireOp",EDGE,"E273"),sQuery(id+"F0.wireOp",EDGE,"E274"),sQuery(id+"F0.wireOp",EDGE,"E275"),sQuery(id+"F0.wireOp",EDGE,"E276"),sQuery(id+"F0.wireOp",EDGE,"E277"),sQuery(id+"F0.wireOp",EDGE,"E278"),sQuery(id+"F0.wireOp",EDGE,"E279"),sQuery(id+"F0.wireOp",EDGE,"E280"),sQuery(id+"F0.wireOp",EDGE,"E281"),sQuery(id+"F0.wireOp",EDGE,"E282"),sQuery(id+"F0.wireOp",EDGE,"E283"),sQuery(id+"F0.wireOp",EDGE,"E284"),sQuery(id+"F0.wireOp",EDGE,"E285"),sQuery(id+"F0.wireOp",EDGE,"E286"),sQuery(id+"F0.wireOp",EDGE,"E287"),sQuery(id+"F0.wireOp",EDGE,"E288"),sQuery(id+"F0.wireOp",EDGE,"E289"),sQuery(id+"F0.wireOp",EDGE,"E290"),sQuery(id+"F0.wireOp",EDGE,"E291"),sQuery(id+"F0.wireOp",EDGE,"E292"),sQuery(id+"F0.wireOp",EDGE,"E293"),sQuery(id+"F0.wireOp",EDGE,"E294"),sQuery(id+"F0.wireOp",EDGE,"E295"),sQuery(id+"F0.wireOp",EDGE,"E296"),sQuery(id+"F0.wireOp",EDGE,"E297"),sQuery(id+"F0.wireOp",EDGE,"E298"),sQuery(id+"F0.wireOp",EDGE,"E299"),sQuery(id+"F0.wireOp",EDGE,"E300"),sQuery(id+"F0.wireOp",EDGE,"E301"),sQuery(id+"F0.wireOp",EDGE,"E302"),sQuery(id+"F0.wireOp",EDGE,"E303"),sQuery(id+"F0.wireOp",EDGE,"E304"),sQuery(id+"F0.wireOp",EDGE,"E305"),sQuery(id+"F0.wireOp",EDGE,"E306"),sQuery(id+"F0.wireOp",EDGE,"E307"),sQuery(id+"F0.wireOp",EDGE,"E308"),sQuery(id+"F0.wireOp",EDGE,"E309"),sQuery(id+"F0.wireOp",EDGE,"E310"),sQuery(id+"F0.wireOp",EDGE,"E311"),sQuery(id+"F0.wireOp",EDGE,"E312"),sQuery(id+"F0.wireOp",EDGE,"E313"),sQuery(id+"F0.wireOp",EDGE,"E314"),sQuery(id+"F0.wireOp",EDGE,"E315"),sQuery(id+"F0.wireOp",EDGE,"E316"),sQuery(id+"F0.wireOp",EDGE,"E317"),sQuery(id+"F0.wireOp",EDGE,"E318"),sQuery(id+"F0.wireOp",EDGE,"E319"),sQuery(id+"F0.wireOp",EDGE,"E320"),sQuery(id+"F0.wireOp",EDGE,"E321"),sQuery(id+"F0.wireOp",EDGE,"E322"),sQuery(id+"F0.wireOp",EDGE,"E323"),sQuery(id+"F0.wireOp",EDGE,"E324"),sQuery(id+"F0.wireOp",EDGE,"E325"),sQuery(id+"F0.wireOp",EDGE,"E326"),sQuery(id+"F0.wireOp",EDGE,"E327"),sQuery(id+"F0.wireOp",EDGE,"E328"),sQuery(id+"F0.wireOp",EDGE,"E329"),sQuery(id+"F0.wireOp",EDGE,"E330"),sQuery(id+"F0.wireOp",EDGE,"E331"),sQuery(id+"F0.wireOp",EDGE,"E332"),sQuery(id+"F0.wireOp",EDGE,"E333"),sQuery(id+"F0.wireOp",EDGE,"E334"),sQuery(id+"F0.wireOp",EDGE,"E335"),sQuery(id+"F0.wireOp",EDGE,"E336"),sQuery(id+"F0.wireOp",EDGE,"E337"),sQuery(id+"F0.wireOp",EDGE,"E338"),sQuery(id+"F0.wireOp",EDGE,"E339"),sQuery(id+"F0.wireOp",EDGE,"E340"),sQuery(id+"F0.wireOp",EDGE,"E341"),sQuery(id+"F0.wireOp",EDGE,"E342"),sQuery(id+"F0.wireOp",EDGE,"E343"),sQuery(id+"F0.wireOp",EDGE,"E344"),sQuery(id+"F0.wireOp",EDGE,"E345"),sQuery(id+"F0.wireOp",EDGE,"E346"),sQuery(id+"F0.wireOp",EDGE,"E347"),sQuery(id+"F0.wireOp",EDGE,"E348"),sQuery(id+"F0.wireOp",EDGE,"E349"),sQuery(id+"F0.wireOp",EDGE,"E350"),sQuery(id+"F0.wireOp",EDGE,"E351"),sQuery(id+"F0.wireOp",EDGE,"E352"),sQuery(id+"F0.wireOp",EDGE,"E353"),sQuery(id+"F0.wireOp",EDGE,"E354"),sQuery(id+"F0.wireOp",EDGE,"E355"),sQuery(id+"F0.wireOp",EDGE,"E356"),sQuery(id+"F0.wireOp",EDGE,"E357"),sQuery(id+"F0.wireOp",EDGE,"E358"),sQuery(id+"F0.wireOp",EDGE,"E359"),sQuery(id+"F0.wireOp",EDGE,"E360"),sQuery(id+"F0.wireOp",EDGE,"E361"),sQuery(id+"F0.wireOp",EDGE,"E362"),sQuery(id+"F0.wireOp",EDGE,"E363"),sQuery(id+"F0.wireOp",EDGE,"E364"),sQuery(id+"F0.wireOp",EDGE,"E365"),sQuery(id+"F0.wireOp",EDGE,"E366"),sQuery(id+"F0.wireOp",EDGE,"E367"),sQuery(id+"F0.wireOp",EDGE,"E368"),sQuery(id+"F0.wireOp",EDGE,"E369"),sQuery(id+"F0.wireOp",EDGE,"E370"),sQuery(id+"F0.wireOp",EDGE,"E371"),sQuery(id+"F0.wireOp",EDGE,"E372"),sQuery(id+"F0.wireOp",EDGE,"E373"),sQuery(id+"F0.wireOp",EDGE,"E374"),sQuery(id+"F0.wireOp",EDGE,"E375"),sQuery(id+"F0.wireOp",EDGE,"E376"),sQuery(id+"F0.wireOp",EDGE,"E377"),sQuery(id+"F0.wireOp",EDGE,"E378"),sQuery(id+"F0.wireOp",EDGE,"E379"),sQuery(id+"F0.wireOp",EDGE,"E380"),sQuery(id+"F0.wireOp",EDGE,"E381"),sQuery(id+"F0.wireOp",EDGE,"E382"),sQuery(id+"F0.wireOp",EDGE,"E383"),sQuery(id+"F0.wireOp",EDGE,"E384"),sQuery(id+"F0.wireOp",EDGE,"E385"),sQuery(id+"F0.wireOp",EDGE,"E386"),sQuery(id+"F0.wireOp",EDGE,"E387"),sQuery(id+"F0.wireOp",EDGE,"E388"),sQuery(id+"F0.wireOp",EDGE,"E389"),sQuery(id+"F0.wireOp",EDGE,"E390"),sQuery(id+"F0.wireOp",EDGE,"E391"),sQuery(id+"F0.wireOp",EDGE,"E392"),sQuery(id+"F0.wireOp",EDGE,"E393"),sQuery(id+"F0.wireOp",EDGE,"E394"),sQuery(id+"F0.wireOp",EDGE,"E395"),sQuery(id+"F0.wireOp",EDGE,"E396"),sQuery(id+"F0.wireOp",EDGE,"E397"),sQuery(id+"F0.wireOp",EDGE,"E398"),sQuery(id+"F0.wireOp",EDGE,"E399"),sQuery(id+"F0.wireOp",EDGE,"E400"),sQuery(id+"F0.wireOp",EDGE,"E401"),sQuery(id+"F0.wireOp",EDGE,"E402"),sQuery(id+"F0.wireOp",EDGE,"E403"),sQuery(id+"F0.wireOp",EDGE,"E404"),sQuery(id+"F0.wireOp",EDGE,"E405"),sQuery(id+"F0.wireOp",EDGE,"E406"),sQuery(id+"F0.wireOp",EDGE,"E407"),sQuery(id+"F0.wireOp",EDGE,"E408"),sQuery(id+"F0.wireOp",EDGE,"E409"),sQuery(id+"F0.wireOp",EDGE,"E410"),sQuery(id+"F0.wireOp",EDGE,"E411"),sQuery(id+"F0.wireOp",EDGE,"E412"),sQuery(id+"F0.wireOp",EDGE,"E413"),sQuery(id+"F0.wireOp",EDGE,"E414"),sQuery(id+"F0.wireOp",EDGE,"E415"),sQuery(id+"F0.wireOp",EDGE,"E416"),sQuery(id+"F0.wireOp",EDGE,"E417"),sQuery(id+"F0.wireOp",EDGE,"E418"),sQuery(id+"F0.wireOp",EDGE,"E419"),sQuery(id+"F0.wireOp",EDGE,"E420"),sQuery(id+"F0.wireOp",EDGE,"E421"),sQuery(id+"F0.wireOp",EDGE,"E422"),sQuery(id+"F0.wireOp",EDGE,"E423"),sQuery(id+"F0.wireOp",EDGE,"E424"),sQuery(id+"F0.wireOp",EDGE,"E425"),sQuery(id+"F0.wireOp",EDGE,"E426"),sQuery(id+"F0.wireOp",EDGE,"E427"),sQuery(id+"F0.wireOp",EDGE,"E428"),sQuery(id+"F0.wireOp",EDGE,"E429"),sQuery(id+"F0.wireOp",EDGE,"E430"),sQuery(id+"F0.wireOp",EDGE,"E431"),sQuery(id+"F0.wireOp",EDGE,"E432"),sQuery(id+"F0.wireOp",EDGE,"E433"),sQuery(id+"F0.wireOp",EDGE,"E434"),sQuery(id+"F0.wireOp",EDGE,"E435"),sQuery(id+"F0.wireOp",EDGE,"E436"),sQuery(id+"F0.wireOp",EDGE,"E437"),sQuery(id+"F0.wireOp",EDGE,"E438"),sQuery(id+"F0.wireOp",EDGE,"E439"),sQuery(id+"F0.wireOp",EDGE,"E440"),sQuery(id+"F0.wireOp",EDGE,"E441"),sQuery(id+"F0.wireOp",EDGE,"E442"),sQuery(id+"F0.wireOp",EDGE,"E443"),sQuery(id+"F0.wireOp",EDGE,"E444"),sQuery(id+"F0.wireOp",EDGE,"E445"),sQuery(id+"F0.wireOp",EDGE,"E446"),sQuery(id+"F0.wireOp",EDGE,"E447"),sQuery(id+"F0.wireOp",EDGE,"E448"),sQuery(id+"F0.wireOp",EDGE,"E449"),sQuery(id+"F0.wireOp",EDGE,"E450"),sQuery(id+"F0.wireOp",EDGE,"E451"),sQuery(id+"F0.wireOp",EDGE,"E452"),sQuery(id+"F0.wireOp",EDGE,"E453"),sQuery(id+"F0.wireOp",EDGE,"E454"),sQuery(id+"F0.wireOp",EDGE,"E455"),sQuery(id+"F0.wireOp",EDGE,"E456"),sQuery(id+"F0.wireOp",EDGE,"E457"),sQuery(id+"F0.wireOp",EDGE,"E458"),sQuery(id+"F0.wireOp",EDGE,"E459"),sQuery(id+"F0.wireOp",EDGE,"E460"),sQuery(id+"F0.wireOp",EDGE,"E461"),sQuery(id+"F0.wireOp",EDGE,"E462"),sQuery(id+"F0.wireOp",EDGE,"E463"),sQuery(id+"F0.wireOp",EDGE,"E464"),sQuery(id+"F0.wireOp",EDGE,"E465"),sQuery(id+"F0.wireOp",EDGE,"E466"),sQuery(id+"F0.wireOp",EDGE,"E467"),sQuery(id+"F0.wireOp",EDGE,"E468"),sQuery(id+"F0.wireOp",EDGE,"E469"),sQuery(id+"F0.wireOp",EDGE,"E470"),sQuery(id+"F0.wireOp",EDGE,"E471"),sQuery(id+"F0.wireOp",EDGE,"E472"),sQuery(id+"F0.wireOp",EDGE,"E473"),sQuery(id+"F0.wireOp",EDGE,"E474"),sQuery(id+"F0.wireOp",EDGE,"E475"),sQuery(id+"F0.wireOp",EDGE,"E476"),sQuery(id+"F0.wireOp",EDGE,"E477"),sQuery(id+"F0.wireOp",EDGE,"E478"),sQuery(id+"F0.wireOp",EDGE,"E479"),sQuery(id+"F0.wireOp",EDGE,"E480"),sQuery(id+"F0.wireOp",EDGE,"E481"),sQuery(id+"F0.wireOp",EDGE,"E482"),sQuery(id+"F0.wireOp",EDGE,"E483"),sQuery(id+"F0.wireOp",EDGE,"E484"),sQuery(id+"F0.wireOp",EDGE,"E485"),sQuery(id+"F0.wireOp",EDGE,"E486"),sQuery(id+"F0.wireOp",EDGE,"E487"),sQuery(id+"F0.wireOp",EDGE,"E488"),sQuery(id+"F0.wireOp",EDGE,"E489"),sQuery(id+"F0.wireOp",EDGE,"E490"),sQuery(id+"F0.wireOp",EDGE,"E491"),sQuery(id+"F0.wireOp",EDGE,"E492"),sQuery(id+"F0.wireOp",EDGE,"E493"),sQuery(id+"F0.wireOp",EDGE,"E494"),sQuery(id+"F0.wireOp",EDGE,"E495"),sQuery(id+"F0.wireOp",EDGE,"E496"),sQuery(id+"F0.wireOp",EDGE,"E497"),sQuery(id+"F0.wireOp",EDGE,"E498"),sQuery(id+"F0.wireOp",EDGE,"E499"),sQuery(id+"F0.wireOp",EDGE,"E500"),sQuery(id+"F0.wireOp",EDGE,"E501"),sQuery(id+"F0.wireOp",EDGE,"E502"),sQuery(id+"F0.wireOp",EDGE,"E503"),sQuery(id+"F0.wireOp",EDGE,"E504"),sQuery(id+"F0.wireOp",EDGE,"E505"),sQuery(id+"F0.wireOp",EDGE,"E506"),sQuery(id+"F0.wireOp",EDGE,"E507"),sQuery(id+"F0.wireOp",EDGE,"E508"),sQuery(id+"F0.wireOp",EDGE,"E509"),sQuery(id+"F0.wireOp",EDGE,"E510"),sQuery(id+"F0.wireOp",EDGE,"E511"),sQuery(id+"F0.wireOp",EDGE,"E512"),sQuery(id+"F0.wireOp",EDGE,"E513"),sQuery(id+"F0.wireOp",EDGE,"E514"),sQuery(id+"F0.wireOp",EDGE,"E515"),sQuery(id+"F0.wireOp",EDGE,"E516"),sQuery(id+"F0.wireOp",EDGE,"E517"),sQuery(id+"F0.wireOp",EDGE,"E518"),sQuery(id+"F0.wireOp",EDGE,"E519"),sQuery(id+"F0.wireOp",EDGE,"E520"),sQuery(id+"F0.wireOp",EDGE,"E521"),sQuery(id+"F0.wireOp",EDGE,"E522"),sQuery(id+"F0.wireOp",EDGE,"E523"),sQuery(id+"F0.wireOp",EDGE,"E524"),sQuery(id+"F0.wireOp",EDGE,"E525"),sQuery(id+"F0.wireOp",EDGE,"E526"),sQuery(id+"F0.wireOp",EDGE,"E527"),sQuery(id+"F0.wireOp",EDGE,"E528"),sQuery(id+"F0.wireOp",EDGE,"E529"),sQuery(id+"F0.wireOp",EDGE,"E530"),sQuery(id+"F0.wireOp",EDGE,"E531"),sQuery(id+"F0.wireOp",EDGE,"E532"),sQuery(id+"F0.wireOp",EDGE,"E533"),sQuery(id+"F0.wireOp",EDGE,"E534"),sQuery(id+"F0.wireOp",EDGE,"E535"),sQuery(id+"F0.wireOp",EDGE,"E536"),sQuery(id+"F0.wireOp",EDGE,"E537"),sQuery(id+"F0.wireOp",EDGE,"E538"),sQuery(id+"F0.wireOp",EDGE,"E539"),sQuery(id+"F0.wireOp",EDGE,"E540"),sQuery(id+"F0.wireOp",EDGE,"E541"),sQuery(id+"F0.wireOp",EDGE,"E542"),sQuery(id+"F0.wireOp",EDGE,"E543"),sQuery(id+"F0.wireOp",EDGE,"E544"),sQuery(id+"F0.wireOp",EDGE,"E545"),sQuery(id+"F0.wireOp",EDGE,"E546"),sQuery(id+"F0.wireOp",EDGE,"E547"),sQuery(id+"F0.wireOp",EDGE,"E548"),sQuery(id+"F0.wireOp",EDGE,"E549"),sQuery(id+"F0.wireOp",EDGE,"E550"),sQuery(id+"F0.wireOp",EDGE,"E551"),sQuery(id+"F0.wireOp",EDGE,"E552"),sQuery(id+"F0.wireOp",EDGE,"E553"),sQuery(id+"F0.wireOp",EDGE,"E554"),sQuery(id+"F0.wireOp",EDGE,"E555"),sQuery(id+"F0.wireOp",EDGE,"E556"),sQuery(id+"F0.wireOp",EDGE,"E557"),sQuery(id+"F0.wireOp",EDGE,"E558"),sQuery(id+"F0.wireOp",EDGE,"E559"),sQuery(id+"F0.wireOp",EDGE,"E560"),sQuery(id+"F0.wireOp",EDGE,"E561"),sQuery(id+"F0.wireOp",EDGE,"E562"),sQuery(id+"F0.wireOp",EDGE,"E563"),sQuery(id+"F0.wireOp",EDGE,"E564"),sQuery(id+"F0.wireOp",EDGE,"E565"),sQuery(id+"F0.wireOp",EDGE,"E566"),sQuery(id+"F0.wireOp",EDGE,"E567"),sQuery(id+"F0.wireOp",EDGE,"E568"),sQuery(id+"F0.wireOp",EDGE,"E569"),sQuery(id+"F0.wireOp",EDGE,"E570"),sQuery(id+"F0.wireOp",EDGE,"E571"),sQuery(id+"F0.wireOp",EDGE,"E572"),sQuery(id+"F0.wireOp",EDGE,"E573"),sQuery(id+"F0.wireOp",EDGE,"E574"),sQuery(id+"F0.wireOp",EDGE,"E575"),sQuery(id+"F0.wireOp",EDGE,"E576"),sQuery(id+"F0.wireOp",EDGE,"E577"),sQuery(id+"F0.wireOp",EDGE,"E578"),sQuery(id+"F0.wireOp",EDGE,"E579"),sQuery(id+"F0.wireOp",EDGE,"E580"),sQuery(id+"F0.wireOp",EDGE,"E581"),sQuery(id+"F0.wireOp",EDGE,"E582"),sQuery(id+"F0.wireOp",EDGE,"E583"),sQuery(id+"F0.wireOp",EDGE,"E584"),sQuery(id+"F0.wireOp",EDGE,"E585"),sQuery(id+"F0.wireOp",EDGE,"E586"),sQuery(id+"F0.wireOp",EDGE,"E587"),sQuery(id+"F0.wireOp",EDGE,"E588"),sQuery(id+"F0.wireOp",EDGE,"E589"),sQuery(id+"F0.wireOp",EDGE,"E590"),sQuery(id+"F0.wireOp",EDGE,"E591"),sQuery(id+"F0.wireOp",EDGE,"E592"),sQuery(id+"F0.wireOp",EDGE,"E593"),sQuery(id+"F0.wireOp",EDGE,"E594"),sQuery(id+"F0.wireOp",EDGE,"E595"),sQuery(id+"F0.wireOp",EDGE,"E596"),sQuery(id+"F0.wireOp",EDGE,"E597"),sQuery(id+"F0.wireOp",EDGE,"E598"),sQuery(id+"F0.wireOp",EDGE,"E599"),sQuery(id+"F0.wireOp",EDGE,"E600"),sQuery(id+"F0.wireOp",EDGE,"E601"),sQuery(id+"F0.wireOp",EDGE,"E602"),sQuery(id+"F0.wireOp",EDGE,"E603"),sQuery(id+"F0.wireOp",EDGE,"E604"),sQuery(id+"F0.wireOp",EDGE,"E605"),sQuery(id+"F0.wireOp",EDGE,"E606"),sQuery(id+"F0.wireOp",EDGE,"E607"),sQuery(id+"F0.wireOp",EDGE,"E608"),sQuery(id+"F0.wireOp",EDGE,"E609"),sQuery(id+"F0.wireOp",EDGE,"E610"),sQuery(id+"F0.wireOp",EDGE,"E611"),sQuery(id+"F0.wireOp",EDGE,"E612"),sQuery(id+"F0.wireOp",EDGE,"E613"),sQuery(id+"F0.wireOp",EDGE,"E614"),sQuery(id+"F0.wireOp",EDGE,"E615"),sQuery(id+"F0.wireOp",EDGE,"E616"),sQuery(id+"F0.wireOp",EDGE,"E617"),sQuery(id+"F0.wireOp",EDGE,"E618"),sQuery(id+"F0.wireOp",EDGE,"E619"),sQuery(id+"F0.wireOp",EDGE,"E620"),sQuery(id+"F0.wireOp",EDGE,"E621"),sQuery(id+"F0.wireOp",EDGE,"E622"),sQuery(id+"F0.wireOp",EDGE,"E623"),sQuery(id+"F0.wireOp",EDGE,"E624"),sQuery(id+"F0.wireOp",EDGE,"E625"),sQuery(id+"F0.wireOp",EDGE,"E626"),sQuery(id+"F0.wireOp",EDGE,"E627"),sQuery(id+"F0.wireOp",EDGE,"E628"),sQuery(id+"F0.wireOp",EDGE,"E629"),sQuery(id+"F0.wireOp",EDGE,"E630"),sQuery(id+"F0.wireOp",EDGE,"E631"),sQuery(id+"F0.wireOp",EDGE,"E632"),sQuery(id+"F0.wireOp",EDGE,"E633"),sQuery(id+"F0.wireOp",EDGE,"E634"),sQuery(id+"F0.wireOp",EDGE,"E635"),sQuery(id+"F0.wireOp",EDGE,"E636"),sQuery(id+"F0.wireOp",EDGE,"E637"),sQuery(id+"F0.wireOp",EDGE,"E638"),sQuery(id+"F0.wireOp",EDGE,"E639"),sQuery(id+"F0.wireOp",EDGE,"E640"),sQuery(id+"F0.wireOp",EDGE,"E641"),sQuery(id+"F0.wireOp",EDGE,"E642"),sQuery(id+"F0.wireOp",EDGE,"E643"),sQuery(id+"F0.wireOp",EDGE,"E644"),sQuery(id+"F0.wireOp",EDGE,"E645"),sQuery(id+"F0.wireOp",EDGE,"E646"),sQuery(id+"F0.wireOp",EDGE,"E647"),sQuery(id+"F0.wireOp",EDGE,"E648"),sQuery(id+"F0.wireOp",EDGE,"E649"),sQuery(id+"F0.wireOp",EDGE,"E650"),sQuery(id+"F0.wireOp",EDGE,"E651"),sQuery(id+"F0.wireOp",EDGE,"E652"),sQuery(id+"F0.wireOp",EDGE,"E653"),sQuery(id+"F0.wireOp",EDGE,"E654"),sQuery(id+"F0.wireOp",EDGE,"E655"),sQuery(id+"F0.wireOp",EDGE,"E656"),sQuery(id+"F0.wireOp",EDGE,"E657"),sQuery(id+"F0.wireOp",EDGE,"E658"),sQuery(id+"F0.wireOp",EDGE,"E659"),sQuery(id+"F0.wireOp",EDGE,"E660"),sQuery(id+"F0.wireOp",EDGE,"E661"),sQuery(id+"F0.wireOp",EDGE,"E662"),sQuery(id+"F0.wireOp",EDGE,"E663"),sQuery(id+"F0.wireOp",EDGE,"E664"),sQuery(id+"F0.wireOp",EDGE,"E665"),sQuery(id+"F0.wireOp",EDGE,"E666"),sQuery(id+"F0.wireOp",EDGE,"E667"),sQuery(id+"F0.wireOp",EDGE,"E668"),sQuery(id+"F0.wireOp",EDGE,"E669"),sQuery(id+"F0.wireOp",EDGE,"E670"),sQuery(id+"F0.wireOp",EDGE,"E671"),sQuery(id+"F0.wireOp",EDGE,"E672"),sQuery(id+"F0.wireOp",EDGE,"E673"),sQuery(id+"F0.wireOp",EDGE,"E674"),sQuery(id+"F0.wireOp",EDGE,"E675"),sQuery(id+"F0.wireOp",EDGE,"E676"),sQuery(id+"F0.wireOp",EDGE,"E677"),sQuery(id+"F0.wireOp",EDGE,"E678"),sQuery(id+"F0.wireOp",EDGE,"E679"),sQuery(id+"F0.wireOp",EDGE,"E680"),sQuery(id+"F0.wireOp",EDGE,"E681"),sQuery(id+"F0.wireOp",EDGE,"E682"),sQuery(id+"F0.wireOp",EDGE,"E683"),sQuery(id+"F0.wireOp",EDGE,"E684"),sQuery(id+"F0.wireOp",EDGE,"E685"),sQuery(id+"F0.wireOp",EDGE,"E686"),sQuery(id+"F0.wireOp",EDGE,"E687"),sQuery(id+"F0.wireOp",EDGE,"E688"),sQuery(id+"F0.wireOp",EDGE,"E689"),sQuery(id+"F0.wireOp",EDGE,"E690"),sQuery(id+"F0.wireOp",EDGE,"E691"),sQuery(id+"F0.wireOp",EDGE,"E692"),sQuery(id+"F0.wireOp",EDGE,"E693"),sQuery(id+"F0.wireOp",EDGE,"E694"),sQuery(id+"F0.wireOp",EDGE,"E695"),sQuery(id+"F0.wireOp",EDGE,"E696"),sQuery(id+"F0.wireOp",EDGE,"E697"),sQuery(id+"F0.wireOp",EDGE,"E698"),sQuery(id+"F0.wireOp",EDGE,"E699"),sQuery(id+"F0.wireOp",EDGE,"E700"),sQuery(id+"F0.wireOp",EDGE,"E701"),sQuery(id+"F0.wireOp",EDGE,"E702"),sQuery(id+"F0.wireOp",EDGE,"E703"),sQuery(id+"F0.wireOp",EDGE,"E704"),sQuery(id+"F0.wireOp",EDGE,"E705"),sQuery(id+"F0.wireOp",EDGE,"E706"),sQuery(id+"F0.wireOp",EDGE,"E707"),sQuery(id+"F0.wireOp",EDGE,"E708"),sQuery(id+"F0.wireOp",EDGE,"E709"),sQuery(id+"F0.wireOp",EDGE,"E710"),sQuery(id+"F0.wireOp",EDGE,"E711"),sQuery(id+"F0.wireOp",EDGE,"E712"),sQuery(id+"F0.wireOp",EDGE,"E713"),sQuery(id+"F0.wireOp",EDGE,"E714"),sQuery(id+"F0.wireOp",EDGE,"E715"),sQuery(id+"F0.wireOp",EDGE,"E716"),sQuery(id+"F0.wireOp",EDGE,"E717"),sQuery(id+"F0.wireOp",EDGE,"E718"),sQuery(id+"F0.wireOp",EDGE,"E719"),sQuery(id+"F0.wireOp",EDGE,"E720"),sQuery(id+"F0.wireOp",EDGE,"E721"),sQuery(id+"F0.wireOp",EDGE,"E722"),sQuery(id+"F0.wireOp",EDGE,"E723"),sQuery(id+"F0.wireOp",EDGE,"E724"),sQuery(id+"F0.wireOp",EDGE,"E725"),sQuery(id+"F0.wireOp",EDGE,"E726"),sQuery(id+"F0.wireOp",EDGE,"E727"),sQuery(id+"F0.wireOp",EDGE,"E728"),sQuery(id+"F0.wireOp",EDGE,"E729"),sQuery(id+"F0.wireOp",EDGE,"E730"),sQuery(id+"F0.wireOp",EDGE,"E731"),sQuery(id+"F0.wireOp",EDGE,"E732"),sQuery(id+"F0.wireOp",EDGE,"E733"),sQuery(id+"F0.wireOp",EDGE,"E734"),sQuery(id+"F0.wireOp",EDGE,"E735"),sQuery(id+"F0.wireOp",EDGE,"E736"),sQuery(id+"F0.wireOp",EDGE,"E737"),sQuery(id+"F0.wireOp",EDGE,"E738"),sQuery(id+"F0.wireOp",EDGE,"E739"),sQuery(id+"F0.wireOp",EDGE,"E740"),sQuery(id+"F0.wireOp",EDGE,"E741"),sQuery(id+"F0.wireOp",EDGE,"E742"),sQuery(id+"F0.wireOp",EDGE,"E743"),sQuery(id+"F0.wireOp",EDGE,"E744"),sQuery(id+"F0.wireOp",EDGE,"E745"),sQuery(id+"F0.wireOp",EDGE,"E746"),sQuery(id+"F0.wireOp",EDGE,"E747"),sQuery(id+"F0.wireOp",EDGE,"E748"),sQuery(id+"F0.wireOp",EDGE,"E749"),sQuery(id+"F0.wireOp",EDGE,"E750"),sQuery(id+"F0.wireOp",EDGE,"E751"),sQuery(id+"F0.wireOp",EDGE,"E752"),sQuery(id+"F0.wireOp",EDGE,"E753"),sQuery(id+"F0.wireOp",EDGE,"E754"),sQuery(id+"F0.wireOp",EDGE,"E755"),sQuery(id+"F0.wireOp",EDGE,"E756"),sQuery(id+"F0.wireOp",EDGE,"E757"),sQuery(id+"F0.wireOp",EDGE,"E758"),sQuery(id+"F0.wireOp",EDGE,"E759"),sQuery(id+"F0.wireOp",EDGE,"E760"),sQuery(id+"F0.wireOp",EDGE,"E761"),sQuery(id+"F0.wireOp",EDGE,"E762"),sQuery(id+"F0.wireOp",EDGE,"E763"),sQuery(id+"F0.wireOp",EDGE,"E764"),sQuery(id+"F0.wireOp",EDGE,"E765"),sQuery(id+"F0.wireOp",EDGE,"E766"),sQuery(id+"F0.wireOp",EDGE,"E767"),sQuery(id+"F0.wireOp",EDGE,"E768"),sQuery(id+"F0.wireOp",EDGE,"E769"),sQuery(id+"F0.wireOp",EDGE,"E770"),sQuery(id+"F0.wireOp",EDGE,"E771"),sQuery(id+"F0.wireOp",EDGE,"E772"),sQuery(id+"F0.wireOp",EDGE,"E773"),sQuery(id+"F0.wireOp",EDGE,"E774"),sQuery(id+"F0.wireOp",EDGE,"E775"),sQuery(id+"F0.wireOp",EDGE,"E776"),sQuery(id+"F0.wireOp",EDGE,"E777"),sQuery(id+"F0.wireOp",EDGE,"E778"),sQuery(id+"F0.wireOp",EDGE,"E779"),sQuery(id+"F0.wireOp",EDGE,"E780"),sQuery(id+"F0.wireOp",EDGE,"E781"),sQuery(id+"F0.wireOp",EDGE,"E782"),sQuery(id+"F0.wireOp",EDGE,"E783"),sQuery(id+"F0.wireOp",EDGE,"E784"),sQuery(id+"F0.wireOp",EDGE,"E785"),sQuery(id+"F0.wireOp",EDGE,"E786"),sQuery(id+"F0.wireOp",EDGE,"E787"),sQuery(id+"F0.wireOp",EDGE,"E788"),sQuery(id+"F0.wireOp",EDGE,"E789"),sQuery(id+"F0.wireOp",EDGE,"E790"),sQuery(id+"F0.wireOp",EDGE,"E791"),sQuery(id+"F0.wireOp",EDGE,"E792"),sQuery(id+"F0.wireOp",EDGE,"E793"),sQuery(id+"F0.wireOp",EDGE,"E794"),sQuery(id+"F0.wireOp",EDGE,"E795"),sQuery(id+"F0.wireOp",EDGE,"E796"),sQuery(id+"F0.wireOp",EDGE,"E797"),sQuery(id+"F0.wireOp",EDGE,"E798"),sQuery(id+"F0.wireOp",EDGE,"E799"),sQuery(id+"F0.wireOp",EDGE,"E800"),sQuery(id+"F0.wireOp",EDGE,"E801"),sQuery(id+"F0.wireOp",EDGE,"E802"),sQuery(id+"F0.wireOp",EDGE,"E803"),sQuery(id+"F0.wireOp",EDGE,"E804"),sQuery(id+"F0.wireOp",EDGE,"E805"),sQuery(id+"F0.wireOp",EDGE,"E806"),sQuery(id+"F0.wireOp",EDGE,"E807"),sQuery(id+"F0.wireOp",EDGE,"E808"),sQuery(id+"F0.wireOp",EDGE,"E809"),sQuery(id+"F0.wireOp",EDGE,"E810"),sQuery(id+"F0.wireOp",EDGE,"E811"),sQuery(id+"F0.wireOp",EDGE,"E812"),sQuery(id+"F0.wireOp",EDGE,"E813"),sQuery(id+"F0.wireOp",EDGE,"E814"),sQuery(id+"F0.wireOp",EDGE,"E815"),sQuery(id+"F0.wireOp",EDGE,"E816"),sQuery(id+"F0.wireOp",EDGE,"E817"),sQuery(id+"F0.wireOp",EDGE,"E818"),sQuery(id+"F0.wireOp",EDGE,"E819"),sQuery(id+"F0.wireOp",EDGE,"E820"),sQuery(id+"F0.wireOp",EDGE,"E821"),sQuery(id+"F0.wireOp",EDGE,"E822"),sQuery(id+"F0.wireOp",EDGE,"E823"),sQuery(id+"F0.wireOp",EDGE,"E824"),sQuery(id+"F0.wireOp",EDGE,"E825"),sQuery(id+"F0.wireOp",EDGE,"E826"),sQuery(id+"F0.wireOp",EDGE,"E827"),sQuery(id+"F0.wireOp",EDGE,"E828"),sQuery(id+"F0.wireOp",EDGE,"E829"),sQuery(id+"F0.wireOp",EDGE,"E830"),sQuery(id+"F0.wireOp",EDGE,"E831"),sQuery(id+"F0.wireOp",EDGE,"E832"),sQuery(id+"F0.wireOp",EDGE,"E833"),sQuery(id+"F0.wireOp",EDGE,"E834"),sQuery(id+"F0.wireOp",EDGE,"E835"),sQuery(id+"F0.wireOp",EDGE,"E836"),sQuery(id+"F0.wireOp",EDGE,"E837"),sQuery(id+"F0.wireOp",EDGE,"E838"),sQuery(id+"F0.wireOp",EDGE,"E839"),sQuery(id+"F0.wireOp",EDGE,"E840"),sQuery(id+"F0.wireOp",EDGE,"E841"),sQuery(id+"F0.wireOp",EDGE,"E842"),sQuery(id+"F0.wireOp",EDGE,"E843"),sQuery(id+"F0.wireOp",EDGE,"E844"),sQuery(id+"F0.wireOp",EDGE,"E845"),sQuery(id+"F0.wireOp",EDGE,"E846"),sQuery(id+"F0.wireOp",EDGE,"E847"),sQuery(id+"F0.wireOp",EDGE,"E848"),sQuery(id+"F0.wireOp",EDGE,"E849"),sQuery(id+"F0.wireOp",EDGE,"E850"),sQuery(id+"F0.wireOp",EDGE,"E851"),sQuery(id+"F0.wireOp",EDGE,"E852"),sQuery(id+"F0.wireOp",EDGE,"E853"),sQuery(id+"F0.wireOp",EDGE,"E854"),sQuery(id+"F0.wireOp",EDGE,"E855"),sQuery(id+"F0.wireOp",EDGE,"E856"),sQuery(id+"F0.wireOp",EDGE,"E857"),sQuery(id+"F0.wireOp",EDGE,"E858"),sQuery(id+"F0.wireOp",EDGE,"E859"),sQuery(id+"F0.wireOp",EDGE,"E860"),sQuery(id+"F0.wireOp",EDGE,"E861"),sQuery(id+"F0.wireOp",EDGE,"E862"),sQuery(id+"F0.wireOp",EDGE,"E863"),sQuery(id+"F0.wireOp",EDGE,"E864"),sQuery(id+"F0.wireOp",EDGE,"E865"),sQuery(id+"F0.wireOp",EDGE,"E866"),sQuery(id+"F0.wireOp",EDGE,"E867"),sQuery(id+"F0.wireOp",EDGE,"E868"),sQuery(id+"F0.wireOp",EDGE,"E869"),sQuery(id+"F0.wireOp",EDGE,"E870"),sQuery(id+"F0.wireOp",EDGE,"E871"),sQuery(id+"F0.wireOp",EDGE,"E872"),sQuery(id+"F0.wireOp",EDGE,"E873"),sQuery(id+"F0.wireOp",EDGE,"E874"),sQuery(id+"F0.wireOp",EDGE,"E875"),sQuery(id+"F0.wireOp",EDGE,"E876"),sQuery(id+"F0.wireOp",EDGE,"E877"),sQuery(id+"F0.wireOp",EDGE,"E878"),sQuery(id+"F0.wireOp",EDGE,"E879"),sQuery(id+"F0.wireOp",EDGE,"E880"),sQuery(id+"F0.wireOp",EDGE,"E881"),sQuery(id+"F0.wireOp",EDGE,"E882"),sQuery(id+"F0.wireOp",EDGE,"E883"),sQuery(id+"F0.wireOp",EDGE,"E884"),sQuery(id+"F0.wireOp",EDGE,"E885"),sQuery(id+"F0.wireOp",EDGE,"E886"),sQuery(id+"F0.wireOp",EDGE,"E887"),sQuery(id+"F0.wireOp",EDGE,"E888"),sQuery(id+"F0.wireOp",EDGE,"E889"),sQuery(id+"F0.wireOp",EDGE,"E890"),sQuery(id+"F0.wireOp",EDGE,"E891"),sQuery(id+"F0.wireOp",EDGE,"E892"),sQuery(id+"F0.wireOp",EDGE,"E893"),sQuery(id+"F0.wireOp",EDGE,"E894"),sQuery(id+"F0.wireOp",EDGE,"E895"),sQuery(id+"F0.wireOp",EDGE,"E896"),sQuery(id+"F0.wireOp",EDGE,"E897"),sQuery(id+"F0.wireOp",EDGE,"E898"),sQuery(id+"F0.wireOp",EDGE,"E899"),sQuery(id+"F0.wireOp",EDGE,"E900"),sQuery(id+"F0.wireOp",EDGE,"E901"),sQuery(id+"F0.wireOp",EDGE,"E902"),sQuery(id+"F0.wireOp",EDGE,"E903"),sQuery(id+"F0.wireOp",EDGE,"E904"),sQuery(id+"F0.wireOp",EDGE,"E905"),sQuery(id+"F0.wireOp",EDGE,"E906"),sQuery(id+"F0.wireOp",EDGE,"E907"),sQuery(id+"F0.wireOp",EDGE,"E908"),sQuery(id+"F0.wireOp",EDGE,"E909"),sQuery(id+"F0.wireOp",EDGE,"E910"),sQuery(id+"F0.wireOp",EDGE,"E911"),sQuery(id+"F0.wireOp",EDGE,"E912"),sQuery(id+"F0.wireOp",EDGE,"E913"),sQuery(id+"F0.wireOp",EDGE,"E914"),sQuery(id+"F0.wireOp",EDGE,"E915"),sQuery(id+"F0.wireOp",EDGE,"E916"),sQuery(id+"F0.wireOp",EDGE,"E917"),sQuery(id+"F0.wireOp",EDGE,"E918"),sQuery(id+"F0.wireOp",EDGE,"E919"),sQuery(id+"F0.wireOp",EDGE,"E920"),sQuery(id+"F0.wireOp",EDGE,"E921"),sQuery(id+"F0.wireOp",EDGE,"E922"),sQuery(id+"F0.wireOp",EDGE,"E923"),sQuery(id+"F0.wireOp",EDGE,"E924"),sQuery(id+"F0.wireOp",EDGE,"E925"),sQuery(id+"F0.wireOp",EDGE,"E926"),sQuery(id+"F0.wireOp",EDGE,"E927"),sQuery(id+"F0.wireOp",EDGE,"E928"),sQuery(id+"F0.wireOp",EDGE,"E929"),sQuery(id+"F0.wireOp",EDGE,"E930"),sQuery(id+"F0.wireOp",EDGE,"E931"),sQuery(id+"F0.wireOp",EDGE,"E932"),sQuery(id+"F0.wireOp",EDGE,"E933"),sQuery(id+"F0.wireOp",EDGE,"E934"),sQuery(id+"F0.wireOp",EDGE,"E935"),sQuery(id+"F0.wireOp",EDGE,"E936"),sQuery(id+"F0.wireOp",EDGE,"E937"),sQuery(id+"F0.wireOp",EDGE,"E938"),sQuery(id+"F0.wireOp",EDGE,"E939"),sQuery(id+"F0.wireOp",EDGE,"E940"),sQuery(id+"F0.wireOp",EDGE,"E941"),sQuery(id+"F0.wireOp",EDGE,"E942"),sQuery(id+"F0.wireOp",EDGE,"E943"),sQuery(id+"F0.wireOp",EDGE,"E944"),sQuery(id+"F0.wireOp",EDGE,"E945"),sQuery(id+"F0.wireOp",EDGE,"E946"),sQuery(id+"F0.wireOp",EDGE,"E947"),sQuery(id+"F0.wireOp",EDGE,"E948"),sQuery(id+"F0.wireOp",EDGE,"E949"),sQuery(id+"F0.wireOp",EDGE,"E950"),sQuery(id+"F0.wireOp",EDGE,"E951"),sQuery(id+"F0.wireOp",EDGE,"E952"),sQuery(id+"F0.wireOp",EDGE,"E953"),sQuery(id+"F0.wireOp",EDGE,"E954"),sQuery(id+"F0.wireOp",EDGE,"E955"),sQuery(id+"F0.wireOp",EDGE,"E956"),sQuery(id+"F0.wireOp",EDGE,"E957"),sQuery(id+"F0.wireOp",EDGE,"E958"),sQuery(id+"F0.wireOp",EDGE,"E959"),sQuery(id+"F0.wireOp",EDGE,"E960"),sQuery(id+"F0.wireOp",EDGE,"E961"),sQuery(id+"F0.wireOp",EDGE,"E962"),sQuery(id+"F0.wireOp",EDGE,"E963"),sQuery(id+"F0.wireOp",EDGE,"E964"),sQuery(id+"F0.wireOp",EDGE,"E965"),sQuery(id+"F0.wireOp",EDGE,"E966"),sQuery(id+"F0.wireOp",EDGE,"E967"),sQuery(id+"F0.wireOp",EDGE,"E968"),sQuery(id+"F0.wireOp",EDGE,"E969"),sQuery(id+"F0.wireOp",EDGE,"E970"),sQuery(id+"F0.wireOp",EDGE,"E971"),sQuery(id+"F0.wireOp",EDGE,"E972"),sQuery(id+"F0.wireOp",EDGE,"E973"),sQuery(id+"F0.wireOp",EDGE,"E974"),sQuery(id+"F0.wireOp",EDGE,"E975"),sQuery(id+"F0.wireOp",EDGE,"E976"),sQuery(id+"F0.wireOp",EDGE,"E977"),sQuery(id+"F0.wireOp",EDGE,"E978"),sQuery(id+"F0.wireOp",EDGE,"E979"),sQuery(id+"F0.wireOp",EDGE,"E980"),sQuery(id+"F0.wireOp",EDGE,"E981"),sQuery(id+"F0.wireOp",EDGE,"E982"),sQuery(id+"F0.wireOp",EDGE,"E983"),sQuery(id+"F0.wireOp",EDGE,"E984"),sQuery(id+"F0.wireOp",EDGE,"E985"),sQuery(id+"F0.wireOp",EDGE,"E986"),sQuery(id+"F0.wireOp",EDGE,"E987"),sQuery(id+"F0.wireOp",EDGE,"E988"),sQuery(id+"F0.wireOp",EDGE,"E989"),sQuery(id+"F0.wireOp",EDGE,"E990"),sQuery(id+"F0.wireOp",EDGE,"E991"),sQuery(id+"F0.wireOp",EDGE,"E992"),sQuery(id+"F0.wireOp",EDGE,"E993"),sQuery(id+"F0.wireOp",EDGE,"E994"),sQuery(id+"F0.wireOp",EDGE,"E995"),sQuery(id+"F0.wireOp",EDGE,"E996"),sQuery(id+"F0.wireOp",EDGE,"E997"),sQuery(id+"F0.wireOp",EDGE,"E998"),sQuery(id+"F0.wireOp",EDGE,"E999"),sQuery(id+"F0.wireOp",EDGE,"E1000"),sQuery(id+"F0.wireOp",EDGE,"E1001"),sQuery(id+"F0.wireOp",EDGE,"E1002"),sQuery(id+"F0.wireOp",EDGE,"E1003"),sQuery(id+"F0.wireOp",EDGE,"E1004"),sQuery(id+"F0.wireOp",EDGE,"E1005"),sQuery(id+"F0.wireOp",EDGE,"E1006"),sQuery(id+"F0.wireOp",EDGE,"E1007"),sQuery(id+"F0.wireOp",EDGE,"E1008"),sQuery(id+"F0.wireOp",EDGE,"E1009"),sQuery(id+"F0.wireOp",EDGE,"E1010"),sQuery(id+"F0.wireOp",EDGE,"E1011"),sQuery(id+"F0.wireOp",EDGE,"E1012"),sQuery(id+"F0.wireOp",EDGE,"E1013"),sQuery(id+"F0.wireOp",EDGE,"E1014"),sQuery(id+"F0.wireOp",EDGE,"E1015"),sQuery(id+"F0.wireOp",EDGE,"E1016"),sQuery(id+"F0.wireOp",EDGE,"E1017"),sQuery(id+"F0.wireOp",EDGE,"E1018"),sQuery(id+"F0.wireOp",EDGE,"E1019"),sQuery(id+"F0.wireOp",EDGE,"E1020"),sQuery(id+"F0.wireOp",EDGE,"E1021"),sQuery(id+"F0.wireOp",EDGE,"E1022"),sQuery(id+"F0.wireOp",EDGE,"E1023"),sQuery(id+"F0.wireOp",EDGE,"E1024"),sQuery(id+"F0.wireOp",EDGE,"E1025"),sQuery(id+"F0.wireOp",EDGE,"E1026"),sQuery(id+"F0.wireOp",EDGE,"E1027"),sQuery(id+"F0.wireOp",EDGE,"E1028"),sQuery(id+"F0.wireOp",EDGE,"E1029"),sQuery(id+"F0.wireOp",EDGE,"E1030"),sQuery(id+"F0.wireOp",EDGE,"E1031"),sQuery(id+"F0.wireOp",EDGE,"E1032"),sQuery(id+"F0.wireOp",EDGE,"E1033"),sQuery(id+"F0.wireOp",EDGE,"E1034"),sQuery(id+"F0.wireOp",EDGE,"E1035"),sQuery(id+"F0.wireOp",EDGE,"E1036"),sQuery(id+"F0.wireOp",EDGE,"E1037"),sQuery(id+"F0.wireOp",EDGE,"E1038"),sQuery(id+"F0.wireOp",EDGE,"E1039"),sQuery(id+"F0.wireOp",EDGE,"E1040"),sQuery(id+"F0.wireOp",EDGE,"E1041"),sQuery(id+"F0.wireOp",EDGE,"E1042"),sQuery(id+"F0.wireOp",EDGE,"E1043"),sQuery(id+"F0.wireOp",EDGE,"E1044"),sQuery(id+"F0.wireOp",EDGE,"E1045"),sQuery(id+"F0.wireOp",EDGE,"E1046"),sQuery(id+"F0.wireOp",EDGE,"E1047"),sQuery(id+"F0.wireOp",EDGE,"E1048"),sQuery(id+"F0.wireOp",EDGE,"E1049"),sQuery(id+"F0.wireOp",EDGE,"E1050"),sQuery(id+"F0.wireOp",EDGE,"E1051"),sQuery(id+"F0.wireOp",EDGE,"E1052"),sQuery(id+"F0.wireOp",EDGE,"E1053"),sQuery(id+"F0.wireOp",EDGE,"E1054"),sQuery(id+"F0.wireOp",EDGE,"E1055"),sQuery(id+"F0.wireOp",EDGE,"E1056"),sQuery(id+"F0.wireOp",EDGE,"E1057"),sQuery(id+"F0.wireOp",EDGE,"E1058"),sQuery(id+"F0.wireOp",EDGE,"E1059"),sQuery(id+"F0.wireOp",EDGE,"E1060"),sQuery(id+"F0.wireOp",EDGE,"E1061"),sQuery(id+"F0.wireOp",EDGE,"E1062"),sQuery(id+"F0.wireOp",EDGE,"E1063"),sQuery(id+"F0.wireOp",EDGE,"E1064"),sQuery(id+"F0.wireOp",EDGE,"E1065"),sQuery(id+"F0.wireOp",EDGE,"E1066"),sQuery(id+"F0.wireOp",EDGE,"E1067"),sQuery(id+"F0.wireOp",EDGE,"E1068"),sQuery(id+"F0.wireOp",EDGE,"E1069"),sQuery(id+"F0.wireOp",EDGE,"E1070"),sQuery(id+"F0.wireOp",EDGE,"E1071"),sQuery(id+"F0.wireOp",EDGE,"E1072"),sQuery(id+"F0.wireOp",EDGE,"E1073"),sQuery(id+"F0.wireOp",EDGE,"E1074"),sQuery(id+"F0.wireOp",EDGE,"E1075"),sQuery(id+"F0.wireOp",EDGE,"E1076"),sQuery(id+"F0.wireOp",EDGE,"E1077"),sQuery(id+"F0.wireOp",EDGE,"E1078"),sQuery(id+"F0.wireOp",EDGE,"E1079"),sQuery(id+"F0.wireOp",EDGE,"E1080"),sQuery(id+"F0.wireOp",EDGE,"E1081"),sQuery(id+"F0.wireOp",EDGE,"E1082"),sQuery(id+"F0.wireOp",EDGE,"E1083"),sQuery(id+"F0.wireOp",EDGE,"E1084"),sQuery(id+"F0.wireOp",EDGE,"E1085"),sQuery(id+"F0.wireOp",EDGE,"E1086"),sQuery(id+"F0.wireOp",EDGE,"E1087"),sQuery(id+"F0.wireOp",EDGE,"E1088"),sQuery(id+"F0.wireOp",EDGE,"E1089"),sQuery(id+"F0.wireOp",EDGE,"E1090"),sQuery(id+"F0.wireOp",EDGE,"E1091"),sQuery(id+"F0.wireOp",EDGE,"E1092"),sQuery(id+"F0.wireOp",EDGE,"E1093"),sQuery(id+"F0.wireOp",EDGE,"E1094"),sQuery(id+"F0.wireOp",EDGE,"E1095"),sQuery(id+"F0.wireOp",EDGE,"E1096"),sQuery(id+"F0.wireOp",EDGE,"E1097"),sQuery(id+"F0.wireOp",EDGE,"E1098"),sQuery(id+"F0.wireOp",EDGE,"E1099"),sQuery(id+"F0.wireOp",EDGE,"E1100"),sQuery(id+"F0.wireOp",EDGE,"E1101"),sQuery(id+"F0.wireOp",EDGE,"E1102"),sQuery(id+"F0.wireOp",EDGE,"E1103"),sQuery(id+"F0.wireOp",EDGE,"E1104"),sQuery(id+"F0.wireOp",EDGE,"E1105"),sQuery(id+"F0.wireOp",EDGE,"E1106"),sQuery(id+"F0.wireOp",EDGE,"E1107"),sQuery(id+"F0.wireOp",EDGE,"E1108"),sQuery(id+"F0.wireOp",EDGE,"E1109"),sQuery(id+"F0.wireOp",EDGE,"E1110"),sQuery(id+"F0.wireOp",EDGE,"E1111"),sQuery(id+"F0.wireOp",EDGE,"E1112"),sQuery(id+"F0.wireOp",EDGE,"E1113"),sQuery(id+"F0.wireOp",EDGE,"E1114"),sQuery(id+"F0.wireOp",EDGE,"E1115"),sQuery(id+"F0.wireOp",EDGE,"E1116"),sQuery(id+"F0.wireOp",EDGE,"E1117"),sQuery(id+"F0.wireOp",EDGE,"E1118"),sQuery(id+"F0.wireOp",EDGE,"E1119"),sQuery(id+"F0.wireOp",EDGE,"E1120"),sQuery(id+"F0.wireOp",EDGE,"E1121"),sQuery(id+"F0.wireOp",EDGE,"E1122"),sQuery(id+"F0.wireOp",EDGE,"E1123"),sQuery(id+"F0.wireOp",EDGE,"E1124"),sQuery(id+"F0.wireOp",EDGE,"E1125"),sQuery(id+"F0.wireOp",EDGE,"E1126"),sQuery(id+"F0.wireOp",EDGE,"E1127"),sQuery(id+"F0.wireOp",EDGE,"E1128"),sQuery(id+"F0.wireOp",EDGE,"E1129"),sQuery(id+"F0.wireOp",EDGE,"E1130"),sQuery(id+"F0.wireOp",EDGE,"E1131"),sQuery(id+"F0.wireOp",EDGE,"E1132"),sQuery(id+"F0.wireOp",EDGE,"E1133"),sQuery(id+"F0.wireOp",EDGE,"E1134"),sQuery(id+"F0.wireOp",EDGE,"E1135"),sQuery(id+"F0.wireOp",EDGE,"E1136"),sQuery(id+"F0.wireOp",EDGE,"E1137"),sQuery(id+"F0.wireOp",EDGE,"E1138"),sQuery(id+"F0.wireOp",EDGE,"E1139"),sQuery(id+"F0.wireOp",EDGE,"E1140"),sQuery(id+"F0.wireOp",EDGE,"E1141"),sQuery(id+"F0.wireOp",EDGE,"E1142"),sQuery(id+"F0.wireOp",EDGE,"E1143"),sQuery(id+"F0.wireOp",EDGE,"E1144"),sQuery(id+"F0.wireOp",EDGE,"E1145"),sQuery(id+"F0.wireOp",EDGE,"E1146"),sQuery(id+"F0.wireOp",EDGE,"E1147"),sQuery(id+"F0.wireOp",EDGE,"E1148"),sQuery(id+"F0.wireOp",EDGE,"E1149"),sQuery(id+"F0.wireOp",EDGE,"E1150"),sQuery(id+"F0.wireOp",EDGE,"E1151"),sQuery(id+"F0.wireOp",EDGE,"E1152"),sQuery(id+"F0.wireOp",EDGE,"E1153"),sQuery(id+"F0.wireOp",EDGE,"E1154"),sQuery(id+"F0.wireOp",EDGE,"E1155"),sQuery(id+"F0.wireOp",EDGE,"E1156"),sQuery(id+"F0.wireOp",EDGE,"E1157"),sQuery(id+"F0.wireOp",EDGE,"E1158"),sQuery(id+"F0.wireOp",EDGE,"E1159"),sQuery(id+"F0.wireOp",EDGE,"E1160"),sQuery(id+"F0.wireOp",EDGE,"E1161"),sQuery(id+"F0.wireOp",EDGE,"E1162"),sQuery(id+"F0.wireOp",EDGE,"E1163"),sQuery(id+"F0.wireOp",EDGE,"E1164"),sQuery(id+"F0.wireOp",EDGE,"E1165"),sQuery(id+"F0.wireOp",EDGE,"E1166"),sQuery(id+"F0.wireOp",EDGE,"E1167")])],"isStart":false});
            var sketch = newSketch(context, id + "F2", { "sketchPlane" : qUnion([Q0])});
            skLineSegment(sketch, "E1168", {"start": v(-69.63, -26.73) * mm, "end": v(0, -63.48) * mm});
            skLineSegment(sketch, "E1169", {"start": v(82.59, 10.67) * mm, "end": v(0, -63.48) * mm});
            skLineSegment(sketch, "E1170", {"start": v(82.59, 10.67) * mm, "end": v(-55, 83.3) * mm});
            skLineSegment(sketch, "E1171", {"start": v(-69.63, -26.73) * mm, "end": v(-55, 83.3) * mm});
            skLineSegment(sketch, "E1172", {"start": v(0.68, 48.52) * mm, "end": v(22.46, 37.03) * mm, "construction": true});
            skLineSegment(sketch, "E1173", {"start": v(11.57, 42.77) * mm, "end": v(13.8, 46.99) * mm, "construction": true});
            skPoint(sketch, "E1173.endSnap0", {"position": v(11.57, 42.77) * mm});
            skSolve(sketch);
        }
        {
            var Q0;
            Q0=makeQuery(id+"F1.opExtrude","CAP_FACE",FACE,{"disambiguationData":[OSD([sQuery(id+"F0.wireOp",EDGE,"E0"),sQuery(id+"F0.wireOp",EDGE,"E1"),sQuery(id+"F0.wireOp",EDGE,"E2"),sQuery(id+"F0.wireOp",EDGE,"E3"),sQuery(id+"F0.wireOp",EDGE,"E4"),sQuery(id+"F0.wireOp",EDGE,"E5"),sQuery(id+"F0.wireOp",EDGE,"E6"),sQuery(id+"F0.wireOp",EDGE,"E7"),sQuery(id+"F0.wireOp",EDGE,"E8"),sQuery(id+"F0.wireOp",EDGE,"E9"),sQuery(id+"F0.wireOp",EDGE,"E10"),sQuery(id+"F0.wireOp",EDGE,"E11"),sQuery(id+"F0.wireOp",EDGE,"E12"),sQuery(id+"F0.wireOp",EDGE,"E13"),sQuery(id+"F0.wireOp",EDGE,"E14"),sQuery(id+"F0.wireOp",EDGE,"E15"),sQuery(id+"F0.wireOp",EDGE,"E16"),sQuery(id+"F0.wireOp",EDGE,"E17"),sQuery(id+"F0.wireOp",EDGE,"E18"),sQuery(id+"F0.wireOp",EDGE,"E19"),sQuery(id+"F0.wireOp",EDGE,"E20"),sQuery(id+"F0.wireOp",EDGE,"E21"),sQuery(id+"F0.wireOp",EDGE,"E22"),sQuery(id+"F0.wireOp",EDGE,"E23"),sQuery(id+"F0.wireOp",EDGE,"E24"),sQuery(id+"F0.wireOp",EDGE,"E25"),sQuery(id+"F0.wireOp",EDGE,"E26"),sQuery(id+"F0.wireOp",EDGE,"E27"),sQuery(id+"F0.wireOp",EDGE,"E28"),sQuery(id+"F0.wireOp",EDGE,"E29"),sQuery(id+"F0.wireOp",EDGE,"E30"),sQuery(id+"F0.wireOp",EDGE,"E31"),sQuery(id+"F0.wireOp",EDGE,"E32"),sQuery(id+"F0.wireOp",EDGE,"E33"),sQuery(id+"F0.wireOp",EDGE,"E34"),sQuery(id+"F0.wireOp",EDGE,"E35"),sQuery(id+"F0.wireOp",EDGE,"E36"),sQuery(id+"F0.wireOp",EDGE,"E37"),sQuery(id+"F0.wireOp",EDGE,"E38"),sQuery(id+"F0.wireOp",EDGE,"E39"),sQuery(id+"F0.wireOp",EDGE,"E40"),sQuery(id+"F0.wireOp",EDGE,"E41"),sQuery(id+"F0.wireOp",EDGE,"E42"),sQuery(id+"F0.wireOp",EDGE,"E43"),sQuery(id+"F0.wireOp",EDGE,"E44"),sQuery(id+"F0.wireOp",EDGE,"E45"),sQuery(id+"F0.wireOp",EDGE,"E46"),sQuery(id+"F0.wireOp",EDGE,"E47"),sQuery(id+"F0.wireOp",EDGE,"E48"),sQuery(id+"F0.wireOp",EDGE,"E49"),sQuery(id+"F0.wireOp",EDGE,"E50"),sQuery(id+"F0.wireOp",EDGE,"E51"),sQuery(id+"F0.wireOp",EDGE,"E52"),sQuery(id+"F0.wireOp",EDGE,"E53"),sQuery(id+"F0.wireOp",EDGE,"E54"),sQuery(id+"F0.wireOp",EDGE,"E55"),sQuery(id+"F0.wireOp",EDGE,"E56"),sQuery(id+"F0.wireOp",EDGE,"E57"),sQuery(id+"F0.wireOp",EDGE,"E58"),sQuery(id+"F0.wireOp",EDGE,"E59"),sQuery(id+"F0.wireOp",EDGE,"E60"),sQuery(id+"F0.wireOp",EDGE,"E61"),sQuery(id+"F0.wireOp",EDGE,"E62"),sQuery(id+"F0.wireOp",EDGE,"E63"),sQuery(id+"F0.wireOp",EDGE,"E64"),sQuery(id+"F0.wireOp",EDGE,"E65"),sQuery(id+"F0.wireOp",EDGE,"E66"),sQuery(id+"F0.wireOp",EDGE,"E67"),sQuery(id+"F0.wireOp",EDGE,"E68"),sQuery(id+"F0.wireOp",EDGE,"E69"),sQuery(id+"F0.wireOp",EDGE,"E70"),sQuery(id+"F0.wireOp",EDGE,"E71"),sQuery(id+"F0.wireOp",EDGE,"E72"),sQuery(id+"F0.wireOp",EDGE,"E73"),sQuery(id+"F0.wireOp",EDGE,"E74"),sQuery(id+"F0.wireOp",EDGE,"E75"),sQuery(id+"F0.wireOp",EDGE,"E76"),sQuery(id+"F0.wireOp",EDGE,"E77"),sQuery(id+"F0.wireOp",EDGE,"E78"),sQuery(id+"F0.wireOp",EDGE,"E79"),sQuery(id+"F0.wireOp",EDGE,"E80"),sQuery(id+"F0.wireOp",EDGE,"E81"),sQuery(id+"F0.wireOp",EDGE,"E82"),sQuery(id+"F0.wireOp",EDGE,"E83"),sQuery(id+"F0.wireOp",EDGE,"E84"),sQuery(id+"F0.wireOp",EDGE,"E85"),sQuery(id+"F0.wireOp",EDGE,"E86"),sQuery(id+"F0.wireOp",EDGE,"E87"),sQuery(id+"F0.wireOp",EDGE,"E88"),sQuery(id+"F0.wireOp",EDGE,"E89"),sQuery(id+"F0.wireOp",EDGE,"E90"),sQuery(id+"F0.wireOp",EDGE,"E91"),sQuery(id+"F0.wireOp",EDGE,"E92"),sQuery(id+"F0.wireOp",EDGE,"E93"),sQuery(id+"F0.wireOp",EDGE,"E94"),sQuery(id+"F0.wireOp",EDGE,"E95"),sQuery(id+"F0.wireOp",EDGE,"E96"),sQuery(id+"F0.wireOp",EDGE,"E97"),sQuery(id+"F0.wireOp",EDGE,"E98"),sQuery(id+"F0.wireOp",EDGE,"E99"),sQuery(id+"F0.wireOp",EDGE,"E100"),sQuery(id+"F0.wireOp",EDGE,"E101"),sQuery(id+"F0.wireOp",EDGE,"E102"),sQuery(id+"F0.wireOp",EDGE,"E103"),sQuery(id+"F0.wireOp",EDGE,"E104"),sQuery(id+"F0.wireOp",EDGE,"E105"),sQuery(id+"F0.wireOp",EDGE,"E106"),sQuery(id+"F0.wireOp",EDGE,"E107"),sQuery(id+"F0.wireOp",EDGE,"E108"),sQuery(id+"F0.wireOp",EDGE,"E109"),sQuery(id+"F0.wireOp",EDGE,"E110"),sQuery(id+"F0.wireOp",EDGE,"E111"),sQuery(id+"F0.wireOp",EDGE,"E112"),sQuery(id+"F0.wireOp",EDGE,"E113"),sQuery(id+"F0.wireOp",EDGE,"E114"),sQuery(id+"F0.wireOp",EDGE,"E115"),sQuery(id+"F0.wireOp",EDGE,"E116"),sQuery(id+"F0.wireOp",EDGE,"E117"),sQuery(id+"F0.wireOp",EDGE,"E118"),sQuery(id+"F0.wireOp",EDGE,"E119"),sQuery(id+"F0.wireOp",EDGE,"E120"),sQuery(id+"F0.wireOp",EDGE,"E121"),sQuery(id+"F0.wireOp",EDGE,"E122"),sQuery(id+"F0.wireOp",EDGE,"E123"),sQuery(id+"F0.wireOp",EDGE,"E124"),sQuery(id+"F0.wireOp",EDGE,"E125"),sQuery(id+"F0.wireOp",EDGE,"E126"),sQuery(id+"F0.wireOp",EDGE,"E127"),sQuery(id+"F0.wireOp",EDGE,"E128"),sQuery(id+"F0.wireOp",EDGE,"E129"),sQuery(id+"F0.wireOp",EDGE,"E130"),sQuery(id+"F0.wireOp",EDGE,"E131"),sQuery(id+"F0.wireOp",EDGE,"E132"),sQuery(id+"F0.wireOp",EDGE,"E133"),sQuery(id+"F0.wireOp",EDGE,"E134"),sQuery(id+"F0.wireOp",EDGE,"E135"),sQuery(id+"F0.wireOp",EDGE,"E136"),sQuery(id+"F0.wireOp",EDGE,"E137"),sQuery(id+"F0.wireOp",EDGE,"E138"),sQuery(id+"F0.wireOp",EDGE,"E139"),sQuery(id+"F0.wireOp",EDGE,"E140"),sQuery(id+"F0.wireOp",EDGE,"E141"),sQuery(id+"F0.wireOp",EDGE,"E142"),sQuery(id+"F0.wireOp",EDGE,"E143"),sQuery(id+"F0.wireOp",EDGE,"E144"),sQuery(id+"F0.wireOp",EDGE,"E145"),sQuery(id+"F0.wireOp",EDGE,"E146"),sQuery(id+"F0.wireOp",EDGE,"E147"),sQuery(id+"F0.wireOp",EDGE,"E148"),sQuery(id+"F0.wireOp",EDGE,"E149"),sQuery(id+"F0.wireOp",EDGE,"E150"),sQuery(id+"F0.wireOp",EDGE,"E151"),sQuery(id+"F0.wireOp",EDGE,"E152"),sQuery(id+"F0.wireOp",EDGE,"E153"),sQuery(id+"F0.wireOp",EDGE,"E154"),sQuery(id+"F0.wireOp",EDGE,"E155"),sQuery(id+"F0.wireOp",EDGE,"E156"),sQuery(id+"F0.wireOp",EDGE,"E157"),sQuery(id+"F0.wireOp",EDGE,"E158"),sQuery(id+"F0.wireOp",EDGE,"E159"),sQuery(id+"F0.wireOp",EDGE,"E160"),sQuery(id+"F0.wireOp",EDGE,"E161"),sQuery(id+"F0.wireOp",EDGE,"E162"),sQuery(id+"F0.wireOp",EDGE,"E163"),sQuery(id+"F0.wireOp",EDGE,"E164"),sQuery(id+"F0.wireOp",EDGE,"E165"),sQuery(id+"F0.wireOp",EDGE,"E166"),sQuery(id+"F0.wireOp",EDGE,"E167"),sQuery(id+"F0.wireOp",EDGE,"E168"),sQuery(id+"F0.wireOp",EDGE,"E169"),sQuery(id+"F0.wireOp",EDGE,"E170"),sQuery(id+"F0.wireOp",EDGE,"E171"),sQuery(id+"F0.wireOp",EDGE,"E172"),sQuery(id+"F0.wireOp",EDGE,"E173"),sQuery(id+"F0.wireOp",EDGE,"E174"),sQuery(id+"F0.wireOp",EDGE,"E175"),sQuery(id+"F0.wireOp",EDGE,"E176"),sQuery(id+"F0.wireOp",EDGE,"E177"),sQuery(id+"F0.wireOp",EDGE,"E178"),sQuery(id+"F0.wireOp",EDGE,"E179"),sQuery(id+"F0.wireOp",EDGE,"E180"),sQuery(id+"F0.wireOp",EDGE,"E181"),sQuery(id+"F0.wireOp",EDGE,"E182"),sQuery(id+"F0.wireOp",EDGE,"E183"),sQuery(id+"F0.wireOp",EDGE,"E184"),sQuery(id+"F0.wireOp",EDGE,"E185"),sQuery(id+"F0.wireOp",EDGE,"E186"),sQuery(id+"F0.wireOp",EDGE,"E187"),sQuery(id+"F0.wireOp",EDGE,"E188"),sQuery(id+"F0.wireOp",EDGE,"E189"),sQuery(id+"F0.wireOp",EDGE,"E190"),sQuery(id+"F0.wireOp",EDGE,"E191"),sQuery(id+"F0.wireOp",EDGE,"E192"),sQuery(id+"F0.wireOp",EDGE,"E193"),sQuery(id+"F0.wireOp",EDGE,"E194"),sQuery(id+"F0.wireOp",EDGE,"E195"),sQuery(id+"F0.wireOp",EDGE,"E196"),sQuery(id+"F0.wireOp",EDGE,"E197"),sQuery(id+"F0.wireOp",EDGE,"E198"),sQuery(id+"F0.wireOp",EDGE,"E199"),sQuery(id+"F0.wireOp",EDGE,"E200"),sQuery(id+"F0.wireOp",EDGE,"E201"),sQuery(id+"F0.wireOp",EDGE,"E202"),sQuery(id+"F0.wireOp",EDGE,"E203"),sQuery(id+"F0.wireOp",EDGE,"E204"),sQuery(id+"F0.wireOp",EDGE,"E205"),sQuery(id+"F0.wireOp",EDGE,"E206"),sQuery(id+"F0.wireOp",EDGE,"E207"),sQuery(id+"F0.wireOp",EDGE,"E208"),sQuery(id+"F0.wireOp",EDGE,"E209"),sQuery(id+"F0.wireOp",EDGE,"E210"),sQuery(id+"F0.wireOp",EDGE,"E211"),sQuery(id+"F0.wireOp",EDGE,"E212"),sQuery(id+"F0.wireOp",EDGE,"E213"),sQuery(id+"F0.wireOp",EDGE,"E214"),sQuery(id+"F0.wireOp",EDGE,"E215"),sQuery(id+"F0.wireOp",EDGE,"E216"),sQuery(id+"F0.wireOp",EDGE,"E217"),sQuery(id+"F0.wireOp",EDGE,"E218"),sQuery(id+"F0.wireOp",EDGE,"E219"),sQuery(id+"F0.wireOp",EDGE,"E220"),sQuery(id+"F0.wireOp",EDGE,"E221"),sQuery(id+"F0.wireOp",EDGE,"E222"),sQuery(id+"F0.wireOp",EDGE,"E223"),sQuery(id+"F0.wireOp",EDGE,"E224"),sQuery(id+"F0.wireOp",EDGE,"E225"),sQuery(id+"F0.wireOp",EDGE,"E226"),sQuery(id+"F0.wireOp",EDGE,"E227"),sQuery(id+"F0.wireOp",EDGE,"E228"),sQuery(id+"F0.wireOp",EDGE,"E229"),sQuery(id+"F0.wireOp",EDGE,"E230"),sQuery(id+"F0.wireOp",EDGE,"E231"),sQuery(id+"F0.wireOp",EDGE,"E232"),sQuery(id+"F0.wireOp",EDGE,"E233"),sQuery(id+"F0.wireOp",EDGE,"E234"),sQuery(id+"F0.wireOp",EDGE,"E235"),sQuery(id+"F0.wireOp",EDGE,"E236"),sQuery(id+"F0.wireOp",EDGE,"E237"),sQuery(id+"F0.wireOp",EDGE,"E238"),sQuery(id+"F0.wireOp",EDGE,"E239"),sQuery(id+"F0.wireOp",EDGE,"E240"),sQuery(id+"F0.wireOp",EDGE,"E241"),sQuery(id+"F0.wireOp",EDGE,"E242"),sQuery(id+"F0.wireOp",EDGE,"E243"),sQuery(id+"F0.wireOp",EDGE,"E244"),sQuery(id+"F0.wireOp",EDGE,"E245"),sQuery(id+"F0.wireOp",EDGE,"E246"),sQuery(id+"F0.wireOp",EDGE,"E247"),sQuery(id+"F0.wireOp",EDGE,"E248"),sQuery(id+"F0.wireOp",EDGE,"E249"),sQuery(id+"F0.wireOp",EDGE,"E250"),sQuery(id+"F0.wireOp",EDGE,"E251"),sQuery(id+"F0.wireOp",EDGE,"E252"),sQuery(id+"F0.wireOp",EDGE,"E253"),sQuery(id+"F0.wireOp",EDGE,"E254"),sQuery(id+"F0.wireOp",EDGE,"E255"),sQuery(id+"F0.wireOp",EDGE,"E256"),sQuery(id+"F0.wireOp",EDGE,"E257"),sQuery(id+"F0.wireOp",EDGE,"E258"),sQuery(id+"F0.wireOp",EDGE,"E259"),sQuery(id+"F0.wireOp",EDGE,"E260"),sQuery(id+"F0.wireOp",EDGE,"E261"),sQuery(id+"F0.wireOp",EDGE,"E262"),sQuery(id+"F0.wireOp",EDGE,"E263"),sQuery(id+"F0.wireOp",EDGE,"E264"),sQuery(id+"F0.wireOp",EDGE,"E265"),sQuery(id+"F0.wireOp",EDGE,"E266"),sQuery(id+"F0.wireOp",EDGE,"E267"),sQuery(id+"F0.wireOp",EDGE,"E268"),sQuery(id+"F0.wireOp",EDGE,"E269"),sQuery(id+"F0.wireOp",EDGE,"E270"),sQuery(id+"F0.wireOp",EDGE,"E271"),sQuery(id+"F0.wireOp",EDGE,"E272"),sQuery(id+"F0.wireOp",EDGE,"E273"),sQuery(id+"F0.wireOp",EDGE,"E274"),sQuery(id+"F0.wireOp",EDGE,"E275"),sQuery(id+"F0.wireOp",EDGE,"E276"),sQuery(id+"F0.wireOp",EDGE,"E277"),sQuery(id+"F0.wireOp",EDGE,"E278"),sQuery(id+"F0.wireOp",EDGE,"E279"),sQuery(id+"F0.wireOp",EDGE,"E280"),sQuery(id+"F0.wireOp",EDGE,"E281"),sQuery(id+"F0.wireOp",EDGE,"E282"),sQuery(id+"F0.wireOp",EDGE,"E283"),sQuery(id+"F0.wireOp",EDGE,"E284"),sQuery(id+"F0.wireOp",EDGE,"E285"),sQuery(id+"F0.wireOp",EDGE,"E286"),sQuery(id+"F0.wireOp",EDGE,"E287"),sQuery(id+"F0.wireOp",EDGE,"E288"),sQuery(id+"F0.wireOp",EDGE,"E289"),sQuery(id+"F0.wireOp",EDGE,"E290"),sQuery(id+"F0.wireOp",EDGE,"E291"),sQuery(id+"F0.wireOp",EDGE,"E292"),sQuery(id+"F0.wireOp",EDGE,"E293"),sQuery(id+"F0.wireOp",EDGE,"E294"),sQuery(id+"F0.wireOp",EDGE,"E295"),sQuery(id+"F0.wireOp",EDGE,"E296"),sQuery(id+"F0.wireOp",EDGE,"E297"),sQuery(id+"F0.wireOp",EDGE,"E298"),sQuery(id+"F0.wireOp",EDGE,"E299"),sQuery(id+"F0.wireOp",EDGE,"E300"),sQuery(id+"F0.wireOp",EDGE,"E301"),sQuery(id+"F0.wireOp",EDGE,"E302"),sQuery(id+"F0.wireOp",EDGE,"E303"),sQuery(id+"F0.wireOp",EDGE,"E304"),sQuery(id+"F0.wireOp",EDGE,"E305"),sQuery(id+"F0.wireOp",EDGE,"E306"),sQuery(id+"F0.wireOp",EDGE,"E307"),sQuery(id+"F0.wireOp",EDGE,"E308"),sQuery(id+"F0.wireOp",EDGE,"E309"),sQuery(id+"F0.wireOp",EDGE,"E310"),sQuery(id+"F0.wireOp",EDGE,"E311"),sQuery(id+"F0.wireOp",EDGE,"E312"),sQuery(id+"F0.wireOp",EDGE,"E313"),sQuery(id+"F0.wireOp",EDGE,"E314"),sQuery(id+"F0.wireOp",EDGE,"E315"),sQuery(id+"F0.wireOp",EDGE,"E316"),sQuery(id+"F0.wireOp",EDGE,"E317"),sQuery(id+"F0.wireOp",EDGE,"E318"),sQuery(id+"F0.wireOp",EDGE,"E319"),sQuery(id+"F0.wireOp",EDGE,"E320"),sQuery(id+"F0.wireOp",EDGE,"E321"),sQuery(id+"F0.wireOp",EDGE,"E322"),sQuery(id+"F0.wireOp",EDGE,"E323"),sQuery(id+"F0.wireOp",EDGE,"E324"),sQuery(id+"F0.wireOp",EDGE,"E325"),sQuery(id+"F0.wireOp",EDGE,"E326"),sQuery(id+"F0.wireOp",EDGE,"E327"),sQuery(id+"F0.wireOp",EDGE,"E328"),sQuery(id+"F0.wireOp",EDGE,"E329"),sQuery(id+"F0.wireOp",EDGE,"E330"),sQuery(id+"F0.wireOp",EDGE,"E331"),sQuery(id+"F0.wireOp",EDGE,"E332"),sQuery(id+"F0.wireOp",EDGE,"E333"),sQuery(id+"F0.wireOp",EDGE,"E334"),sQuery(id+"F0.wireOp",EDGE,"E335"),sQuery(id+"F0.wireOp",EDGE,"E336"),sQuery(id+"F0.wireOp",EDGE,"E337"),sQuery(id+"F0.wireOp",EDGE,"E338"),sQuery(id+"F0.wireOp",EDGE,"E339"),sQuery(id+"F0.wireOp",EDGE,"E340"),sQuery(id+"F0.wireOp",EDGE,"E341"),sQuery(id+"F0.wireOp",EDGE,"E342"),sQuery(id+"F0.wireOp",EDGE,"E343"),sQuery(id+"F0.wireOp",EDGE,"E344"),sQuery(id+"F0.wireOp",EDGE,"E345"),sQuery(id+"F0.wireOp",EDGE,"E346"),sQuery(id+"F0.wireOp",EDGE,"E347"),sQuery(id+"F0.wireOp",EDGE,"E348"),sQuery(id+"F0.wireOp",EDGE,"E349"),sQuery(id+"F0.wireOp",EDGE,"E350"),sQuery(id+"F0.wireOp",EDGE,"E351"),sQuery(id+"F0.wireOp",EDGE,"E352"),sQuery(id+"F0.wireOp",EDGE,"E353"),sQuery(id+"F0.wireOp",EDGE,"E354"),sQuery(id+"F0.wireOp",EDGE,"E355"),sQuery(id+"F0.wireOp",EDGE,"E356"),sQuery(id+"F0.wireOp",EDGE,"E357"),sQuery(id+"F0.wireOp",EDGE,"E358"),sQuery(id+"F0.wireOp",EDGE,"E359"),sQuery(id+"F0.wireOp",EDGE,"E360"),sQuery(id+"F0.wireOp",EDGE,"E361"),sQuery(id+"F0.wireOp",EDGE,"E362"),sQuery(id+"F0.wireOp",EDGE,"E363"),sQuery(id+"F0.wireOp",EDGE,"E364"),sQuery(id+"F0.wireOp",EDGE,"E365"),sQuery(id+"F0.wireOp",EDGE,"E366"),sQuery(id+"F0.wireOp",EDGE,"E367"),sQuery(id+"F0.wireOp",EDGE,"E368"),sQuery(id+"F0.wireOp",EDGE,"E369"),sQuery(id+"F0.wireOp",EDGE,"E370"),sQuery(id+"F0.wireOp",EDGE,"E371"),sQuery(id+"F0.wireOp",EDGE,"E372"),sQuery(id+"F0.wireOp",EDGE,"E373"),sQuery(id+"F0.wireOp",EDGE,"E374"),sQuery(id+"F0.wireOp",EDGE,"E375"),sQuery(id+"F0.wireOp",EDGE,"E376"),sQuery(id+"F0.wireOp",EDGE,"E377"),sQuery(id+"F0.wireOp",EDGE,"E378"),sQuery(id+"F0.wireOp",EDGE,"E379"),sQuery(id+"F0.wireOp",EDGE,"E380"),sQuery(id+"F0.wireOp",EDGE,"E381"),sQuery(id+"F0.wireOp",EDGE,"E382"),sQuery(id+"F0.wireOp",EDGE,"E383"),sQuery(id+"F0.wireOp",EDGE,"E384"),sQuery(id+"F0.wireOp",EDGE,"E385"),sQuery(id+"F0.wireOp",EDGE,"E386"),sQuery(id+"F0.wireOp",EDGE,"E387"),sQuery(id+"F0.wireOp",EDGE,"E388"),sQuery(id+"F0.wireOp",EDGE,"E389"),sQuery(id+"F0.wireOp",EDGE,"E390"),sQuery(id+"F0.wireOp",EDGE,"E391"),sQuery(id+"F0.wireOp",EDGE,"E392"),sQuery(id+"F0.wireOp",EDGE,"E393"),sQuery(id+"F0.wireOp",EDGE,"E394"),sQuery(id+"F0.wireOp",EDGE,"E395"),sQuery(id+"F0.wireOp",EDGE,"E396"),sQuery(id+"F0.wireOp",EDGE,"E397"),sQuery(id+"F0.wireOp",EDGE,"E398"),sQuery(id+"F0.wireOp",EDGE,"E399"),sQuery(id+"F0.wireOp",EDGE,"E400"),sQuery(id+"F0.wireOp",EDGE,"E401"),sQuery(id+"F0.wireOp",EDGE,"E402"),sQuery(id+"F0.wireOp",EDGE,"E403"),sQuery(id+"F0.wireOp",EDGE,"E404"),sQuery(id+"F0.wireOp",EDGE,"E405"),sQuery(id+"F0.wireOp",EDGE,"E406"),sQuery(id+"F0.wireOp",EDGE,"E407"),sQuery(id+"F0.wireOp",EDGE,"E408"),sQuery(id+"F0.wireOp",EDGE,"E409"),sQuery(id+"F0.wireOp",EDGE,"E410"),sQuery(id+"F0.wireOp",EDGE,"E411"),sQuery(id+"F0.wireOp",EDGE,"E412"),sQuery(id+"F0.wireOp",EDGE,"E413"),sQuery(id+"F0.wireOp",EDGE,"E414"),sQuery(id+"F0.wireOp",EDGE,"E415"),sQuery(id+"F0.wireOp",EDGE,"E416"),sQuery(id+"F0.wireOp",EDGE,"E417"),sQuery(id+"F0.wireOp",EDGE,"E418"),sQuery(id+"F0.wireOp",EDGE,"E419"),sQuery(id+"F0.wireOp",EDGE,"E420"),sQuery(id+"F0.wireOp",EDGE,"E421"),sQuery(id+"F0.wireOp",EDGE,"E422"),sQuery(id+"F0.wireOp",EDGE,"E423"),sQuery(id+"F0.wireOp",EDGE,"E424"),sQuery(id+"F0.wireOp",EDGE,"E425"),sQuery(id+"F0.wireOp",EDGE,"E426"),sQuery(id+"F0.wireOp",EDGE,"E427"),sQuery(id+"F0.wireOp",EDGE,"E428"),sQuery(id+"F0.wireOp",EDGE,"E429"),sQuery(id+"F0.wireOp",EDGE,"E430"),sQuery(id+"F0.wireOp",EDGE,"E431"),sQuery(id+"F0.wireOp",EDGE,"E432"),sQuery(id+"F0.wireOp",EDGE,"E433"),sQuery(id+"F0.wireOp",EDGE,"E434"),sQuery(id+"F0.wireOp",EDGE,"E435"),sQuery(id+"F0.wireOp",EDGE,"E436"),sQuery(id+"F0.wireOp",EDGE,"E437"),sQuery(id+"F0.wireOp",EDGE,"E438"),sQuery(id+"F0.wireOp",EDGE,"E439"),sQuery(id+"F0.wireOp",EDGE,"E440"),sQuery(id+"F0.wireOp",EDGE,"E441"),sQuery(id+"F0.wireOp",EDGE,"E442"),sQuery(id+"F0.wireOp",EDGE,"E443"),sQuery(id+"F0.wireOp",EDGE,"E444"),sQuery(id+"F0.wireOp",EDGE,"E445"),sQuery(id+"F0.wireOp",EDGE,"E446"),sQuery(id+"F0.wireOp",EDGE,"E447"),sQuery(id+"F0.wireOp",EDGE,"E448"),sQuery(id+"F0.wireOp",EDGE,"E449"),sQuery(id+"F0.wireOp",EDGE,"E450"),sQuery(id+"F0.wireOp",EDGE,"E451"),sQuery(id+"F0.wireOp",EDGE,"E452"),sQuery(id+"F0.wireOp",EDGE,"E453"),sQuery(id+"F0.wireOp",EDGE,"E454"),sQuery(id+"F0.wireOp",EDGE,"E455"),sQuery(id+"F0.wireOp",EDGE,"E456"),sQuery(id+"F0.wireOp",EDGE,"E457"),sQuery(id+"F0.wireOp",EDGE,"E458"),sQuery(id+"F0.wireOp",EDGE,"E459"),sQuery(id+"F0.wireOp",EDGE,"E460"),sQuery(id+"F0.wireOp",EDGE,"E461"),sQuery(id+"F0.wireOp",EDGE,"E462"),sQuery(id+"F0.wireOp",EDGE,"E463"),sQuery(id+"F0.wireOp",EDGE,"E464"),sQuery(id+"F0.wireOp",EDGE,"E465"),sQuery(id+"F0.wireOp",EDGE,"E466"),sQuery(id+"F0.wireOp",EDGE,"E467"),sQuery(id+"F0.wireOp",EDGE,"E468"),sQuery(id+"F0.wireOp",EDGE,"E469"),sQuery(id+"F0.wireOp",EDGE,"E470"),sQuery(id+"F0.wireOp",EDGE,"E471"),sQuery(id+"F0.wireOp",EDGE,"E472"),sQuery(id+"F0.wireOp",EDGE,"E473"),sQuery(id+"F0.wireOp",EDGE,"E474"),sQuery(id+"F0.wireOp",EDGE,"E475"),sQuery(id+"F0.wireOp",EDGE,"E476"),sQuery(id+"F0.wireOp",EDGE,"E477"),sQuery(id+"F0.wireOp",EDGE,"E478"),sQuery(id+"F0.wireOp",EDGE,"E479"),sQuery(id+"F0.wireOp",EDGE,"E480"),sQuery(id+"F0.wireOp",EDGE,"E481"),sQuery(id+"F0.wireOp",EDGE,"E482"),sQuery(id+"F0.wireOp",EDGE,"E483"),sQuery(id+"F0.wireOp",EDGE,"E484"),sQuery(id+"F0.wireOp",EDGE,"E485"),sQuery(id+"F0.wireOp",EDGE,"E486"),sQuery(id+"F0.wireOp",EDGE,"E487"),sQuery(id+"F0.wireOp",EDGE,"E488"),sQuery(id+"F0.wireOp",EDGE,"E489"),sQuery(id+"F0.wireOp",EDGE,"E490"),sQuery(id+"F0.wireOp",EDGE,"E491"),sQuery(id+"F0.wireOp",EDGE,"E492"),sQuery(id+"F0.wireOp",EDGE,"E493"),sQuery(id+"F0.wireOp",EDGE,"E494"),sQuery(id+"F0.wireOp",EDGE,"E495"),sQuery(id+"F0.wireOp",EDGE,"E496"),sQuery(id+"F0.wireOp",EDGE,"E497"),sQuery(id+"F0.wireOp",EDGE,"E498"),sQuery(id+"F0.wireOp",EDGE,"E499"),sQuery(id+"F0.wireOp",EDGE,"E500"),sQuery(id+"F0.wireOp",EDGE,"E501"),sQuery(id+"F0.wireOp",EDGE,"E502"),sQuery(id+"F0.wireOp",EDGE,"E503"),sQuery(id+"F0.wireOp",EDGE,"E504"),sQuery(id+"F0.wireOp",EDGE,"E505"),sQuery(id+"F0.wireOp",EDGE,"E506"),sQuery(id+"F0.wireOp",EDGE,"E507"),sQuery(id+"F0.wireOp",EDGE,"E508"),sQuery(id+"F0.wireOp",EDGE,"E509"),sQuery(id+"F0.wireOp",EDGE,"E510"),sQuery(id+"F0.wireOp",EDGE,"E511"),sQuery(id+"F0.wireOp",EDGE,"E512"),sQuery(id+"F0.wireOp",EDGE,"E513"),sQuery(id+"F0.wireOp",EDGE,"E514"),sQuery(id+"F0.wireOp",EDGE,"E515"),sQuery(id+"F0.wireOp",EDGE,"E516"),sQuery(id+"F0.wireOp",EDGE,"E517"),sQuery(id+"F0.wireOp",EDGE,"E518"),sQuery(id+"F0.wireOp",EDGE,"E519"),sQuery(id+"F0.wireOp",EDGE,"E520"),sQuery(id+"F0.wireOp",EDGE,"E521"),sQuery(id+"F0.wireOp",EDGE,"E522"),sQuery(id+"F0.wireOp",EDGE,"E523"),sQuery(id+"F0.wireOp",EDGE,"E524"),sQuery(id+"F0.wireOp",EDGE,"E525"),sQuery(id+"F0.wireOp",EDGE,"E526"),sQuery(id+"F0.wireOp",EDGE,"E527"),sQuery(id+"F0.wireOp",EDGE,"E528"),sQuery(id+"F0.wireOp",EDGE,"E529"),sQuery(id+"F0.wireOp",EDGE,"E530"),sQuery(id+"F0.wireOp",EDGE,"E531"),sQuery(id+"F0.wireOp",EDGE,"E532"),sQuery(id+"F0.wireOp",EDGE,"E533"),sQuery(id+"F0.wireOp",EDGE,"E534"),sQuery(id+"F0.wireOp",EDGE,"E535"),sQuery(id+"F0.wireOp",EDGE,"E536"),sQuery(id+"F0.wireOp",EDGE,"E537"),sQuery(id+"F0.wireOp",EDGE,"E538"),sQuery(id+"F0.wireOp",EDGE,"E539"),sQuery(id+"F0.wireOp",EDGE,"E540"),sQuery(id+"F0.wireOp",EDGE,"E541"),sQuery(id+"F0.wireOp",EDGE,"E542"),sQuery(id+"F0.wireOp",EDGE,"E543"),sQuery(id+"F0.wireOp",EDGE,"E544"),sQuery(id+"F0.wireOp",EDGE,"E545"),sQuery(id+"F0.wireOp",EDGE,"E546"),sQuery(id+"F0.wireOp",EDGE,"E547"),sQuery(id+"F0.wireOp",EDGE,"E548"),sQuery(id+"F0.wireOp",EDGE,"E549"),sQuery(id+"F0.wireOp",EDGE,"E550"),sQuery(id+"F0.wireOp",EDGE,"E551"),sQuery(id+"F0.wireOp",EDGE,"E552"),sQuery(id+"F0.wireOp",EDGE,"E553"),sQuery(id+"F0.wireOp",EDGE,"E554"),sQuery(id+"F0.wireOp",EDGE,"E555"),sQuery(id+"F0.wireOp",EDGE,"E556"),sQuery(id+"F0.wireOp",EDGE,"E557"),sQuery(id+"F0.wireOp",EDGE,"E558"),sQuery(id+"F0.wireOp",EDGE,"E559"),sQuery(id+"F0.wireOp",EDGE,"E560"),sQuery(id+"F0.wireOp",EDGE,"E561"),sQuery(id+"F0.wireOp",EDGE,"E562"),sQuery(id+"F0.wireOp",EDGE,"E563"),sQuery(id+"F0.wireOp",EDGE,"E564"),sQuery(id+"F0.wireOp",EDGE,"E565"),sQuery(id+"F0.wireOp",EDGE,"E566"),sQuery(id+"F0.wireOp",EDGE,"E567"),sQuery(id+"F0.wireOp",EDGE,"E568"),sQuery(id+"F0.wireOp",EDGE,"E569"),sQuery(id+"F0.wireOp",EDGE,"E570"),sQuery(id+"F0.wireOp",EDGE,"E571"),sQuery(id+"F0.wireOp",EDGE,"E572"),sQuery(id+"F0.wireOp",EDGE,"E573"),sQuery(id+"F0.wireOp",EDGE,"E574"),sQuery(id+"F0.wireOp",EDGE,"E575"),sQuery(id+"F0.wireOp",EDGE,"E576"),sQuery(id+"F0.wireOp",EDGE,"E577"),sQuery(id+"F0.wireOp",EDGE,"E578"),sQuery(id+"F0.wireOp",EDGE,"E579"),sQuery(id+"F0.wireOp",EDGE,"E580"),sQuery(id+"F0.wireOp",EDGE,"E581"),sQuery(id+"F0.wireOp",EDGE,"E582"),sQuery(id+"F0.wireOp",EDGE,"E583"),sQuery(id+"F0.wireOp",EDGE,"E584"),sQuery(id+"F0.wireOp",EDGE,"E585"),sQuery(id+"F0.wireOp",EDGE,"E586"),sQuery(id+"F0.wireOp",EDGE,"E587"),sQuery(id+"F0.wireOp",EDGE,"E588"),sQuery(id+"F0.wireOp",EDGE,"E589"),sQuery(id+"F0.wireOp",EDGE,"E590"),sQuery(id+"F0.wireOp",EDGE,"E591"),sQuery(id+"F0.wireOp",EDGE,"E592"),sQuery(id+"F0.wireOp",EDGE,"E593"),sQuery(id+"F0.wireOp",EDGE,"E594"),sQuery(id+"F0.wireOp",EDGE,"E595"),sQuery(id+"F0.wireOp",EDGE,"E596"),sQuery(id+"F0.wireOp",EDGE,"E597"),sQuery(id+"F0.wireOp",EDGE,"E598"),sQuery(id+"F0.wireOp",EDGE,"E599"),sQuery(id+"F0.wireOp",EDGE,"E600"),sQuery(id+"F0.wireOp",EDGE,"E601"),sQuery(id+"F0.wireOp",EDGE,"E602"),sQuery(id+"F0.wireOp",EDGE,"E603"),sQuery(id+"F0.wireOp",EDGE,"E604"),sQuery(id+"F0.wireOp",EDGE,"E605"),sQuery(id+"F0.wireOp",EDGE,"E606"),sQuery(id+"F0.wireOp",EDGE,"E607"),sQuery(id+"F0.wireOp",EDGE,"E608"),sQuery(id+"F0.wireOp",EDGE,"E609"),sQuery(id+"F0.wireOp",EDGE,"E610"),sQuery(id+"F0.wireOp",EDGE,"E611"),sQuery(id+"F0.wireOp",EDGE,"E612"),sQuery(id+"F0.wireOp",EDGE,"E613"),sQuery(id+"F0.wireOp",EDGE,"E614"),sQuery(id+"F0.wireOp",EDGE,"E615"),sQuery(id+"F0.wireOp",EDGE,"E616"),sQuery(id+"F0.wireOp",EDGE,"E617"),sQuery(id+"F0.wireOp",EDGE,"E618"),sQuery(id+"F0.wireOp",EDGE,"E619"),sQuery(id+"F0.wireOp",EDGE,"E620"),sQuery(id+"F0.wireOp",EDGE,"E621"),sQuery(id+"F0.wireOp",EDGE,"E622"),sQuery(id+"F0.wireOp",EDGE,"E623"),sQuery(id+"F0.wireOp",EDGE,"E624"),sQuery(id+"F0.wireOp",EDGE,"E625"),sQuery(id+"F0.wireOp",EDGE,"E626"),sQuery(id+"F0.wireOp",EDGE,"E627"),sQuery(id+"F0.wireOp",EDGE,"E628"),sQuery(id+"F0.wireOp",EDGE,"E629"),sQuery(id+"F0.wireOp",EDGE,"E630"),sQuery(id+"F0.wireOp",EDGE,"E631"),sQuery(id+"F0.wireOp",EDGE,"E632"),sQuery(id+"F0.wireOp",EDGE,"E633"),sQuery(id+"F0.wireOp",EDGE,"E634"),sQuery(id+"F0.wireOp",EDGE,"E635"),sQuery(id+"F0.wireOp",EDGE,"E636"),sQuery(id+"F0.wireOp",EDGE,"E637"),sQuery(id+"F0.wireOp",EDGE,"E638"),sQuery(id+"F0.wireOp",EDGE,"E639"),sQuery(id+"F0.wireOp",EDGE,"E640"),sQuery(id+"F0.wireOp",EDGE,"E641"),sQuery(id+"F0.wireOp",EDGE,"E642"),sQuery(id+"F0.wireOp",EDGE,"E643"),sQuery(id+"F0.wireOp",EDGE,"E644"),sQuery(id+"F0.wireOp",EDGE,"E645"),sQuery(id+"F0.wireOp",EDGE,"E646"),sQuery(id+"F0.wireOp",EDGE,"E647"),sQuery(id+"F0.wireOp",EDGE,"E648"),sQuery(id+"F0.wireOp",EDGE,"E649"),sQuery(id+"F0.wireOp",EDGE,"E650"),sQuery(id+"F0.wireOp",EDGE,"E651"),sQuery(id+"F0.wireOp",EDGE,"E652"),sQuery(id+"F0.wireOp",EDGE,"E653"),sQuery(id+"F0.wireOp",EDGE,"E654"),sQuery(id+"F0.wireOp",EDGE,"E655"),sQuery(id+"F0.wireOp",EDGE,"E656"),sQuery(id+"F0.wireOp",EDGE,"E657"),sQuery(id+"F0.wireOp",EDGE,"E658"),sQuery(id+"F0.wireOp",EDGE,"E659"),sQuery(id+"F0.wireOp",EDGE,"E660"),sQuery(id+"F0.wireOp",EDGE,"E661"),sQuery(id+"F0.wireOp",EDGE,"E662"),sQuery(id+"F0.wireOp",EDGE,"E663"),sQuery(id+"F0.wireOp",EDGE,"E664"),sQuery(id+"F0.wireOp",EDGE,"E665"),sQuery(id+"F0.wireOp",EDGE,"E666"),sQuery(id+"F0.wireOp",EDGE,"E667"),sQuery(id+"F0.wireOp",EDGE,"E668"),sQuery(id+"F0.wireOp",EDGE,"E669"),sQuery(id+"F0.wireOp",EDGE,"E670"),sQuery(id+"F0.wireOp",EDGE,"E671"),sQuery(id+"F0.wireOp",EDGE,"E672"),sQuery(id+"F0.wireOp",EDGE,"E673"),sQuery(id+"F0.wireOp",EDGE,"E674"),sQuery(id+"F0.wireOp",EDGE,"E675"),sQuery(id+"F0.wireOp",EDGE,"E676"),sQuery(id+"F0.wireOp",EDGE,"E677"),sQuery(id+"F0.wireOp",EDGE,"E678"),sQuery(id+"F0.wireOp",EDGE,"E679"),sQuery(id+"F0.wireOp",EDGE,"E680"),sQuery(id+"F0.wireOp",EDGE,"E681"),sQuery(id+"F0.wireOp",EDGE,"E682"),sQuery(id+"F0.wireOp",EDGE,"E683"),sQuery(id+"F0.wireOp",EDGE,"E684"),sQuery(id+"F0.wireOp",EDGE,"E685"),sQuery(id+"F0.wireOp",EDGE,"E686"),sQuery(id+"F0.wireOp",EDGE,"E687"),sQuery(id+"F0.wireOp",EDGE,"E688"),sQuery(id+"F0.wireOp",EDGE,"E689"),sQuery(id+"F0.wireOp",EDGE,"E690"),sQuery(id+"F0.wireOp",EDGE,"E691"),sQuery(id+"F0.wireOp",EDGE,"E692"),sQuery(id+"F0.wireOp",EDGE,"E693"),sQuery(id+"F0.wireOp",EDGE,"E694"),sQuery(id+"F0.wireOp",EDGE,"E695"),sQuery(id+"F0.wireOp",EDGE,"E696"),sQuery(id+"F0.wireOp",EDGE,"E697"),sQuery(id+"F0.wireOp",EDGE,"E698"),sQuery(id+"F0.wireOp",EDGE,"E699"),sQuery(id+"F0.wireOp",EDGE,"E700"),sQuery(id+"F0.wireOp",EDGE,"E701"),sQuery(id+"F0.wireOp",EDGE,"E702"),sQuery(id+"F0.wireOp",EDGE,"E703"),sQuery(id+"F0.wireOp",EDGE,"E704"),sQuery(id+"F0.wireOp",EDGE,"E705"),sQuery(id+"F0.wireOp",EDGE,"E706"),sQuery(id+"F0.wireOp",EDGE,"E707"),sQuery(id+"F0.wireOp",EDGE,"E708"),sQuery(id+"F0.wireOp",EDGE,"E709"),sQuery(id+"F0.wireOp",EDGE,"E710"),sQuery(id+"F0.wireOp",EDGE,"E711"),sQuery(id+"F0.wireOp",EDGE,"E712"),sQuery(id+"F0.wireOp",EDGE,"E713"),sQuery(id+"F0.wireOp",EDGE,"E714"),sQuery(id+"F0.wireOp",EDGE,"E715"),sQuery(id+"F0.wireOp",EDGE,"E716"),sQuery(id+"F0.wireOp",EDGE,"E717"),sQuery(id+"F0.wireOp",EDGE,"E718"),sQuery(id+"F0.wireOp",EDGE,"E719"),sQuery(id+"F0.wireOp",EDGE,"E720"),sQuery(id+"F0.wireOp",EDGE,"E721"),sQuery(id+"F0.wireOp",EDGE,"E722"),sQuery(id+"F0.wireOp",EDGE,"E723"),sQuery(id+"F0.wireOp",EDGE,"E724"),sQuery(id+"F0.wireOp",EDGE,"E725"),sQuery(id+"F0.wireOp",EDGE,"E726"),sQuery(id+"F0.wireOp",EDGE,"E727"),sQuery(id+"F0.wireOp",EDGE,"E728"),sQuery(id+"F0.wireOp",EDGE,"E729"),sQuery(id+"F0.wireOp",EDGE,"E730"),sQuery(id+"F0.wireOp",EDGE,"E731"),sQuery(id+"F0.wireOp",EDGE,"E732"),sQuery(id+"F0.wireOp",EDGE,"E733"),sQuery(id+"F0.wireOp",EDGE,"E734"),sQuery(id+"F0.wireOp",EDGE,"E735"),sQuery(id+"F0.wireOp",EDGE,"E736"),sQuery(id+"F0.wireOp",EDGE,"E737"),sQuery(id+"F0.wireOp",EDGE,"E738"),sQuery(id+"F0.wireOp",EDGE,"E739"),sQuery(id+"F0.wireOp",EDGE,"E740"),sQuery(id+"F0.wireOp",EDGE,"E741"),sQuery(id+"F0.wireOp",EDGE,"E742"),sQuery(id+"F0.wireOp",EDGE,"E743"),sQuery(id+"F0.wireOp",EDGE,"E744"),sQuery(id+"F0.wireOp",EDGE,"E745"),sQuery(id+"F0.wireOp",EDGE,"E746"),sQuery(id+"F0.wireOp",EDGE,"E747"),sQuery(id+"F0.wireOp",EDGE,"E748"),sQuery(id+"F0.wireOp",EDGE,"E749"),sQuery(id+"F0.wireOp",EDGE,"E750"),sQuery(id+"F0.wireOp",EDGE,"E751"),sQuery(id+"F0.wireOp",EDGE,"E752"),sQuery(id+"F0.wireOp",EDGE,"E753"),sQuery(id+"F0.wireOp",EDGE,"E754"),sQuery(id+"F0.wireOp",EDGE,"E755"),sQuery(id+"F0.wireOp",EDGE,"E756"),sQuery(id+"F0.wireOp",EDGE,"E757"),sQuery(id+"F0.wireOp",EDGE,"E758"),sQuery(id+"F0.wireOp",EDGE,"E759"),sQuery(id+"F0.wireOp",EDGE,"E760"),sQuery(id+"F0.wireOp",EDGE,"E761"),sQuery(id+"F0.wireOp",EDGE,"E762"),sQuery(id+"F0.wireOp",EDGE,"E763"),sQuery(id+"F0.wireOp",EDGE,"E764"),sQuery(id+"F0.wireOp",EDGE,"E765"),sQuery(id+"F0.wireOp",EDGE,"E766"),sQuery(id+"F0.wireOp",EDGE,"E767"),sQuery(id+"F0.wireOp",EDGE,"E768"),sQuery(id+"F0.wireOp",EDGE,"E769"),sQuery(id+"F0.wireOp",EDGE,"E770"),sQuery(id+"F0.wireOp",EDGE,"E771"),sQuery(id+"F0.wireOp",EDGE,"E772"),sQuery(id+"F0.wireOp",EDGE,"E773"),sQuery(id+"F0.wireOp",EDGE,"E774"),sQuery(id+"F0.wireOp",EDGE,"E775"),sQuery(id+"F0.wireOp",EDGE,"E776"),sQuery(id+"F0.wireOp",EDGE,"E777"),sQuery(id+"F0.wireOp",EDGE,"E778"),sQuery(id+"F0.wireOp",EDGE,"E779"),sQuery(id+"F0.wireOp",EDGE,"E780"),sQuery(id+"F0.wireOp",EDGE,"E781"),sQuery(id+"F0.wireOp",EDGE,"E782"),sQuery(id+"F0.wireOp",EDGE,"E783"),sQuery(id+"F0.wireOp",EDGE,"E784"),sQuery(id+"F0.wireOp",EDGE,"E785"),sQuery(id+"F0.wireOp",EDGE,"E786"),sQuery(id+"F0.wireOp",EDGE,"E787"),sQuery(id+"F0.wireOp",EDGE,"E788"),sQuery(id+"F0.wireOp",EDGE,"E789"),sQuery(id+"F0.wireOp",EDGE,"E790"),sQuery(id+"F0.wireOp",EDGE,"E791"),sQuery(id+"F0.wireOp",EDGE,"E792"),sQuery(id+"F0.wireOp",EDGE,"E793"),sQuery(id+"F0.wireOp",EDGE,"E794"),sQuery(id+"F0.wireOp",EDGE,"E795"),sQuery(id+"F0.wireOp",EDGE,"E796"),sQuery(id+"F0.wireOp",EDGE,"E797"),sQuery(id+"F0.wireOp",EDGE,"E798"),sQuery(id+"F0.wireOp",EDGE,"E799"),sQuery(id+"F0.wireOp",EDGE,"E800"),sQuery(id+"F0.wireOp",EDGE,"E801"),sQuery(id+"F0.wireOp",EDGE,"E802"),sQuery(id+"F0.wireOp",EDGE,"E803"),sQuery(id+"F0.wireOp",EDGE,"E804"),sQuery(id+"F0.wireOp",EDGE,"E805"),sQuery(id+"F0.wireOp",EDGE,"E806"),sQuery(id+"F0.wireOp",EDGE,"E807"),sQuery(id+"F0.wireOp",EDGE,"E808"),sQuery(id+"F0.wireOp",EDGE,"E809"),sQuery(id+"F0.wireOp",EDGE,"E810"),sQuery(id+"F0.wireOp",EDGE,"E811"),sQuery(id+"F0.wireOp",EDGE,"E812"),sQuery(id+"F0.wireOp",EDGE,"E813"),sQuery(id+"F0.wireOp",EDGE,"E814"),sQuery(id+"F0.wireOp",EDGE,"E815"),sQuery(id+"F0.wireOp",EDGE,"E816"),sQuery(id+"F0.wireOp",EDGE,"E817"),sQuery(id+"F0.wireOp",EDGE,"E818"),sQuery(id+"F0.wireOp",EDGE,"E819"),sQuery(id+"F0.wireOp",EDGE,"E820"),sQuery(id+"F0.wireOp",EDGE,"E821"),sQuery(id+"F0.wireOp",EDGE,"E822"),sQuery(id+"F0.wireOp",EDGE,"E823"),sQuery(id+"F0.wireOp",EDGE,"E824"),sQuery(id+"F0.wireOp",EDGE,"E825"),sQuery(id+"F0.wireOp",EDGE,"E826"),sQuery(id+"F0.wireOp",EDGE,"E827"),sQuery(id+"F0.wireOp",EDGE,"E828"),sQuery(id+"F0.wireOp",EDGE,"E829"),sQuery(id+"F0.wireOp",EDGE,"E830"),sQuery(id+"F0.wireOp",EDGE,"E831"),sQuery(id+"F0.wireOp",EDGE,"E832"),sQuery(id+"F0.wireOp",EDGE,"E833"),sQuery(id+"F0.wireOp",EDGE,"E834"),sQuery(id+"F0.wireOp",EDGE,"E835"),sQuery(id+"F0.wireOp",EDGE,"E836"),sQuery(id+"F0.wireOp",EDGE,"E837"),sQuery(id+"F0.wireOp",EDGE,"E838"),sQuery(id+"F0.wireOp",EDGE,"E839"),sQuery(id+"F0.wireOp",EDGE,"E840"),sQuery(id+"F0.wireOp",EDGE,"E841"),sQuery(id+"F0.wireOp",EDGE,"E842"),sQuery(id+"F0.wireOp",EDGE,"E843"),sQuery(id+"F0.wireOp",EDGE,"E844"),sQuery(id+"F0.wireOp",EDGE,"E845"),sQuery(id+"F0.wireOp",EDGE,"E846"),sQuery(id+"F0.wireOp",EDGE,"E847"),sQuery(id+"F0.wireOp",EDGE,"E848"),sQuery(id+"F0.wireOp",EDGE,"E849"),sQuery(id+"F0.wireOp",EDGE,"E850"),sQuery(id+"F0.wireOp",EDGE,"E851"),sQuery(id+"F0.wireOp",EDGE,"E852"),sQuery(id+"F0.wireOp",EDGE,"E853"),sQuery(id+"F0.wireOp",EDGE,"E854"),sQuery(id+"F0.wireOp",EDGE,"E855"),sQuery(id+"F0.wireOp",EDGE,"E856"),sQuery(id+"F0.wireOp",EDGE,"E857"),sQuery(id+"F0.wireOp",EDGE,"E858"),sQuery(id+"F0.wireOp",EDGE,"E859"),sQuery(id+"F0.wireOp",EDGE,"E860"),sQuery(id+"F0.wireOp",EDGE,"E861"),sQuery(id+"F0.wireOp",EDGE,"E862"),sQuery(id+"F0.wireOp",EDGE,"E863"),sQuery(id+"F0.wireOp",EDGE,"E864"),sQuery(id+"F0.wireOp",EDGE,"E865"),sQuery(id+"F0.wireOp",EDGE,"E866"),sQuery(id+"F0.wireOp",EDGE,"E867"),sQuery(id+"F0.wireOp",EDGE,"E868"),sQuery(id+"F0.wireOp",EDGE,"E869"),sQuery(id+"F0.wireOp",EDGE,"E870"),sQuery(id+"F0.wireOp",EDGE,"E871"),sQuery(id+"F0.wireOp",EDGE,"E872"),sQuery(id+"F0.wireOp",EDGE,"E873"),sQuery(id+"F0.wireOp",EDGE,"E874"),sQuery(id+"F0.wireOp",EDGE,"E875"),sQuery(id+"F0.wireOp",EDGE,"E876"),sQuery(id+"F0.wireOp",EDGE,"E877"),sQuery(id+"F0.wireOp",EDGE,"E878"),sQuery(id+"F0.wireOp",EDGE,"E879"),sQuery(id+"F0.wireOp",EDGE,"E880"),sQuery(id+"F0.wireOp",EDGE,"E881"),sQuery(id+"F0.wireOp",EDGE,"E882"),sQuery(id+"F0.wireOp",EDGE,"E883"),sQuery(id+"F0.wireOp",EDGE,"E884"),sQuery(id+"F0.wireOp",EDGE,"E885"),sQuery(id+"F0.wireOp",EDGE,"E886"),sQuery(id+"F0.wireOp",EDGE,"E887"),sQuery(id+"F0.wireOp",EDGE,"E888"),sQuery(id+"F0.wireOp",EDGE,"E889"),sQuery(id+"F0.wireOp",EDGE,"E890"),sQuery(id+"F0.wireOp",EDGE,"E891"),sQuery(id+"F0.wireOp",EDGE,"E892"),sQuery(id+"F0.wireOp",EDGE,"E893"),sQuery(id+"F0.wireOp",EDGE,"E894"),sQuery(id+"F0.wireOp",EDGE,"E895"),sQuery(id+"F0.wireOp",EDGE,"E896"),sQuery(id+"F0.wireOp",EDGE,"E897"),sQuery(id+"F0.wireOp",EDGE,"E898"),sQuery(id+"F0.wireOp",EDGE,"E899"),sQuery(id+"F0.wireOp",EDGE,"E900"),sQuery(id+"F0.wireOp",EDGE,"E901"),sQuery(id+"F0.wireOp",EDGE,"E902"),sQuery(id+"F0.wireOp",EDGE,"E903"),sQuery(id+"F0.wireOp",EDGE,"E904"),sQuery(id+"F0.wireOp",EDGE,"E905"),sQuery(id+"F0.wireOp",EDGE,"E906"),sQuery(id+"F0.wireOp",EDGE,"E907"),sQuery(id+"F0.wireOp",EDGE,"E908"),sQuery(id+"F0.wireOp",EDGE,"E909"),sQuery(id+"F0.wireOp",EDGE,"E910"),sQuery(id+"F0.wireOp",EDGE,"E911"),sQuery(id+"F0.wireOp",EDGE,"E912"),sQuery(id+"F0.wireOp",EDGE,"E913"),sQuery(id+"F0.wireOp",EDGE,"E914"),sQuery(id+"F0.wireOp",EDGE,"E915"),sQuery(id+"F0.wireOp",EDGE,"E916"),sQuery(id+"F0.wireOp",EDGE,"E917"),sQuery(id+"F0.wireOp",EDGE,"E918"),sQuery(id+"F0.wireOp",EDGE,"E919"),sQuery(id+"F0.wireOp",EDGE,"E920"),sQuery(id+"F0.wireOp",EDGE,"E921"),sQuery(id+"F0.wireOp",EDGE,"E922"),sQuery(id+"F0.wireOp",EDGE,"E923"),sQuery(id+"F0.wireOp",EDGE,"E924"),sQuery(id+"F0.wireOp",EDGE,"E925"),sQuery(id+"F0.wireOp",EDGE,"E926"),sQuery(id+"F0.wireOp",EDGE,"E927"),sQuery(id+"F0.wireOp",EDGE,"E928"),sQuery(id+"F0.wireOp",EDGE,"E929"),sQuery(id+"F0.wireOp",EDGE,"E930"),sQuery(id+"F0.wireOp",EDGE,"E931"),sQuery(id+"F0.wireOp",EDGE,"E932"),sQuery(id+"F0.wireOp",EDGE,"E933"),sQuery(id+"F0.wireOp",EDGE,"E934"),sQuery(id+"F0.wireOp",EDGE,"E935"),sQuery(id+"F0.wireOp",EDGE,"E936"),sQuery(id+"F0.wireOp",EDGE,"E937"),sQuery(id+"F0.wireOp",EDGE,"E938"),sQuery(id+"F0.wireOp",EDGE,"E939"),sQuery(id+"F0.wireOp",EDGE,"E940"),sQuery(id+"F0.wireOp",EDGE,"E941"),sQuery(id+"F0.wireOp",EDGE,"E942"),sQuery(id+"F0.wireOp",EDGE,"E943"),sQuery(id+"F0.wireOp",EDGE,"E944"),sQuery(id+"F0.wireOp",EDGE,"E945"),sQuery(id+"F0.wireOp",EDGE,"E946"),sQuery(id+"F0.wireOp",EDGE,"E947"),sQuery(id+"F0.wireOp",EDGE,"E948"),sQuery(id+"F0.wireOp",EDGE,"E949"),sQuery(id+"F0.wireOp",EDGE,"E950"),sQuery(id+"F0.wireOp",EDGE,"E951"),sQuery(id+"F0.wireOp",EDGE,"E952"),sQuery(id+"F0.wireOp",EDGE,"E953"),sQuery(id+"F0.wireOp",EDGE,"E954"),sQuery(id+"F0.wireOp",EDGE,"E955"),sQuery(id+"F0.wireOp",EDGE,"E956"),sQuery(id+"F0.wireOp",EDGE,"E957"),sQuery(id+"F0.wireOp",EDGE,"E958"),sQuery(id+"F0.wireOp",EDGE,"E959"),sQuery(id+"F0.wireOp",EDGE,"E960"),sQuery(id+"F0.wireOp",EDGE,"E961"),sQuery(id+"F0.wireOp",EDGE,"E962"),sQuery(id+"F0.wireOp",EDGE,"E963"),sQuery(id+"F0.wireOp",EDGE,"E964"),sQuery(id+"F0.wireOp",EDGE,"E965"),sQuery(id+"F0.wireOp",EDGE,"E966"),sQuery(id+"F0.wireOp",EDGE,"E967"),sQuery(id+"F0.wireOp",EDGE,"E968"),sQuery(id+"F0.wireOp",EDGE,"E969"),sQuery(id+"F0.wireOp",EDGE,"E970"),sQuery(id+"F0.wireOp",EDGE,"E971"),sQuery(id+"F0.wireOp",EDGE,"E972"),sQuery(id+"F0.wireOp",EDGE,"E973"),sQuery(id+"F0.wireOp",EDGE,"E974"),sQuery(id+"F0.wireOp",EDGE,"E975"),sQuery(id+"F0.wireOp",EDGE,"E976"),sQuery(id+"F0.wireOp",EDGE,"E977"),sQuery(id+"F0.wireOp",EDGE,"E978"),sQuery(id+"F0.wireOp",EDGE,"E979"),sQuery(id+"F0.wireOp",EDGE,"E980"),sQuery(id+"F0.wireOp",EDGE,"E981"),sQuery(id+"F0.wireOp",EDGE,"E982"),sQuery(id+"F0.wireOp",EDGE,"E983"),sQuery(id+"F0.wireOp",EDGE,"E984"),sQuery(id+"F0.wireOp",EDGE,"E985"),sQuery(id+"F0.wireOp",EDGE,"E986"),sQuery(id+"F0.wireOp",EDGE,"E987"),sQuery(id+"F0.wireOp",EDGE,"E988"),sQuery(id+"F0.wireOp",EDGE,"E989"),sQuery(id+"F0.wireOp",EDGE,"E990"),sQuery(id+"F0.wireOp",EDGE,"E991"),sQuery(id+"F0.wireOp",EDGE,"E992"),sQuery(id+"F0.wireOp",EDGE,"E993"),sQuery(id+"F0.wireOp",EDGE,"E994"),sQuery(id+"F0.wireOp",EDGE,"E995"),sQuery(id+"F0.wireOp",EDGE,"E996"),sQuery(id+"F0.wireOp",EDGE,"E997"),sQuery(id+"F0.wireOp",EDGE,"E998"),sQuery(id+"F0.wireOp",EDGE,"E999"),sQuery(id+"F0.wireOp",EDGE,"E1000"),sQuery(id+"F0.wireOp",EDGE,"E1001"),sQuery(id+"F0.wireOp",EDGE,"E1002"),sQuery(id+"F0.wireOp",EDGE,"E1003"),sQuery(id+"F0.wireOp",EDGE,"E1004"),sQuery(id+"F0.wireOp",EDGE,"E1005"),sQuery(id+"F0.wireOp",EDGE,"E1006"),sQuery(id+"F0.wireOp",EDGE,"E1007"),sQuery(id+"F0.wireOp",EDGE,"E1008"),sQuery(id+"F0.wireOp",EDGE,"E1009"),sQuery(id+"F0.wireOp",EDGE,"E1010"),sQuery(id+"F0.wireOp",EDGE,"E1011"),sQuery(id+"F0.wireOp",EDGE,"E1012"),sQuery(id+"F0.wireOp",EDGE,"E1013"),sQuery(id+"F0.wireOp",EDGE,"E1014"),sQuery(id+"F0.wireOp",EDGE,"E1015"),sQuery(id+"F0.wireOp",EDGE,"E1016"),sQuery(id+"F0.wireOp",EDGE,"E1017"),sQuery(id+"F0.wireOp",EDGE,"E1018"),sQuery(id+"F0.wireOp",EDGE,"E1019"),sQuery(id+"F0.wireOp",EDGE,"E1020"),sQuery(id+"F0.wireOp",EDGE,"E1021"),sQuery(id+"F0.wireOp",EDGE,"E1022"),sQuery(id+"F0.wireOp",EDGE,"E1023"),sQuery(id+"F0.wireOp",EDGE,"E1024"),sQuery(id+"F0.wireOp",EDGE,"E1025"),sQuery(id+"F0.wireOp",EDGE,"E1026"),sQuery(id+"F0.wireOp",EDGE,"E1027"),sQuery(id+"F0.wireOp",EDGE,"E1028"),sQuery(id+"F0.wireOp",EDGE,"E1029"),sQuery(id+"F0.wireOp",EDGE,"E1030"),sQuery(id+"F0.wireOp",EDGE,"E1031"),sQuery(id+"F0.wireOp",EDGE,"E1032"),sQuery(id+"F0.wireOp",EDGE,"E1033"),sQuery(id+"F0.wireOp",EDGE,"E1034"),sQuery(id+"F0.wireOp",EDGE,"E1035"),sQuery(id+"F0.wireOp",EDGE,"E1036"),sQuery(id+"F0.wireOp",EDGE,"E1037"),sQuery(id+"F0.wireOp",EDGE,"E1038"),sQuery(id+"F0.wireOp",EDGE,"E1039"),sQuery(id+"F0.wireOp",EDGE,"E1040"),sQuery(id+"F0.wireOp",EDGE,"E1041"),sQuery(id+"F0.wireOp",EDGE,"E1042"),sQuery(id+"F0.wireOp",EDGE,"E1043"),sQuery(id+"F0.wireOp",EDGE,"E1044"),sQuery(id+"F0.wireOp",EDGE,"E1045"),sQuery(id+"F0.wireOp",EDGE,"E1046"),sQuery(id+"F0.wireOp",EDGE,"E1047"),sQuery(id+"F0.wireOp",EDGE,"E1048"),sQuery(id+"F0.wireOp",EDGE,"E1049"),sQuery(id+"F0.wireOp",EDGE,"E1050"),sQuery(id+"F0.wireOp",EDGE,"E1051"),sQuery(id+"F0.wireOp",EDGE,"E1052"),sQuery(id+"F0.wireOp",EDGE,"E1053"),sQuery(id+"F0.wireOp",EDGE,"E1054"),sQuery(id+"F0.wireOp",EDGE,"E1055"),sQuery(id+"F0.wireOp",EDGE,"E1056"),sQuery(id+"F0.wireOp",EDGE,"E1057"),sQuery(id+"F0.wireOp",EDGE,"E1058"),sQuery(id+"F0.wireOp",EDGE,"E1059"),sQuery(id+"F0.wireOp",EDGE,"E1060"),sQuery(id+"F0.wireOp",EDGE,"E1061"),sQuery(id+"F0.wireOp",EDGE,"E1062"),sQuery(id+"F0.wireOp",EDGE,"E1063"),sQuery(id+"F0.wireOp",EDGE,"E1064"),sQuery(id+"F0.wireOp",EDGE,"E1065"),sQuery(id+"F0.wireOp",EDGE,"E1066"),sQuery(id+"F0.wireOp",EDGE,"E1067"),sQuery(id+"F0.wireOp",EDGE,"E1068"),sQuery(id+"F0.wireOp",EDGE,"E1069"),sQuery(id+"F0.wireOp",EDGE,"E1070"),sQuery(id+"F0.wireOp",EDGE,"E1071"),sQuery(id+"F0.wireOp",EDGE,"E1072"),sQuery(id+"F0.wireOp",EDGE,"E1073"),sQuery(id+"F0.wireOp",EDGE,"E1074"),sQuery(id+"F0.wireOp",EDGE,"E1075"),sQuery(id+"F0.wireOp",EDGE,"E1076"),sQuery(id+"F0.wireOp",EDGE,"E1077"),sQuery(id+"F0.wireOp",EDGE,"E1078"),sQuery(id+"F0.wireOp",EDGE,"E1079"),sQuery(id+"F0.wireOp",EDGE,"E1080"),sQuery(id+"F0.wireOp",EDGE,"E1081"),sQuery(id+"F0.wireOp",EDGE,"E1082"),sQuery(id+"F0.wireOp",EDGE,"E1083"),sQuery(id+"F0.wireOp",EDGE,"E1084"),sQuery(id+"F0.wireOp",EDGE,"E1085"),sQuery(id+"F0.wireOp",EDGE,"E1086"),sQuery(id+"F0.wireOp",EDGE,"E1087"),sQuery(id+"F0.wireOp",EDGE,"E1088"),sQuery(id+"F0.wireOp",EDGE,"E1089"),sQuery(id+"F0.wireOp",EDGE,"E1090"),sQuery(id+"F0.wireOp",EDGE,"E1091"),sQuery(id+"F0.wireOp",EDGE,"E1092"),sQuery(id+"F0.wireOp",EDGE,"E1093"),sQuery(id+"F0.wireOp",EDGE,"E1094"),sQuery(id+"F0.wireOp",EDGE,"E1095"),sQuery(id+"F0.wireOp",EDGE,"E1096"),sQuery(id+"F0.wireOp",EDGE,"E1097"),sQuery(id+"F0.wireOp",EDGE,"E1098"),sQuery(id+"F0.wireOp",EDGE,"E1099"),sQuery(id+"F0.wireOp",EDGE,"E1100"),sQuery(id+"F0.wireOp",EDGE,"E1101"),sQuery(id+"F0.wireOp",EDGE,"E1102"),sQuery(id+"F0.wireOp",EDGE,"E1103"),sQuery(id+"F0.wireOp",EDGE,"E1104"),sQuery(id+"F0.wireOp",EDGE,"E1105"),sQuery(id+"F0.wireOp",EDGE,"E1106"),sQuery(id+"F0.wireOp",EDGE,"E1107"),sQuery(id+"F0.wireOp",EDGE,"E1108"),sQuery(id+"F0.wireOp",EDGE,"E1109"),sQuery(id+"F0.wireOp",EDGE,"E1110"),sQuery(id+"F0.wireOp",EDGE,"E1111"),sQuery(id+"F0.wireOp",EDGE,"E1112"),sQuery(id+"F0.wireOp",EDGE,"E1113"),sQuery(id+"F0.wireOp",EDGE,"E1114"),sQuery(id+"F0.wireOp",EDGE,"E1115"),sQuery(id+"F0.wireOp",EDGE,"E1116"),sQuery(id+"F0.wireOp",EDGE,"E1117"),sQuery(id+"F0.wireOp",EDGE,"E1118"),sQuery(id+"F0.wireOp",EDGE,"E1119"),sQuery(id+"F0.wireOp",EDGE,"E1120"),sQuery(id+"F0.wireOp",EDGE,"E1121"),sQuery(id+"F0.wireOp",EDGE,"E1122"),sQuery(id+"F0.wireOp",EDGE,"E1123"),sQuery(id+"F0.wireOp",EDGE,"E1124"),sQuery(id+"F0.wireOp",EDGE,"E1125"),sQuery(id+"F0.wireOp",EDGE,"E1126"),sQuery(id+"F0.wireOp",EDGE,"E1127"),sQuery(id+"F0.wireOp",EDGE,"E1128"),sQuery(id+"F0.wireOp",EDGE,"E1129"),sQuery(id+"F0.wireOp",EDGE,"E1130"),sQuery(id+"F0.wireOp",EDGE,"E1131"),sQuery(id+"F0.wireOp",EDGE,"E1132"),sQuery(id+"F0.wireOp",EDGE,"E1133"),sQuery(id+"F0.wireOp",EDGE,"E1134"),sQuery(id+"F0.wireOp",EDGE,"E1135"),sQuery(id+"F0.wireOp",EDGE,"E1136"),sQuery(id+"F0.wireOp",EDGE,"E1137"),sQuery(id+"F0.wireOp",EDGE,"E1138"),sQuery(id+"F0.wireOp",EDGE,"E1139"),sQuery(id+"F0.wireOp",EDGE,"E1140"),sQuery(id+"F0.wireOp",EDGE,"E1141"),sQuery(id+"F0.wireOp",EDGE,"E1142"),sQuery(id+"F0.wireOp",EDGE,"E1143"),sQuery(id+"F0.wireOp",EDGE,"E1144"),sQuery(id+"F0.wireOp",EDGE,"E1145"),sQuery(id+"F0.wireOp",EDGE,"E1146"),sQuery(id+"F0.wireOp",EDGE,"E1147"),sQuery(id+"F0.wireOp",EDGE,"E1148"),sQuery(id+"F0.wireOp",EDGE,"E1149"),sQuery(id+"F0.wireOp",EDGE,"E1150"),sQuery(id+"F0.wireOp",EDGE,"E1151"),sQuery(id+"F0.wireOp",EDGE,"E1152"),sQuery(id+"F0.wireOp",EDGE,"E1153"),sQuery(id+"F0.wireOp",EDGE,"E1154"),sQuery(id+"F0.wireOp",EDGE,"E1155"),sQuery(id+"F0.wireOp",EDGE,"E1156"),sQuery(id+"F0.wireOp",EDGE,"E1157"),sQuery(id+"F0.wireOp",EDGE,"E1158"),sQuery(id+"F0.wireOp",EDGE,"E1159"),sQuery(id+"F0.wireOp",EDGE,"E1160"),sQuery(id+"F0.wireOp",EDGE,"E1161"),sQuery(id+"F0.wireOp",EDGE,"E1162"),sQuery(id+"F0.wireOp",EDGE,"E1163"),sQuery(id+"F0.wireOp",EDGE,"E1164"),sQuery(id+"F0.wireOp",EDGE,"E1165"),sQuery(id+"F0.wireOp",EDGE,"E1166"),sQuery(id+"F0.wireOp",EDGE,"E1167")])],"isStart":false});
            var sketch = newSketch(context, id + "F3", { "sketchPlane" : qUnion([Q0])});
            skText(sketch, "E1174", { "text": "BRC", "fontName": "OpenSans-Bold.ttf"});
            skLineSegment(sketch, "E1175", {"start": v(6.85, 32.27) * mm, "end": v(-30.82, -40.25) * mm, "construction": true});
            skLineSegment(sketch, "E1176", {"start": v(4.35, 33.56) * mm, "end": v(9.35, 30.99) * mm, "construction": true});
            skLineSegment(sketch, "E1177", {"start": v(-53.98, -27.73) * mm, "end": v(-7.67, -52.77) * mm, "construction": true});
            const initialGuessF3  = {"E1174": [-0.01388, -0.0307, 0.46098, 0.8874, 0.01889]};
            skSetInitialGuess(sketch, initialGuessF3);
            skSolve(sketch);
        }
        {
            var Q0;
            Q0 = qSketchRegion(id + "F3", true);
            var Q1;
            Q1 = qConstructionFilter(qBodyType(qCreatedBy(id + "F3" ,EDGE), BodyType.WIRE), ConstructionObject.NO);
            extrude(context, id + "F4", {"entities" : qUnion([Q0]), "operationType" : NewBodyOperationType.REMOVE, "surfaceEntities" : qUnion([Q1]), "endBound" : BoundingType.THROUGH_ALL, "oppositeDirection" : true, "depth" : 25.4 * mm});
        }
        {
            var Q0;
            Q0 = qSketchRegion(id + "F2", true);
            extrude(context, id + "F5", {"entities" : qUnion([Q0]), "operationType" : NewBodyOperationType.ADD, "depth" : 2.54 * mm});
        }
    });
